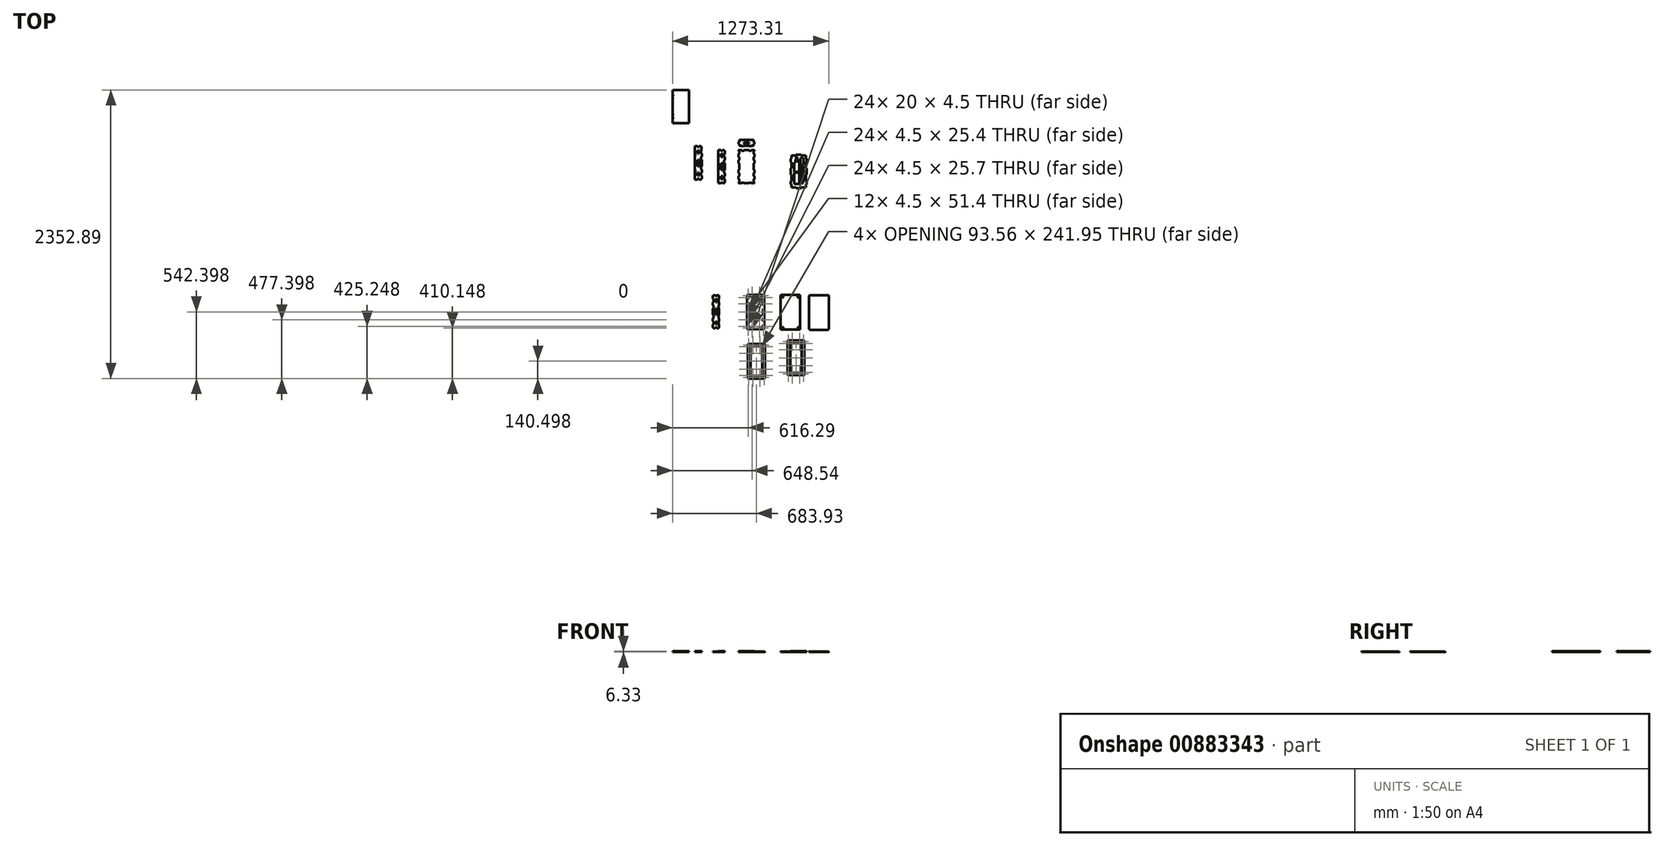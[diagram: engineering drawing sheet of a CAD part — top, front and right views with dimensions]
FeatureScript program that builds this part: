
annotation { "Feature Type Name" : "Feature", "Feature Type Description" : "" }
export const myFeature = defineFeature(function(context is Context, id is Id, definition is map)
    precondition{}
    {
        {
            var Q0;
            Q0=qCreatedBy(makeId("Top.planeOp"),FACE);
            var sketch = newSketch(context, id + "F0", { "sketchPlane" : qUnion([Q0])});
            skLineSegment(sketch, "E0.top", {"start": v(-19.7, 209.17) * mm, "end": v(-0.3, 209.17) * mm});
            skLineSegment(sketch, "E1.bottom", {"start": v(-188.56, 209.17) * mm, "end": v(-174.86, 209.17) * mm});
            skLineSegment(sketch, "E2.top", {"start": v(-40, 250.07) * mm, "end": v(-20.3, 250.07) * mm});
            skLineSegment(sketch, "E2.left", {"start": v(-40, 292.07) * mm, "end": v(-40, 278.37) * mm});
            skLineSegment(sketch, "E3", {"start": v(-154.23, 79.17) * mm, "end": v(-154.23, 105.17) * mm});
            skPoint(sketch, "E4.start.orphan", {"position": v(-160.56, 79.17) * mm});
            skLineSegment(sketch, "E5.bottom", {"start": v(-188.56, 209.17) * mm, "end": v(-181.56, 209.17) * mm});
            skLineSegment(sketch, "E6.0", {"start": v(-20, 298.4) * mm, "end": v(0, 298.4) * mm});
            skLineSegment(sketch, "E7", {"start": v(0, 244.57) * mm, "end": v(0, 243.74) * mm});
            skLineSegment(sketch, "E8", {"start": v(-46.33, 264.07) * mm, "end": v(-46.33, 271.07) * mm});
            skLineSegment(sketch, "E9", {"start": v(-188.56, 215.5) * mm, "end": v(-188.56, 209.17) * mm});
            skPoint(sketch, "E10.end.orphan", {"position": v(-46.33, 209.17) * mm});
            skLineSegment(sketch, "E11.trimOffspring", {"start": v(-154.23, 183.17) * mm, "end": v(-154.23, 209.17) * mm});
            skLineSegment(sketch, "E12.bottom", {"start": v(-45.5, 209.17) * mm, "end": v(-40, 209.17) * mm});
            skLineSegment(sketch, "E13.bottom", {"start": v(-691.17, 64.61) * mm, "end": v(-651.17, 64.61) * mm});
            skLineSegment(sketch, "E13.top", {"start": v(-691.17, -27.39) * mm, "end": v(-651.17, -27.39) * mm});
            skLineSegment(sketch, "E13.left", {"start": v(-691.17, 64.61) * mm, "end": v(-691.17, -27.39) * mm});
            skLineSegment(sketch, "E13.right", {"start": v(-651.17, 64.61) * mm, "end": v(-651.17, -27.39) * mm});
            skLineSegment(sketch, "E14.bottom", {"start": v(-642.38, 180.06) * mm, "end": v(-637.38, 180.06) * mm});
            skLineSegment(sketch, "E14.top", {"start": v(-642.38, 129.06) * mm, "end": v(-632.88, 129.06) * mm});
            skLineSegment(sketch, "E14.left", {"start": v(-642.38, 180.06) * mm, "end": v(-642.38, 129.06) * mm});
            skLineSegment(sketch, "E14.right", {"start": v(-616.38, 180.06) * mm, "end": v(-616.38, 129.06) * mm});
            skLineSegment(sketch, "E15", {"start": v(-629.38, 124.06) * mm, "end": v(-632.88, 124.06) * mm});
            skLineSegment(sketch, "E16", {"start": v(-632.88, 124.06) * mm, "end": v(-625.88, 124.06) * mm});
            skLineSegment(sketch, "E17", {"start": v(-625.88, 124.06) * mm, "end": v(-625.88, 129.06) * mm});
            skLineSegment(sketch, "E18", {"start": v(-632.88, 124.06) * mm, "end": v(-632.88, 129.06) * mm});
            skPoint(sketch, "E19.start.orphan", {"position": v(-629.38, 129.06) * mm});
            skLineSegment(sketch, "E20.trimOffspring", {"start": v(-625.88, 129.06) * mm, "end": v(-616.38, 129.06) * mm});
            skLineSegment(sketch, "E21", {"start": v(-629.38, 190.06) * mm, "end": v(-621.38, 190.06) * mm});
            skLineSegment(sketch, "E22", {"start": v(-621.38, 190.06) * mm, "end": v(-629.38, 190.06) * mm});
            skLineSegment(sketch, "E23", {"start": v(-629.38, 190.06) * mm, "end": v(-637.38, 190.06) * mm});
            skLineSegment(sketch, "E24", {"start": v(-637.38, 190.06) * mm, "end": v(-637.38, 180.06) * mm});
            skLineSegment(sketch, "E25", {"start": v(-621.38, 190.06) * mm, "end": v(-621.38, 180.06) * mm});
            skPoint(sketch, "E26.start.orphan", {"position": v(-629.38, 180.06) * mm});
            skLineSegment(sketch, "E27.trimOffspring", {"start": v(-621.38, 180.06) * mm, "end": v(-616.38, 180.06) * mm});
            skLineSegment(sketch, "E28.bottom", {"start": v(-676.6, 190.8) * mm, "end": v(-665.6, 190.8) * mm});
            skLineSegment(sketch, "E28.top", {"start": v(-691.1, 70.8) * mm, "end": v(-651.1, 70.8) * mm});
            skLineSegment(sketch, "E28.left", {"start": v(-691.1, 148.8) * mm, "end": v(-691.1, 70.8) * mm});
            skLineSegment(sketch, "E29", {"start": v(-691.1, 148.8) * mm, "end": v(-680.1, 148.8) * mm});
            skPoint(sketch, "E30.end.orphan", {"position": v(-676.74, 148.8) * mm});
            skLineSegment(sketch, "E31", {"start": v(-681.6, 153.8) * mm, "end": v(-680.1, 153.8) * mm});
            skLineSegment(sketch, "E32", {"start": v(-676.6, 171.8) * mm, "end": v(-681.6, 171.8) * mm});
            skLineSegment(sketch, "E33", {"start": v(-681.6, 171.8) * mm, "end": v(-676.6, 171.8) * mm});
            skLineSegment(sketch, "E34", {"start": v(-660.6, 171.8) * mm, "end": v(-660.6, 153.8) * mm});
            skLineSegment(sketch, "E35", {"start": v(-662.1, 148.8) * mm, "end": v(-662.1, 153.8) * mm});
            skLineSegment(sketch, "E36", {"start": v(-681.6, 171.8) * mm, "end": v(-681.6, 153.8) * mm});
            skLineSegment(sketch, "E37", {"start": v(-680.1, 148.8) * mm, "end": v(-680.1, 153.8) * mm});
            skLineSegment(sketch, "E38", {"start": v(-665.6, 171.8) * mm, "end": v(-665.6, 189.8) * mm});
            skLineSegment(sketch, "E39", {"start": v(-665.6, 189.8) * mm, "end": v(-665.6, 190.8) * mm});
            skLineSegment(sketch, "E40", {"start": v(-676.6, 171.8) * mm, "end": v(-676.6, 190.8) * mm});
            skLineSegment(sketch, "E41.trimOffspring", {"start": v(-651.1, 148.8) * mm, "end": v(-651.1, 70.8) * mm});
            skPoint(sketch, "E28.right.end.orphan", {"position": v(-651.1, 153.8) * mm});
            skPoint(sketch, "E42.orphan", {"position": v(-691.1, 153.8) * mm});
            skLineSegment(sketch, "E43.trimOffspring", {"start": v(-662.1, 148.8) * mm, "end": v(-651.1, 148.8) * mm});
            skPoint(sketch, "E44.end.orphan", {"position": v(-671.1, 148.8) * mm});
            skLineSegment(sketch, "E45.trimOffspring", {"start": v(-662.1, 153.8) * mm, "end": v(-660.6, 153.8) * mm});
            skPoint(sketch, "E46.start.orphan", {"position": v(-671.1, 153.8) * mm});
            skLineSegment(sketch, "E47.trimOffspring", {"start": v(-665.6, 171.8) * mm, "end": v(-660.6, 171.8) * mm});
            skLineSegment(sketch, "E48.bottom", {"start": v(-639.24, 119.2) * mm, "end": v(-620.24, 119.2) * mm});
            skLineSegment(sketch, "E48.top", {"start": v(-639.24, 53.2) * mm, "end": v(-620.24, 53.2) * mm});
            skLineSegment(sketch, "E48.left", {"start": v(-639.24, 119.2) * mm, "end": v(-639.24, 53.2) * mm});
            skLineSegment(sketch, "E48.right", {"start": v(-620.24, 119.2) * mm, "end": v(-620.24, 53.2) * mm});
            skLineSegment(sketch, "E49.bottom", {"start": v(-639.24, 44.85) * mm, "end": v(-620.24, 44.85) * mm});
            skLineSegment(sketch, "E49.top", {"start": v(-639.24, -21.15) * mm, "end": v(-620.24, -21.15) * mm});
            skLineSegment(sketch, "E49.left", {"start": v(-639.24, 44.85) * mm, "end": v(-639.24, -21.15) * mm});
            skLineSegment(sketch, "E49.right", {"start": v(-620.24, 44.85) * mm, "end": v(-620.24, -21.15) * mm});
            skLineSegment(sketch, "E50.bottom", {"start": v(-715.7, -55.97) * mm, "end": v(-595.7, -55.97) * mm});
            skLineSegment(sketch, "E50.top", {"start": v(-715.7, 204.03) * mm, "end": v(-595.7, 204.03) * mm});
            skLineSegment(sketch, "E50.left", {"start": v(-715.7, -55.97) * mm, "end": v(-715.7, 204.03) * mm});
            skLineSegment(sketch, "E50.right", {"start": v(-595.7, -55.97) * mm, "end": v(-595.7, 204.03) * mm});
            skLineSegment(sketch, "E51.bottom", {"start": v(-878.27, 204.03) * mm, "end": v(-836.27, 204.03) * mm});
            skLineSegment(sketch, "E51.top", {"start": v(-878.27, -55.97) * mm, "end": v(-836.27, -55.97) * mm});
            skLineSegment(sketch, "E51.left", {"start": v(-878.27, 204.03) * mm, "end": v(-878.27, -55.97) * mm});
            skLineSegment(sketch, "E51.right", {"start": v(-836.27, 204.03) * mm, "end": v(-836.27, -55.97) * mm});
            skLineSegment(sketch, "E52.bottom", {"start": v(-715.7, 286.93) * mm, "end": v(-595.7, 286.93) * mm});
            skLineSegment(sketch, "E52.top", {"start": v(-715.7, 244.93) * mm, "end": v(-595.7, 244.93) * mm});
            skLineSegment(sketch, "E52.left", {"start": v(-715.7, 286.93) * mm, "end": v(-715.7, 244.93) * mm});
            skLineSegment(sketch, "E52.right", {"start": v(-595.7, 286.93) * mm, "end": v(-595.7, 244.93) * mm});
            skLineSegment(sketch, "E53", {"start": v(-829.94, 74.03) * mm, "end": v(-829.94, 100.03) * mm});
            skLineSegment(sketch, "E54", {"start": v(-829.94, 204.03) * mm, "end": v(-836.27, 204.03) * mm});
            skLineSegment(sketch, "E55.bottom", {"start": v(-836.27, -55.97) * mm, "end": v(-829.94, -55.97) * mm});
            skLineSegment(sketch, "E55.top", {"start": v(-836.27, 204.03) * mm, "end": v(-829.94, 204.03) * mm});
            skLineSegment(sketch, "E55.left", {"start": v(-836.27, -55.97) * mm, "end": v(-836.27, 204.03) * mm});
            skLineSegment(sketch, "E55.right", {"start": v(-829.94, -55.97) * mm, "end": v(-829.94, 100.03) * mm});
            skPoint(sketch, "E56.start.orphan", {"position": v(-836.27, 74.03) * mm});
            skLineSegment(sketch, "E57", {"start": v(-836.27, 204.03) * mm, "end": v(-836.27, 210.36) * mm});
            skLineSegment(sketch, "E58.left", {"start": v(-878.27, 204.03) * mm, "end": v(-878.27, 210.36) * mm});
            skLineSegment(sketch, "E59", {"start": v(-878.27, -55.97) * mm, "end": v(-884.6, -55.97) * mm});
            skLineSegment(sketch, "E60.bottom", {"start": v(-884.6, -55.97) * mm, "end": v(-878.27, -55.97) * mm});
            skLineSegment(sketch, "E60.top", {"start": v(-884.6, 204.03) * mm, "end": v(-878.27, 204.03) * mm});
            skLineSegment(sketch, "E60.left", {"start": v(-884.6, -55.97) * mm, "end": v(-884.6, 204.03) * mm});
            skLineSegment(sketch, "E60.right", {"start": v(-878.27, -55.97) * mm, "end": v(-878.27, 204.03) * mm});
            skLineSegment(sketch, "E61", {"start": v(-836.27, -55.97) * mm, "end": v(-836.27, -62.3) * mm});
            skLineSegment(sketch, "E62.top", {"start": v(-878.27, -62.3) * mm, "end": v(-836.27, -62.3) * mm});
            skLineSegment(sketch, "E62.left", {"start": v(-878.27, -55.97) * mm, "end": v(-878.27, -62.3) * mm});
            skLineSegment(sketch, "E63.0", {"start": v(-715.7, 293.26) * mm, "end": v(-595.7, 293.26) * mm});
            skLineSegment(sketch, "E63.2", {"start": v(-695.7, 238.6) * mm, "end": v(-675.7, 238.6) * mm});
            skLineSegment(sketch, "E63.3", {"start": v(-589.38, 286.93) * mm, "end": v(-589.38, 244.93) * mm});
            skLineSegment(sketch, "E64.right", {"start": v(-715.7, 293.26) * mm, "end": v(-715.7, 286.93) * mm});
            skLineSegment(sketch, "E65.bottom", {"start": v(-595.7, 286.93) * mm, "end": v(-589.38, 286.93) * mm});
            skLineSegment(sketch, "E65.left", {"start": v(-595.7, 286.93) * mm, "end": v(-595.7, 293.26) * mm});
            skLineSegment(sketch, "E66.bottom", {"start": v(-595.7, 244.93) * mm, "end": v(-589.38, 244.93) * mm});
            skLineSegment(sketch, "E66.left", {"start": v(-595.7, 244.93) * mm, "end": v(-595.7, 238.6) * mm});
            skLineSegment(sketch, "E67.0", {"start": v(-715.7, 210.36) * mm, "end": v(-695.7, 210.36) * mm});
            skLineSegment(sketch, "E67.1", {"start": v(-722.04, -55.97) * mm, "end": v(-722.04, 74.03) * mm});
            skLineSegment(sketch, "E67.2", {"start": v(-715.7, -62.3) * mm, "end": v(-595.7, -62.3) * mm});
            skLineSegment(sketch, "E67.3", {"start": v(-589.38, -55.97) * mm, "end": v(-589.38, 204.03) * mm});
            skLineSegment(sketch, "E68.bottom", {"start": v(-595.7, 204.03) * mm, "end": v(-589.38, 204.03) * mm});
            skLineSegment(sketch, "E68.left", {"start": v(-595.7, 204.03) * mm, "end": v(-595.7, 210.36) * mm});
            skLineSegment(sketch, "E69.top", {"start": v(-589.38, -55.97) * mm, "end": v(-595.7, -55.97) * mm});
            skLineSegment(sketch, "E69.right", {"start": v(-595.7, -62.3) * mm, "end": v(-595.7, -55.97) * mm});
            skLineSegment(sketch, "E70.top", {"start": v(-722.04, -55.97) * mm, "end": v(-715.7, -55.97) * mm});
            skLineSegment(sketch, "E70.right", {"start": v(-715.7, -62.3) * mm, "end": v(-715.7, -55.97) * mm});
            skLineSegment(sketch, "E71", {"start": v(-655.7, 204.03) * mm, "end": v(-655.7, 189.78) * mm});
            skLineSegment(sketch, "E72", {"start": v(-655.7, 204.03) * mm, "end": v(-655.7, 210.36) * mm});
            skLineSegment(sketch, "E73", {"start": v(-655.7, 210.36) * mm, "end": v(-675.7, 210.36) * mm});
            skLineSegment(sketch, "E74", {"start": v(-675.7, 210.36) * mm, "end": v(-675.7, 204.03) * mm});
            skLineSegment(sketch, "E75", {"start": v(-695.7, 210.36) * mm, "end": v(-695.7, 204.03) * mm});
            skLineSegment(sketch, "E76.trimOffspring", {"start": v(-695.7, 210.36) * mm, "end": v(-715.7, 210.36) * mm});
            skLineSegment(sketch, "E77.trimOffspring", {"start": v(-675.7, 210.36) * mm, "end": v(-595.7, 210.36) * mm});
            skLineSegment(sketch, "E78", {"start": v(-695.7, 244.93) * mm, "end": v(-695.7, 238.6) * mm});
            skLineSegment(sketch, "E79", {"start": v(-675.7, 244.93) * mm, "end": v(-675.7, 238.6) * mm});
            skLineSegment(sketch, "E80", {"start": v(-655.7, 238.6) * mm, "end": v(-655.7, 244.93) * mm});
            skLineSegment(sketch, "E81.trimOffspring", {"start": v(-655.7, 238.6) * mm, "end": v(-595.7, 238.6) * mm});
            skLineSegment(sketch, "E82", {"start": v(-722.04, 258.93) * mm, "end": v(-722.04, 272.93) * mm});
            skLineSegment(sketch, "E83", {"start": v(-722.04, 258.93) * mm, "end": v(-715.7, 258.93) * mm});
            skLineSegment(sketch, "E84", {"start": v(-722.04, 272.93) * mm, "end": v(-715.7, 272.93) * mm});
            skLineSegment(sketch, "E85", {"start": v(-878.27, 210.36) * mm, "end": v(-864.27, 210.36) * mm});
            skLineSegment(sketch, "E86", {"start": v(-850.27, 210.36) * mm, "end": v(-836.27, 210.36) * mm});
            skLineSegment(sketch, "E87", {"start": v(-850.27, 210.36) * mm, "end": v(-850.27, 204.03) * mm});
            skLineSegment(sketch, "E88", {"start": v(-864.27, 210.36) * mm, "end": v(-864.27, 204.03) * mm});
            skLineSegment(sketch, "E89", {"start": v(-722.04, 74.03) * mm, "end": v(-715.7, 74.03) * mm});
            skLineSegment(sketch, "E90", {"start": v(-722.04, 100.03) * mm, "end": v(-722.04, 126.03) * mm});
            skLineSegment(sketch, "E91", {"start": v(-722.04, 152.03) * mm, "end": v(-722.04, 178.03) * mm});
            skLineSegment(sketch, "E92", {"start": v(-722.04, 178.03) * mm, "end": v(-715.7, 178.03) * mm});
            skLineSegment(sketch, "E93", {"start": v(-722.04, 152.03) * mm, "end": v(-715.7, 152.03) * mm});
            skLineSegment(sketch, "E94", {"start": v(-722.04, 126.03) * mm, "end": v(-715.7, 126.03) * mm});
            skLineSegment(sketch, "E95", {"start": v(-722.04, 100.03) * mm, "end": v(-715.7, 100.03) * mm});
            skPoint(sketch, "E96.end.orphan", {"position": v(-722.04, 204.03) * mm});
            skLineSegment(sketch, "E97", {"start": v(-829.94, 178.03) * mm, "end": v(-836.27, 178.03) * mm});
            skLineSegment(sketch, "E98", {"start": v(-829.94, 152.03) * mm, "end": v(-836.27, 152.03) * mm});
            skLineSegment(sketch, "E99", {"start": v(-829.94, 126.03) * mm, "end": v(-836.27, 126.03) * mm});
            skLineSegment(sketch, "E100", {"start": v(-829.94, 100.03) * mm, "end": v(-836.27, 100.03) * mm});
            skLineSegment(sketch, "E101", {"start": v(-829.94, 74.03) * mm, "end": v(-836.27, 74.03) * mm});
            skLineSegment(sketch, "E102.trimOffspring", {"start": v(-829.94, 126.03) * mm, "end": v(-829.94, 152.03) * mm});
            skLineSegment(sketch, "E103.trimOffspring", {"start": v(-829.94, 178.03) * mm, "end": v(-829.94, 204.03) * mm});
            skLineSegment(sketch, "E104.bottom", {"start": v(-722.04, 204.03) * mm, "end": v(-715.7, 204.03) * mm});
            skLineSegment(sketch, "E104.top", {"start": v(-722.04, 210.36) * mm, "end": v(-715.7, 210.36) * mm});
            skLineSegment(sketch, "E104.left", {"start": v(-722.04, 204.03) * mm, "end": v(-722.04, 210.36) * mm});
            skLineSegment(sketch, "E105.trimOffspring", {"start": v(-160.56, 105.47) * mm, "end": v(-160.56, 130.87) * mm});
            skLineSegment(sketch, "E106.trimOffspring", {"start": v(-160.56, 157.47) * mm, "end": v(-160.56, 182.87) * mm});
            skLineSegment(sketch, "E107.trimOffspring", {"start": v(-160.56, 130.87) * mm, "end": v(-160.56, 105.47) * mm});
            skLineSegment(sketch, "E108.MirrorCS", {"start": v(44.01, 243.74) * mm, "end": v(40, 243.74) * mm});
            skLineSegment(sketch, "E109.MirrorCS", {"start": v(44.01, 244.57) * mm, "end": v(44.01, 243.74) * mm});
            skPoint(sketch, "E110.end.orphan", {"position": v(20, 250.07) * mm});
            skPoint(sketch, "E110.start.orphan", {"position": v(20, 243.74) * mm});
            skLineSegment(sketch, "E111.trimOffspring", {"start": v(0.3, 250.07) * mm, "end": v(20, 250.07) * mm});
            skLineSegment(sketch, "E112.trimOffspring", {"start": v(60.3, 250.07) * mm, "end": v(80, 250.07) * mm});
            skLineSegment(sketch, "E113.trimOffspring", {"start": v(80, 263.77) * mm, "end": v(80, 250.07) * mm});
            skLineSegment(sketch, "E114.trimOffspring", {"start": v(-40, 263.77) * mm, "end": v(-40, 250.07) * mm});
            skLineSegment(sketch, "E115.MirrorCS", {"start": v(40, 298.4) * mm, "end": v(60, 298.4) * mm});
            skPoint(sketch, "E116.start.orphan", {"position": v(-46.33, 271.07) * mm});
            skLineSegment(sketch, "E117.trimOffspring", {"start": v(-40, 79.17) * mm, "end": v(-40, 104.87) * mm});
            skLineSegment(sketch, "E118.trimOffspring", {"start": v(-40, 131.47) * mm, "end": v(-40, 156.87) * mm});
            skLineSegment(sketch, "E119.trimOffspring", {"start": v(-40, 183.47) * mm, "end": v(-40, 209.17) * mm});
            skPoint(sketch, "E120.start.orphan", {"position": v(-46.33, 79.17) * mm});
            skLineSegment(sketch, "E121.bottom", {"start": v(410.43, 29.57) * mm, "end": v(450.43, 29.57) * mm});
            skLineSegment(sketch, "E121.top", {"start": v(410.43, -62.43) * mm, "end": v(450.43, -62.43) * mm});
            skLineSegment(sketch, "E121.left", {"start": v(410.43, 29.57) * mm, "end": v(410.43, -62.43) * mm});
            skLineSegment(sketch, "E121.right", {"start": v(450.43, 29.57) * mm, "end": v(450.43, -62.43) * mm});
            skLineSegment(sketch, "E122.bottom", {"start": v(459.21, 145.03) * mm, "end": v(464.21, 145.03) * mm});
            skLineSegment(sketch, "E122.top", {"start": v(459.21, 94.03) * mm, "end": v(468.71, 94.03) * mm});
            skLineSegment(sketch, "E122.left", {"start": v(459.21, 145.03) * mm, "end": v(459.21, 94.03) * mm});
            skLineSegment(sketch, "E122.right", {"start": v(485.21, 145.03) * mm, "end": v(485.21, 94.03) * mm});
            skLineSegment(sketch, "E123", {"start": v(472.21, 89.03) * mm, "end": v(468.71, 89.03) * mm});
            skLineSegment(sketch, "E124", {"start": v(468.71, 89.03) * mm, "end": v(475.71, 89.03) * mm});
            skLineSegment(sketch, "E125", {"start": v(475.71, 89.03) * mm, "end": v(475.71, 94.03) * mm});
            skLineSegment(sketch, "E126", {"start": v(468.71, 89.03) * mm, "end": v(468.71, 94.03) * mm});
            skPoint(sketch, "E127.start.orphan", {"position": v(472.21, 94.03) * mm});
            skLineSegment(sketch, "E128.trimOffspring", {"start": v(475.71, 94.03) * mm, "end": v(485.21, 94.03) * mm});
            skLineSegment(sketch, "E129", {"start": v(472.21, 155.03) * mm, "end": v(480.21, 155.03) * mm});
            skLineSegment(sketch, "E130", {"start": v(480.21, 155.03) * mm, "end": v(472.21, 155.03) * mm});
            skLineSegment(sketch, "E131", {"start": v(472.21, 155.03) * mm, "end": v(464.21, 155.03) * mm});
            skLineSegment(sketch, "E132", {"start": v(464.21, 155.03) * mm, "end": v(464.21, 145.03) * mm});
            skLineSegment(sketch, "E133", {"start": v(480.21, 155.03) * mm, "end": v(480.21, 145.03) * mm});
            skPoint(sketch, "E134.start.orphan", {"position": v(472.21, 145.03) * mm});
            skLineSegment(sketch, "E135.trimOffspring", {"start": v(480.21, 145.03) * mm, "end": v(485.21, 145.03) * mm});
            skLineSegment(sketch, "E136.bottom", {"start": v(425, 155.77) * mm, "end": v(436, 155.77) * mm});
            skLineSegment(sketch, "E136.top", {"start": v(410.5, 35.77) * mm, "end": v(450.5, 35.77) * mm});
            skLineSegment(sketch, "E136.left", {"start": v(410.5, 113.77) * mm, "end": v(410.5, 35.77) * mm});
            skLineSegment(sketch, "E137", {"start": v(410.5, 113.77) * mm, "end": v(421.5, 113.77) * mm});
            skPoint(sketch, "E138.end.orphan", {"position": v(424.86, 113.77) * mm});
            skLineSegment(sketch, "E139", {"start": v(420, 118.77) * mm, "end": v(421.5, 118.77) * mm});
            skLineSegment(sketch, "E140", {"start": v(425, 136.77) * mm, "end": v(420, 136.77) * mm});
            skLineSegment(sketch, "E141", {"start": v(420, 136.77) * mm, "end": v(425, 136.77) * mm});
            skLineSegment(sketch, "E142", {"start": v(441, 136.77) * mm, "end": v(441, 118.77) * mm});
            skLineSegment(sketch, "E143", {"start": v(439.5, 113.77) * mm, "end": v(439.5, 118.77) * mm});
            skLineSegment(sketch, "E144", {"start": v(420, 136.77) * mm, "end": v(420, 118.77) * mm});
            skLineSegment(sketch, "E145", {"start": v(421.5, 113.77) * mm, "end": v(421.5, 118.77) * mm});
            skLineSegment(sketch, "E146", {"start": v(436, 136.77) * mm, "end": v(436, 154.77) * mm});
            skLineSegment(sketch, "E147", {"start": v(436, 154.77) * mm, "end": v(436, 155.77) * mm});
            skLineSegment(sketch, "E148", {"start": v(425, 136.77) * mm, "end": v(425, 155.77) * mm});
            skLineSegment(sketch, "E149.trimOffspring", {"start": v(450.5, 113.77) * mm, "end": v(450.5, 35.77) * mm});
            skPoint(sketch, "E136.right.end.orphan", {"position": v(450.5, 118.77) * mm});
            skPoint(sketch, "E150.orphan", {"position": v(410.5, 118.77) * mm});
            skLineSegment(sketch, "E151.trimOffspring", {"start": v(439.5, 113.77) * mm, "end": v(450.5, 113.77) * mm});
            skPoint(sketch, "E152.end.orphan", {"position": v(430.5, 113.77) * mm});
            skLineSegment(sketch, "E153.trimOffspring", {"start": v(439.5, 118.77) * mm, "end": v(441, 118.77) * mm});
            skPoint(sketch, "E154.start.orphan", {"position": v(430.5, 118.77) * mm});
            skLineSegment(sketch, "E155.trimOffspring", {"start": v(436, 136.77) * mm, "end": v(441, 136.77) * mm});
            skLineSegment(sketch, "E156.bottom", {"start": v(462.36, 84.16) * mm, "end": v(481.36, 84.16) * mm});
            skLineSegment(sketch, "E156.top", {"start": v(462.36, 18.16) * mm, "end": v(481.36, 18.16) * mm});
            skLineSegment(sketch, "E156.left", {"start": v(462.36, 84.16) * mm, "end": v(462.36, 18.16) * mm});
            skLineSegment(sketch, "E156.right", {"start": v(481.36, 84.16) * mm, "end": v(481.36, 18.16) * mm});
            skLineSegment(sketch, "E157.bottom", {"start": v(462.36, 9.81) * mm, "end": v(481.36, 9.81) * mm});
            skLineSegment(sketch, "E157.top", {"start": v(462.36, -56.19) * mm, "end": v(481.36, -56.19) * mm});
            skLineSegment(sketch, "E157.left", {"start": v(462.36, 9.81) * mm, "end": v(462.36, -56.19) * mm});
            skLineSegment(sketch, "E157.right", {"start": v(481.36, 9.81) * mm, "end": v(481.36, -56.19) * mm});
            skLineSegment(sketch, "E158.bottom", {"start": v(405.88, -91.01) * mm, "end": v(425.88, -91.01) * mm});
            skLineSegment(sketch, "E158.top", {"start": v(405.88, 168.99) * mm, "end": v(425.88, 168.99) * mm});
            skLineSegment(sketch, "E158.left", {"start": v(385.88, -91.01) * mm, "end": v(385.88, -65.01) * mm});
            skLineSegment(sketch, "E158.right", {"start": v(505.88, -91.01) * mm, "end": v(505.88, -65.01) * mm});
            skLineSegment(sketch, "E159.1", {"start": v(379.55, -65.01) * mm, "end": v(379.55, -39.01) * mm});
            skLineSegment(sketch, "E160", {"start": v(445.88, 175.32) * mm, "end": v(425.88, 175.32) * mm});
            skLineSegment(sketch, "E161", {"start": v(425.88, 175.32) * mm, "end": v(425.88, 168.99) * mm});
            skLineSegment(sketch, "E162.trimOffspring", {"start": v(425.88, 175.32) * mm, "end": v(465.88, 175.32) * mm});
            skLineSegment(sketch, "E163", {"start": v(379.55, 116.99) * mm, "end": v(379.55, 142.99) * mm});
            skLineSegment(sketch, "E164", {"start": v(379.55, 142.99) * mm, "end": v(385.88, 142.99) * mm});
            skLineSegment(sketch, "E165", {"start": v(379.55, 116.99) * mm, "end": v(385.88, 116.99) * mm});
            skLineSegment(sketch, "E166", {"start": v(379.55, 64.99) * mm, "end": v(385.88, 64.99) * mm});
            skPoint(sketch, "E167.end.orphan", {"position": v(379.55, 168.99) * mm});
            skPoint(sketch, "E168.start.orphan", {"position": v(445.88, 203.56) * mm});
            skLineSegment(sketch, "E169.MirrorCS", {"start": v(379.55, 12.99) * mm, "end": v(385.88, 12.99) * mm});
            skLineSegment(sketch, "E170.MirrorCS", {"start": v(379.55, -39.01) * mm, "end": v(385.88, -39.01) * mm});
            skLineSegment(sketch, "E171.MirrorCS", {"start": v(379.55, -39.01) * mm, "end": v(379.55, -65.01) * mm});
            skLineSegment(sketch, "E172.MirrorCS", {"start": v(379.55, -65.01) * mm, "end": v(385.88, -65.01) * mm});
            skLineSegment(sketch, "E173.trimOffspring", {"start": v(385.88, -39.01) * mm, "end": v(385.88, -13.01) * mm});
            skLineSegment(sketch, "E174.trimOffspring", {"start": v(385.88, 90.99) * mm, "end": v(385.88, 116.99) * mm});
            skLineSegment(sketch, "E175.trimOffspring", {"start": v(385.88, 142.99) * mm, "end": v(385.88, 168.99) * mm});
            skLineSegment(sketch, "E176.trimOffspring", {"start": v(465.88, 168.99) * mm, "end": v(485.88, 168.99) * mm});
            skLineSegment(sketch, "E177.MirrorCS", {"start": v(425.88, -97.34) * mm, "end": v(425.88, -91.01) * mm});
            skLineSegment(sketch, "E178.MirrorCS", {"start": v(465.88, 175.32) * mm, "end": v(465.88, 168.99) * mm});
            skLineSegment(sketch, "E179.MirrorCS", {"start": v(512.21, -39.01) * mm, "end": v(505.88, -39.01) * mm});
            skLineSegment(sketch, "E180.MirrorCS", {"start": v(512.21, 64.99) * mm, "end": v(505.88, 64.99) * mm});
            skLineSegment(sketch, "E181.MirrorCS", {"start": v(512.21, 142.99) * mm, "end": v(505.88, 142.99) * mm});
            skLineSegment(sketch, "E182.MirrorCS", {"start": v(512.21, 116.99) * mm, "end": v(505.88, 116.99) * mm});
            skLineSegment(sketch, "E183.MirrorCS", {"start": v(512.21, -65.01) * mm, "end": v(505.88, -65.01) * mm});
            skLineSegment(sketch, "E184.MirrorCS", {"start": v(512.21, 12.99) * mm, "end": v(505.88, 12.99) * mm});
            skLineSegment(sketch, "E185.MirrorCS", {"start": v(512.21, 116.99) * mm, "end": v(512.21, 142.99) * mm});
            skLineSegment(sketch, "E186.MirrorCS", {"start": v(512.21, -39.01) * mm, "end": v(512.21, -65.01) * mm});
            skLineSegment(sketch, "E187.MirrorCS", {"start": v(505.88, 142.99) * mm, "end": v(505.88, 168.99) * mm});
            skPoint(sketch, "E188.MirrorP", {"position": v(512.21, 168.99) * mm});
            skLineSegment(sketch, "E189.MirrorCS", {"start": v(505.88, 90.99) * mm, "end": v(505.88, 116.99) * mm});
            skLineSegment(sketch, "E190.MirrorCS", {"start": v(505.88, -39.01) * mm, "end": v(505.88, -13.01) * mm});
            skLineSegment(sketch, "E191.MirrorCS", {"start": v(512.21, -65.01) * mm, "end": v(512.21, -39.01) * mm});
            skLineSegment(sketch, "E192.MirrorCS", {"start": v(485.88, -91.01) * mm, "end": v(465.88, -91.01) * mm});
            skLineSegment(sketch, "E193.MirrorCS", {"start": v(465.88, -97.34) * mm, "end": v(465.88, -91.01) * mm});
            skPoint(sketch, "E194.MirrorCS.end.orphan", {"position": v(505.88, 38.99) * mm});
            skPoint(sketch, "E194.MirrorCS.start.orphan", {"position": v(512.21, 38.99) * mm});
            skLineSegment(sketch, "E195.trimOffspring", {"start": v(425.88, -97.34) * mm, "end": v(465.88, -97.34) * mm});
            skLineSegment(sketch, "E196.trimOffspring", {"start": v(465.88, -91.01) * mm, "end": v(485.88, -91.01) * mm});
            skPoint(sketch, "E197.end.orphan", {"position": v(385.88, 38.99) * mm});
            skPoint(sketch, "E197.start.orphan", {"position": v(379.55, 38.99) * mm});
            skLineSegment(sketch, "E198.bottom", {"start": v(385.88, 168.99) * mm, "end": v(425.88, 168.99) * mm});
            skLineSegment(sketch, "E198.top", {"start": v(385.88, -91.01) * mm, "end": v(425.88, -91.01) * mm});
            skLineSegment(sketch, "E198.left", {"start": v(385.88, 168.99) * mm, "end": v(385.88, 142.99) * mm});
            skLineSegment(sketch, "E198.right", {"start": v(505.88, 168.99) * mm, "end": v(505.88, 142.99) * mm});
            skPoint(sketch, "E199.top.end.orphan", {"position": v(385.88, 175.32) * mm});
            skPoint(sketch, "E200.trimOffspring.end.orphan", {"position": v(505.88, 175.32) * mm});
            skLineSegment(sketch, "E201", {"start": v(379.55, 64.99) * mm, "end": v(379.55, 12.99) * mm});
            skLineSegment(sketch, "E202", {"start": v(512.21, 64.99) * mm, "end": v(512.21, 12.99) * mm});
            skPoint(sketch, "E203.top.start.orphan", {"position": v(379.55, -91.01) * mm});
            skLineSegment(sketch, "E204.trimOffspring", {"start": v(465.88, -91.01) * mm, "end": v(505.88, -91.01) * mm});
            skLineSegment(sketch, "E205.trimOffspring", {"start": v(505.88, -65.01) * mm, "end": v(505.88, -91.01) * mm});
            skLineSegment(sketch, "E206.trimOffspring", {"start": v(385.88, -65.01) * mm, "end": v(385.88, -91.01) * mm});
            skLineSegment(sketch, "E207.trimOffspring", {"start": v(385.88, 12.99) * mm, "end": v(385.88, -39.01) * mm});
            skLineSegment(sketch, "E208.trimOffspring", {"start": v(505.88, 12.99) * mm, "end": v(505.88, -39.01) * mm});
            skLineSegment(sketch, "E209.trimOffspring", {"start": v(505.88, 116.99) * mm, "end": v(505.88, 64.99) * mm});
            skLineSegment(sketch, "E210.trimOffspring", {"start": v(385.88, 116.99) * mm, "end": v(385.88, 64.99) * mm});
            skLineSegment(sketch, "E211.trimOffspring", {"start": v(465.88, 168.99) * mm, "end": v(505.88, 168.99) * mm});
            skPoint(sketch, "E212.start.orphan", {"position": v(445.88, 168.99) * mm});
            skLineSegment(sketch, "E213", {"start": v(-171.53, 183.17) * mm, "end": v(-176.73, 183.17) * mm});
            skLineSegment(sketch, "E214", {"start": v(-171.53, 105.17) * mm, "end": v(-176.73, 105.17) * mm});
            skLineSegment(sketch, "E215.bottom", {"start": v(-186.93, 183.17) * mm, "end": v(-181.73, 183.17) * mm});
            skLineSegment(sketch, "E215.top", {"start": v(-186.93, 157.17) * mm, "end": v(-181.73, 157.17) * mm});
            skLineSegment(sketch, "E215.left", {"start": v(-208.9, 183.17) * mm, "end": v(-208.9, 157.17) * mm});
            skLineSegment(sketch, "E216", {"start": v(-171.53, 53.17) * mm, "end": v(-176.73, 53.17) * mm});
            skLineSegment(sketch, "E217", {"start": v(-184.73, 183.17) * mm, "end": v(-181.73, 183.17) * mm});
            skLineSegment(sketch, "E218", {"start": v(-181.73, 183.17) * mm, "end": v(-186.93, 183.17) * mm});
            skLineSegment(sketch, "E219", {"start": v(-186.93, 183.17) * mm, "end": v(-186.93, 157.17) * mm});
            skLineSegment(sketch, "E220", {"start": v(-181.73, 183.17) * mm, "end": v(-181.73, 157.17) * mm});
            skPoint(sketch, "E221.end.orphan", {"position": v(-184.73, 157.17) * mm});
            skLineSegment(sketch, "E222", {"start": v(-154.23, 79.17) * mm, "end": v(-136.78, 79.17) * mm});
            skLineSegment(sketch, "E223", {"start": v(-181.73, 105.17) * mm, "end": v(-181.73, 53.17) * mm});
            skLineSegment(sketch, "E224", {"start": v(-186.93, 105.17) * mm, "end": v(-186.93, 53.17) * mm});
            skLineSegment(sketch, "E225.MirrorCS", {"start": v(-176.73, 105.17) * mm, "end": v(-176.73, 53.17) * mm});
            skLineSegment(sketch, "E226", {"start": v(-176.73, 157.17) * mm, "end": v(-176.73, 183.17) * mm});
            skLineSegment(sketch, "E227", {"start": v(-171.53, 157.17) * mm, "end": v(-171.53, 183.17) * mm});
            skLineSegment(sketch, "E228.trimOffspring", {"start": v(-176.73, 157.17) * mm, "end": v(-171.53, 157.17) * mm});
            skPoint(sketch, "E229.start.orphan", {"position": v(-179.23, 105.17) * mm});
            skPoint(sketch, "E230.orphan", {"position": v(-176.73, 105.17) * mm});
            skLineSegment(sketch, "E231.trimOffspring", {"start": v(-181.83, 105.17) * mm, "end": v(-186.93, 105.17) * mm});
            skLineSegment(sketch, "E232.trimOffspring", {"start": v(-181.83, 53.17) * mm, "end": v(-186.93, 53.17) * mm});
            skLineSegment(sketch, "E233.top", {"start": v(-40, 298.4) * mm, "end": v(-20, 298.4) * mm});
            skLineSegment(sketch, "E233.left", {"start": v(-40, 292.07) * mm, "end": v(-40, 298.4) * mm});
            skLineSegment(sketch, "E234.bottom", {"start": v(-40, 298.4) * mm, "end": v(80, 298.4) * mm});
            skLineSegment(sketch, "E234.left", {"start": v(-40, 298.4) * mm, "end": v(-40, 292.07) * mm});
            skLineSegment(sketch, "E234.right", {"start": v(80, 298.4) * mm, "end": v(80, 292.07) * mm});
            skPoint(sketch, "E5.right.start.orphan", {"position": v(-160.56, 209.17) * mm});
            skLineSegment(sketch, "E235.left", {"start": v(-160.56, 214.67) * mm, "end": v(-160.56, 215.5) * mm});
            skLineSegment(sketch, "E236.top", {"start": v(-208.9, 215.5) * mm, "end": v(-202.56, 215.5) * mm});
            skLineSegment(sketch, "E236.left", {"start": v(-208.9, 209.17) * mm, "end": v(-208.9, 215.5) * mm});
            skLineSegment(sketch, "E237", {"start": v(0, 261.04) * mm, "end": v(40, 261.04) * mm});
            skLineSegment(sketch, "E238.left", {"start": v(0, 266.24) * mm, "end": v(0, 261.04) * mm});
            skLineSegment(sketch, "E239", {"start": v(0, 261.04) * mm, "end": v(0, 266.24) * mm});
            skPoint(sketch, "E240.firstSnap0", {"position": v(44.01, 263.64) * mm});
            skLineSegment(sketch, "E240.top", {"start": v(40, 276.44) * mm, "end": v(0, 276.44) * mm});
            skLineSegment(sketch, "E240.right", {"start": v(0, 271.24) * mm, "end": v(0, 276.44) * mm});
            skPoint(sketch, "E241.orphan", {"position": v(0, 271.24) * mm});
            skLineSegment(sketch, "E242.bottom", {"start": v(-378.34, 239.1) * mm, "end": v(-364.34, 239.1) * mm});
            skLineSegment(sketch, "E242.top", {"start": v(-378.34, -21.5) * mm, "end": v(-364.64, -21.5) * mm});
            skLineSegment(sketch, "E243", {"start": v(-344.01, 108.5) * mm, "end": v(-344.01, 134.5) * mm});
            skLineSegment(sketch, "E244.left", {"start": v(-350.34, 4.5) * mm, "end": v(-350.34, 30.5) * mm});
            skLineSegment(sketch, "E244.right", {"start": v(-344.01, -21.5) * mm, "end": v(-344.01, 4.5) * mm});
            skPoint(sketch, "E245.start.orphan", {"position": v(-350.34, 108.8) * mm});
            skLineSegment(sketch, "E246.bottom", {"start": v(-378.34, 239.1) * mm, "end": v(-371.34, 239.1) * mm});
            skLineSegment(sketch, "E247.left", {"start": v(-398.67, -21.5) * mm, "end": v(-398.67, 239.1) * mm});
            skLineSegment(sketch, "E248.top", {"start": v(-392.34, -27.82) * mm, "end": v(-378.34, -27.82) * mm});
            skLineSegment(sketch, "E249", {"start": v(-364.34, 244.8) * mm, "end": v(-364.34, 239.1) * mm});
            skLineSegment(sketch, "E250", {"start": v(-378.34, 244.8) * mm, "end": v(-378.34, 239.1) * mm});
            skLineSegment(sketch, "E251", {"start": v(-344.01, 212.5) * mm, "end": v(-350.34, 212.5) * mm});
            skLineSegment(sketch, "E252", {"start": v(-344.01, 186.5) * mm, "end": v(-350.34, 186.5) * mm});
            skLineSegment(sketch, "E253", {"start": v(-344.01, 159.9) * mm, "end": v(-350.34, 159.9) * mm});
            skLineSegment(sketch, "E254", {"start": v(-344.01, 134.5) * mm, "end": v(-350.34, 134.5) * mm});
            skLineSegment(sketch, "E255.trimOffspring", {"start": v(-344.01, 159.9) * mm, "end": v(-344.01, 186.5) * mm});
            skLineSegment(sketch, "E256.MirrorCS", {"start": v(-344.01, 82.5) * mm, "end": v(-350.34, 82.5) * mm});
            skLineSegment(sketch, "E257.MirrorCS", {"start": v(-344.01, 56.5) * mm, "end": v(-350.34, 56.5) * mm});
            skLineSegment(sketch, "E258.MirrorCS", {"start": v(-344.01, 56.5) * mm, "end": v(-344.01, 30.5) * mm});
            skLineSegment(sketch, "E259.MirrorCS", {"start": v(-344.01, 30.5) * mm, "end": v(-350.34, 30.5) * mm});
            skLineSegment(sketch, "E260.MirrorCS", {"start": v(-344.01, 4.5) * mm, "end": v(-350.34, 4.5) * mm});
            skLineSegment(sketch, "E261.MirrorCS", {"start": v(-344.01, 4.5) * mm, "end": v(-344.01, -21.5) * mm});
            skLineSegment(sketch, "E262.MirrorCS", {"start": v(-364.34, -27.82) * mm, "end": v(-350.34, -27.82) * mm});
            skLineSegment(sketch, "E263.MirrorCS", {"start": v(-378.34, -27.82) * mm, "end": v(-378.34, -21.5) * mm});
            skLineSegment(sketch, "E264.trimOffspring", {"start": v(-344.01, 82.5) * mm, "end": v(-344.01, 134.5) * mm});
            skLineSegment(sketch, "E265.trimOffspring", {"start": v(-344.01, 30.5) * mm, "end": v(-344.01, 56.5) * mm});
            skPoint(sketch, "E266.orphan", {"position": v(-392.34, -21.5) * mm});
            skPoint(sketch, "E267.orphan", {"position": v(-350.34, -21.5) * mm});
            skLineSegment(sketch, "E268.trimOffspring", {"start": v(-350.34, 56.5) * mm, "end": v(-350.34, 82.5) * mm});
            skLineSegment(sketch, "E269.trimOffspring", {"start": v(-350.34, 30.5) * mm, "end": v(-350.34, 4.5) * mm});
            skLineSegment(sketch, "E270.trimOffspring", {"start": v(-350.34, 82.5) * mm, "end": v(-350.34, 56.5) * mm});
            skLineSegment(sketch, "E271.trimOffspring", {"start": v(-350.34, 134.5) * mm, "end": v(-350.34, 159.9) * mm});
            skLineSegment(sketch, "E272.trimOffspring", {"start": v(-350.34, 186.5) * mm, "end": v(-350.34, 212.5) * mm});
            skLineSegment(sketch, "E273.trimOffspring", {"start": v(-350.34, 159.9) * mm, "end": v(-350.34, 134.5) * mm});
            skLineSegment(sketch, "E274", {"start": v(-361.3, 212.5) * mm, "end": v(-366.5, 212.5) * mm});
            skLineSegment(sketch, "E275", {"start": v(-361.3, 134.5) * mm, "end": v(-366.5, 134.5) * mm});
            skLineSegment(sketch, "E276.bottom", {"start": v(-376.7, 212.5) * mm, "end": v(-371.5, 212.5) * mm});
            skLineSegment(sketch, "E276.top", {"start": v(-376.7, 186.5) * mm, "end": v(-371.5, 186.5) * mm});
            skLineSegment(sketch, "E276.left", {"start": v(-398.67, 212.5) * mm, "end": v(-398.67, 186.5) * mm});
            skLineSegment(sketch, "E276.right", {"start": v(-350.34, 212.5) * mm, "end": v(-350.34, 186.5) * mm});
            skLineSegment(sketch, "E277", {"start": v(-361.3, 82.5) * mm, "end": v(-366.5, 82.5) * mm});
            skLineSegment(sketch, "E278", {"start": v(-374.5, 212.5) * mm, "end": v(-371.5, 212.5) * mm});
            skLineSegment(sketch, "E279", {"start": v(-371.5, 212.5) * mm, "end": v(-376.7, 212.5) * mm});
            skLineSegment(sketch, "E280", {"start": v(-376.7, 212.5) * mm, "end": v(-376.7, 186.5) * mm});
            skLineSegment(sketch, "E281", {"start": v(-371.5, 212.5) * mm, "end": v(-371.5, 186.5) * mm});
            skPoint(sketch, "E282.end.orphan", {"position": v(-374.5, 186.5) * mm});
            skLineSegment(sketch, "E283", {"start": v(-344.01, 108.5) * mm, "end": v(-326.56, 108.5) * mm});
            skLineSegment(sketch, "E284", {"start": v(-371.5, 134.5) * mm, "end": v(-371.5, 82.5) * mm});
            skLineSegment(sketch, "E285", {"start": v(-376.7, 134.5) * mm, "end": v(-376.7, 82.5) * mm});
            skLineSegment(sketch, "E286.MirrorCS", {"start": v(-376.7, 4.5) * mm, "end": v(-376.7, 30.5) * mm});
            skLineSegment(sketch, "E287.MirrorCS", {"start": v(-371.5, 4.5) * mm, "end": v(-371.5, 30.5) * mm});
            skLineSegment(sketch, "E288.bottom", {"start": v(-376.7, 4.5) * mm, "end": v(-371.5, 4.5) * mm});
            skLineSegment(sketch, "E288.top", {"start": v(-376.7, 30.5) * mm, "end": v(-371.5, 30.5) * mm});
            skLineSegment(sketch, "E289.MirrorCS", {"start": v(-366.5, 134.5) * mm, "end": v(-366.5, 82.5) * mm});
            skLineSegment(sketch, "E290.MirrorCS", {"start": v(-361.3, 134.5) * mm, "end": v(-361.3, 82.5) * mm});
            skLineSegment(sketch, "E291", {"start": v(-366.5, 186.5) * mm, "end": v(-366.5, 212.5) * mm});
            skLineSegment(sketch, "E292", {"start": v(-361.3, 186.5) * mm, "end": v(-361.3, 212.5) * mm});
            skLineSegment(sketch, "E293.MirrorCS", {"start": v(-361.3, 30.5) * mm, "end": v(-361.3, 4.5) * mm});
            skLineSegment(sketch, "E294.MirrorCS", {"start": v(-366.5, 30.5) * mm, "end": v(-366.5, 4.5) * mm});
            skLineSegment(sketch, "E295.bottom", {"start": v(-366.5, 30.5) * mm, "end": v(-361.3, 30.5) * mm});
            skLineSegment(sketch, "E295.top", {"start": v(-366.5, 4.5) * mm, "end": v(-361.3, 4.5) * mm});
            skLineSegment(sketch, "E296.trimOffspring", {"start": v(-366.5, 186.5) * mm, "end": v(-361.3, 186.5) * mm});
            skPoint(sketch, "E297.start.orphan", {"position": v(-369, 134.5) * mm});
            skPoint(sketch, "E298.orphan", {"position": v(-366.5, 134.5) * mm});
            skLineSegment(sketch, "E299.trimOffspring", {"start": v(-371.5, 134.5) * mm, "end": v(-376.7, 134.5) * mm});
            skLineSegment(sketch, "E300.trimOffspring", {"start": v(-371.5, 82.5) * mm, "end": v(-376.7, 82.5) * mm});
            skPoint(sketch, "E246.right.start.orphan", {"position": v(-350.34, 239.1) * mm});
            skLineSegment(sketch, "E301.bottom", {"start": v(-350.04, -21.5) * mm, "end": v(-344.01, -21.5) * mm});
            skLineSegment(sketch, "E302.bottom", {"start": v(-350.34, 239.1) * mm, "end": v(-344.84, 239.1) * mm});
            skLineSegment(sketch, "E302.left", {"start": v(-350.34, 239.1) * mm, "end": v(-350.34, 244.8) * mm});
            skLineSegment(sketch, "E303.left", {"start": v(-398.67, 239.1) * mm, "end": v(-398.67, 244.8) * mm});
            skLineSegment(sketch, "E304.top", {"start": v(-398.67, -27.82) * mm, "end": v(-392.34, -27.82) * mm});
            skLineSegment(sketch, "E304.left", {"start": v(-398.67, -21.5) * mm, "end": v(-398.67, -27.82) * mm});
            skLineSegment(sketch, "E305", {"start": v(-398.67, 200.43) * mm, "end": v(-398.67, 173.83) * mm});
            skLineSegment(sketch, "E306", {"start": v(-396.17, 173.83) * mm, "end": v(-394.67, 173.83) * mm});
            skLineSegment(sketch, "E307.bottom", {"start": v(-396.17, 200.43) * mm, "end": v(-394.67, 200.43) * mm});
            skLineSegment(sketch, "E307.right", {"start": v(-394.67, 200.43) * mm, "end": v(-394.67, 198.93) * mm});
            skCircle(sketch, "E308", {"center": v(-394.67, 173.83) * mm, "radius": 1.5 * mm});
            skCircle(sketch, "E309", {"center": v(-394.67, 200.43) * mm, "radius": 1.5 * mm});
            skCircle(sketch, "E310.MirrorC", {"center": v(-394.67, 16.59) * mm, "radius": 1.5 * mm});
            skCircle(sketch, "E311.MirrorC", {"center": v(-394.67, 43.19) * mm, "radius": 1.5 * mm});
            skLineSegment(sketch, "E312.trimOffspring", {"start": v(-394.67, 175.33) * mm, "end": v(-394.67, 173.83) * mm});
            skLineSegment(sketch, "E313.bottom", {"start": v(-215.7, 439.34) * mm, "end": v(-195.7, 439.34) * mm});
            skLineSegment(sketch, "E313.top", {"start": v(-215.7, 699.34) * mm, "end": v(-195.7, 699.34) * mm});
            skLineSegment(sketch, "E313.left", {"start": v(-235.7, 439.34) * mm, "end": v(-235.7, 465.34) * mm});
            skLineSegment(sketch, "E313.right", {"start": v(-115.7, 439.34) * mm, "end": v(-115.7, 465.34) * mm});
            skLineSegment(sketch, "E314.0", {"start": v(-235.7, 705.67) * mm, "end": v(-215.7, 705.67) * mm});
            skLineSegment(sketch, "E314.1", {"start": v(-242.03, 465.34) * mm, "end": v(-242.03, 491.34) * mm});
            skLineSegment(sketch, "E314.2", {"start": v(-235.7, 433.01) * mm, "end": v(-215.7, 433.01) * mm});
            skLineSegment(sketch, "E315.bottom", {"start": v(-115.7, 699.34) * mm, "end": v(-109.37, 699.34) * mm});
            skLineSegment(sketch, "E316.top", {"start": v(-109.37, 439.34) * mm, "end": v(-115.7, 439.34) * mm});
            skLineSegment(sketch, "E317.top", {"start": v(-242.03, 439.34) * mm, "end": v(-235.7, 439.34) * mm});
            skLineSegment(sketch, "E318", {"start": v(-175.7, 699.34) * mm, "end": v(-175.7, 705.67) * mm});
            skLineSegment(sketch, "E319", {"start": v(-175.7, 705.67) * mm, "end": v(-195.7, 705.67) * mm});
            skLineSegment(sketch, "E320", {"start": v(-195.7, 705.67) * mm, "end": v(-195.7, 699.34) * mm});
            skLineSegment(sketch, "E321", {"start": v(-215.7, 705.67) * mm, "end": v(-215.7, 699.34) * mm});
            skLineSegment(sketch, "E322.trimOffspring", {"start": v(-215.7, 705.67) * mm, "end": v(-235.7, 705.67) * mm});
            skLineSegment(sketch, "E323.trimOffspring", {"start": v(-195.7, 705.67) * mm, "end": v(-155.7, 705.67) * mm});
            skLineSegment(sketch, "E324", {"start": v(-242.03, 595.34) * mm, "end": v(-242.03, 621.34) * mm});
            skLineSegment(sketch, "E325", {"start": v(-242.03, 647.34) * mm, "end": v(-242.03, 673.34) * mm});
            skLineSegment(sketch, "E326", {"start": v(-242.03, 673.34) * mm, "end": v(-235.7, 673.34) * mm});
            skLineSegment(sketch, "E327", {"start": v(-242.03, 647.34) * mm, "end": v(-235.7, 647.34) * mm});
            skLineSegment(sketch, "E328", {"start": v(-242.03, 621.34) * mm, "end": v(-235.7, 621.34) * mm});
            skLineSegment(sketch, "E329", {"start": v(-242.03, 595.34) * mm, "end": v(-235.7, 595.34) * mm});
            skPoint(sketch, "E330.end.orphan", {"position": v(-242.03, 699.34) * mm});
            skLineSegment(sketch, "E331.bottom", {"start": v(-242.03, 699.34) * mm, "end": v(-235.7, 699.34) * mm});
            skLineSegment(sketch, "E331.top", {"start": v(-242.03, 705.67) * mm, "end": v(-235.7, 705.67) * mm});
            skLineSegment(sketch, "E331.left", {"start": v(-242.03, 699.34) * mm, "end": v(-242.03, 705.67) * mm});
            skLineSegment(sketch, "E332.MirrorCS", {"start": v(-242.03, 543.34) * mm, "end": v(-235.7, 543.34) * mm});
            skLineSegment(sketch, "E333.MirrorCS", {"start": v(-242.03, 543.34) * mm, "end": v(-242.03, 517.34) * mm});
            skLineSegment(sketch, "E334.MirrorCS", {"start": v(-242.03, 517.34) * mm, "end": v(-235.7, 517.34) * mm});
            skLineSegment(sketch, "E335.MirrorCS", {"start": v(-242.03, 491.34) * mm, "end": v(-235.7, 491.34) * mm});
            skLineSegment(sketch, "E336.MirrorCS", {"start": v(-242.03, 491.34) * mm, "end": v(-242.03, 465.34) * mm});
            skLineSegment(sketch, "E337.MirrorCS", {"start": v(-242.03, 465.34) * mm, "end": v(-235.7, 465.34) * mm});
            skLineSegment(sketch, "E338.trimOffspring", {"start": v(-242.03, 517.34) * mm, "end": v(-242.03, 543.34) * mm});
            skLineSegment(sketch, "E339.top", {"start": v(-242.03, 433.01) * mm, "end": v(-235.7, 433.01) * mm});
            skLineSegment(sketch, "E339.left", {"start": v(-242.03, 439.34) * mm, "end": v(-242.03, 433.01) * mm});
            skLineSegment(sketch, "E340.trimOffspring", {"start": v(-235.7, 491.34) * mm, "end": v(-235.7, 517.34) * mm});
            skLineSegment(sketch, "E341.trimOffspring", {"start": v(-235.7, 543.34) * mm, "end": v(-235.7, 595.34) * mm});
            skLineSegment(sketch, "E342.trimOffspring", {"start": v(-235.7, 621.34) * mm, "end": v(-235.7, 647.34) * mm});
            skLineSegment(sketch, "E343.trimOffspring", {"start": v(-235.7, 673.34) * mm, "end": v(-235.7, 699.34) * mm});
            skLineSegment(sketch, "E344.trimOffspring", {"start": v(-155.7, 699.34) * mm, "end": v(-135.7, 699.34) * mm});
            skLineSegment(sketch, "E345.MirrorCS", {"start": v(-215.7, 433.01) * mm, "end": v(-215.7, 439.34) * mm});
            skLineSegment(sketch, "E346.MirrorCS", {"start": v(-195.7, 433.01) * mm, "end": v(-195.7, 439.34) * mm});
            skLineSegment(sketch, "E347.MirrorCS", {"start": v(-155.7, 705.67) * mm, "end": v(-155.7, 699.34) * mm});
            skLineSegment(sketch, "E348.MirrorCS", {"start": v(-135.7, 705.67) * mm, "end": v(-135.7, 699.34) * mm});
            skLineSegment(sketch, "E349.MirrorCS", {"start": v(-109.37, 699.34) * mm, "end": v(-115.7, 699.34) * mm});
            skLineSegment(sketch, "E350.MirrorCS", {"start": v(-109.37, 699.34) * mm, "end": v(-109.37, 705.67) * mm});
            skLineSegment(sketch, "E351.MirrorCS", {"start": v(-109.37, 705.67) * mm, "end": v(-115.7, 705.67) * mm});
            skLineSegment(sketch, "E352.MirrorCS", {"start": v(-109.37, 439.34) * mm, "end": v(-109.37, 433.01) * mm});
            skLineSegment(sketch, "E353.MirrorCS", {"start": v(-109.37, 517.34) * mm, "end": v(-115.7, 517.34) * mm});
            skLineSegment(sketch, "E354.MirrorCS", {"start": v(-109.37, 491.34) * mm, "end": v(-115.7, 491.34) * mm});
            skLineSegment(sketch, "E355.MirrorCS", {"start": v(-109.37, 595.34) * mm, "end": v(-115.7, 595.34) * mm});
            skLineSegment(sketch, "E356.MirrorCS", {"start": v(-109.37, 673.34) * mm, "end": v(-115.7, 673.34) * mm});
            skLineSegment(sketch, "E357.MirrorCS", {"start": v(-109.37, 647.34) * mm, "end": v(-115.7, 647.34) * mm});
            skLineSegment(sketch, "E358.MirrorCS", {"start": v(-109.37, 465.34) * mm, "end": v(-115.7, 465.34) * mm});
            skLineSegment(sketch, "E359.MirrorCS", {"start": v(-109.37, 543.34) * mm, "end": v(-115.7, 543.34) * mm});
            skLineSegment(sketch, "E360.MirrorCS", {"start": v(-109.37, 621.34) * mm, "end": v(-115.7, 621.34) * mm});
            skLineSegment(sketch, "E361.MirrorCS", {"start": v(-109.37, 433.01) * mm, "end": v(-115.7, 433.01) * mm});
            skLineSegment(sketch, "E362.MirrorCS", {"start": v(-109.37, 543.34) * mm, "end": v(-109.37, 517.34) * mm});
            skLineSegment(sketch, "E363.MirrorCS", {"start": v(-109.37, 647.34) * mm, "end": v(-109.37, 673.34) * mm});
            skLineSegment(sketch, "E364.MirrorCS", {"start": v(-109.37, 595.34) * mm, "end": v(-109.37, 621.34) * mm});
            skLineSegment(sketch, "E365.MirrorCS", {"start": v(-109.37, 491.34) * mm, "end": v(-109.37, 465.34) * mm});
            skLineSegment(sketch, "E366.MirrorCS", {"start": v(-115.7, 673.34) * mm, "end": v(-115.7, 699.34) * mm});
            skPoint(sketch, "E367.MirrorP", {"position": v(-109.37, 699.34) * mm});
            skLineSegment(sketch, "E368.MirrorCS", {"start": v(-109.37, 517.34) * mm, "end": v(-109.37, 543.34) * mm});
            skLineSegment(sketch, "E369.MirrorCS", {"start": v(-115.7, 621.34) * mm, "end": v(-115.7, 647.34) * mm});
            skLineSegment(sketch, "E370.MirrorCS", {"start": v(-115.7, 543.34) * mm, "end": v(-115.7, 595.34) * mm});
            skLineSegment(sketch, "E371.MirrorCS", {"start": v(-115.7, 491.34) * mm, "end": v(-115.7, 517.34) * mm});
            skLineSegment(sketch, "E372.MirrorCS", {"start": v(-109.37, 465.34) * mm, "end": v(-109.37, 491.34) * mm});
            skLineSegment(sketch, "E373.MirrorCS", {"start": v(-135.7, 439.34) * mm, "end": v(-155.7, 439.34) * mm});
            skLineSegment(sketch, "E374.MirrorCS", {"start": v(-135.7, 433.01) * mm, "end": v(-135.7, 439.34) * mm});
            skLineSegment(sketch, "E375.MirrorCS", {"start": v(-155.7, 433.01) * mm, "end": v(-155.7, 439.34) * mm});
            skLineSegment(sketch, "E376.trimOffspring", {"start": v(-135.7, 705.67) * mm, "end": v(-115.7, 705.67) * mm});
            skPoint(sketch, "E377.MirrorCS.end.orphan", {"position": v(-115.7, 569.34) * mm});
            skPoint(sketch, "E377.MirrorCS.start.orphan", {"position": v(-109.37, 569.34) * mm});
            skLineSegment(sketch, "E378.trimOffspring", {"start": v(-195.7, 433.01) * mm, "end": v(-155.7, 433.01) * mm});
            skLineSegment(sketch, "E379.trimOffspring", {"start": v(-135.7, 433.01) * mm, "end": v(-115.7, 433.01) * mm});
            skLineSegment(sketch, "E380.trimOffspring", {"start": v(-155.7, 439.34) * mm, "end": v(-135.7, 439.34) * mm});
            skPoint(sketch, "E381.start.orphan", {"position": v(-242.03, 569.34) * mm});
            skLineSegment(sketch, "E382.bottom", {"start": v(-582.7, 704.73) * mm, "end": v(-447.7, 704.73) * mm});
            skLineSegment(sketch, "E382.top", {"start": v(-582.7, 432.07) * mm, "end": v(-447.7, 432.07) * mm});
            skLineSegment(sketch, "E382.left", {"start": v(-582.7, 704.73) * mm, "end": v(-582.7, 432.07) * mm});
            skLineSegment(sketch, "E382.right", {"start": v(-447.7, 704.73) * mm, "end": v(-447.7, 432.07) * mm});
            skLineSegment(sketch, "E383", {"start": v(-582.7, 704.73) * mm, "end": v(-582.7, 660.32) * mm});
            skLineSegment(sketch, "E384", {"start": v(-579.2, 660.32) * mm, "end": v(-577.7, 660.32) * mm});
            skLineSegment(sketch, "E385", {"start": v(-577.7, 660.32) * mm, "end": v(-577.7, 658.82) * mm});
            skCircle(sketch, "E386", {"center": v(-577.7, 660.32) * mm, "radius": 1.5 * mm});
            skLineSegment(sketch, "E387", {"start": v(-447.7, 568.4) * mm, "end": v(-486.35, 568.4) * mm});
            skCircle(sketch, "E388.MirrorC", {"center": v(-577.7, 476.48) * mm, "radius": 1.5 * mm});
            skCircle(sketch, "E389.MirrorC", {"center": v(-577.4, 503.13) * mm, "radius": 1.5 * mm});
            skCircle(sketch, "E390", {"center": v(-577.7, 633.72) * mm, "radius": 1.5 * mm});
            skLineSegment(sketch, "E391.trimOffspring", {"start": v(-577.7, 635.22) * mm, "end": v(-577.7, 633.72) * mm});
            skLineSegment(sketch, "E392.bottom", {"start": v(-931.6, 545.07) * mm, "end": v(-906.1, 545.07) * mm});
            skLineSegment(sketch, "E392.top", {"start": v(-931.6, 525.07) * mm, "end": v(-906.1, 525.07) * mm});
            skLineSegment(sketch, "E392.left", {"start": v(-931.6, 545.07) * mm, "end": v(-931.6, 525.07) * mm});
            skPoint(sketch, "E393.endSnap0", {"position": v(-911.6, 525.07) * mm});
            skLineSegment(sketch, "E394", {"start": v(-906.1, 540.07) * mm, "end": v(-911.6, 540.07) * mm});
            skLineSegment(sketch, "E395", {"start": v(-911.6, 540.07) * mm, "end": v(-911.6, 535.07) * mm});
            skLineSegment(sketch, "E396", {"start": v(-906.1, 530.07) * mm, "end": v(-911.6, 530.07) * mm});
            skLineSegment(sketch, "E397", {"start": v(-911.6, 530.07) * mm, "end": v(-911.6, 535.07) * mm});
            skLineSegment(sketch, "E398", {"start": v(-911.6, 540.07) * mm, "end": v(-911.6, 530.07) * mm});
            skLineSegment(sketch, "E399", {"start": v(-906.1, 545.07) * mm, "end": v(-906.1, 540.07) * mm});
            skLineSegment(sketch, "E400.trimOffspring", {"start": v(-906.1, 530.07) * mm, "end": v(-906.1, 525.07) * mm});
            skPoint(sketch, "E401.end.orphan", {"position": v(-911.6, 545.07) * mm});
            skPoint(sketch, "E402.orphan", {"position": v(-891.6, 540.07) * mm});
            skPoint(sketch, "E403.orphan", {"position": v(-891.6, 530.07) * mm});
            skLineSegment(sketch, "E404.bottom", {"start": v(-913.21, 509.65) * mm, "end": v(-899.54, 509.65) * mm});
            skLineSegment(sketch, "E404.top", {"start": v(-913.21, 489.65) * mm, "end": v(-899.54, 489.65) * mm});
            skLineSegment(sketch, "E404.right", {"start": v(-899.54, 509.65) * mm, "end": v(-899.54, 489.65) * mm});
            skPoint(sketch, "E405.endSnap0", {"position": v(-919.54, 489.65) * mm});
            skLineSegment(sketch, "E406", {"start": v(-899.54, 499.65) * mm, "end": v(-899.54, 509.65) * mm});
            skLineSegment(sketch, "E407", {"start": v(-913.21, 504.65) * mm, "end": v(-919.54, 504.65) * mm});
            skLineSegment(sketch, "E408", {"start": v(-919.54, 504.65) * mm, "end": v(-919.54, 498.65) * mm});
            skLineSegment(sketch, "E409", {"start": v(-899.54, 499.65) * mm, "end": v(-899.54, 489.65) * mm});
            skLineSegment(sketch, "E410", {"start": v(-919.54, 493.65) * mm, "end": v(-919.54, 498.65) * mm});
            skLineSegment(sketch, "E411", {"start": v(-919.54, 504.65) * mm, "end": v(-919.54, 493.65) * mm});
            skLineSegment(sketch, "E412", {"start": v(-913.21, 509.65) * mm, "end": v(-913.21, 504.65) * mm});
            skLineSegment(sketch, "E413.trimOffspring", {"start": v(-913.21, 493.65) * mm, "end": v(-913.21, 489.65) * mm});
            skPoint(sketch, "E414.end.orphan", {"position": v(-919.54, 509.65) * mm});
            skPoint(sketch, "E415.orphan", {"position": v(-899.54, 504.65) * mm});
            skPoint(sketch, "E416.orphan", {"position": v(-899.54, 494.65) * mm});
            skPoint(sketch, "E404.left.start.orphan", {"position": v(-939.54, 509.65) * mm});
            skPoint(sketch, "E417.orphan", {"position": v(-939.54, 489.65) * mm});
            skPoint(sketch, "E418.orphan", {"position": v(-891.6, 535.07) * mm});
            skPoint(sketch, "E419.orphan", {"position": v(-891.6, 545.07) * mm});
            skPoint(sketch, "E392.right.end.orphan", {"position": v(-891.6, 525.07) * mm});
            skText(sketch, "E420", { "text": "11", "fontName": "OpenSans-Regular.ttf"});
            skLineSegment(sketch, "E421.bottom", {"start": v(-861.08, 507.95) * mm, "end": v(-847.41, 507.95) * mm});
            skLineSegment(sketch, "E421.top", {"start": v(-861.08, 487.95) * mm, "end": v(-847.41, 487.95) * mm});
            skLineSegment(sketch, "E421.right", {"start": v(-847.41, 507.95) * mm, "end": v(-847.41, 487.95) * mm});
            skPoint(sketch, "E422.endSnap0", {"position": v(-867.41, 487.95) * mm});
            skLineSegment(sketch, "E423", {"start": v(-847.41, 497.95) * mm, "end": v(-847.41, 507.95) * mm});
            skLineSegment(sketch, "E424", {"start": v(-861.08, 502.95) * mm, "end": v(-867.41, 502.95) * mm});
            skLineSegment(sketch, "E425", {"start": v(-867.41, 502.95) * mm, "end": v(-867.41, 496.35) * mm});
            skLineSegment(sketch, "E426", {"start": v(-847.41, 497.95) * mm, "end": v(-847.41, 487.95) * mm});
            skLineSegment(sketch, "E427", {"start": v(-867.41, 491.35) * mm, "end": v(-867.41, 496.35) * mm});
            skLineSegment(sketch, "E428", {"start": v(-867.41, 502.95) * mm, "end": v(-867.41, 491.35) * mm});
            skLineSegment(sketch, "E429", {"start": v(-861.08, 507.95) * mm, "end": v(-861.08, 502.95) * mm});
            skLineSegment(sketch, "E430.trimOffspring", {"start": v(-861.08, 491.35) * mm, "end": v(-861.08, 487.95) * mm});
            skPoint(sketch, "E431.end.orphan", {"position": v(-867.41, 507.95) * mm});
            skPoint(sketch, "E432.orphan", {"position": v(-847.41, 502.95) * mm});
            skPoint(sketch, "E433.orphan", {"position": v(-847.41, 492.95) * mm});
            skLineSegment(sketch, "E434.top", {"start": v(-861.08, 491.35) * mm, "end": v(-867.41, 491.35) * mm});
            skText(sketch, "E435", { "text": "11.6", "fontName": "OpenSans-Regular.ttf"});
            skLineSegment(sketch, "E436.top", {"start": v(-913.21, 493.65) * mm, "end": v(-919.54, 493.65) * mm});
            skLineSegment(sketch, "E437.bottom", {"start": v(-868.91, 547.7) * mm, "end": v(-854.41, 547.7) * mm});
            skLineSegment(sketch, "E437.top", {"start": v(-868.91, 527.7) * mm, "end": v(-854.41, 527.7) * mm});
            skLineSegment(sketch, "E437.right", {"start": v(-854.41, 547.7) * mm, "end": v(-854.41, 527.7) * mm});
            skPoint(sketch, "E438.endSnap0", {"position": v(-874.41, 527.7) * mm});
            skLineSegment(sketch, "E439", {"start": v(-854.41, 537.7) * mm, "end": v(-854.41, 547.7) * mm});
            skLineSegment(sketch, "E440", {"start": v(-868.91, 542.7) * mm, "end": v(-874.41, 542.7) * mm});
            skLineSegment(sketch, "E441", {"start": v(-874.41, 542.7) * mm, "end": v(-874.41, 536.7) * mm});
            skLineSegment(sketch, "E442", {"start": v(-854.41, 537.7) * mm, "end": v(-854.41, 527.7) * mm});
            skLineSegment(sketch, "E443", {"start": v(-874.41, 532.1) * mm, "end": v(-874.41, 536.7) * mm});
            skLineSegment(sketch, "E444", {"start": v(-874.41, 542.7) * mm, "end": v(-874.41, 532.1) * mm});
            skLineSegment(sketch, "E445", {"start": v(-868.91, 547.7) * mm, "end": v(-868.91, 542.7) * mm});
            skLineSegment(sketch, "E446.trimOffspring", {"start": v(-868.91, 532.1) * mm, "end": v(-868.91, 527.7) * mm});
            skPoint(sketch, "E447.end.orphan", {"position": v(-874.41, 547.7) * mm});
            skPoint(sketch, "E448.orphan", {"position": v(-854.41, 542.7) * mm});
            skPoint(sketch, "E449.orphan", {"position": v(-854.41, 532.7) * mm});
            skLineSegment(sketch, "E450.top", {"start": v(-868.91, 532.1) * mm, "end": v(-874.41, 532.1) * mm});
            skLineSegment(sketch, "E451", {"start": v(-398.67, 244.8) * mm, "end": v(-378.34, 244.8) * mm});
            skLineSegment(sketch, "E452.trimOffspring", {"start": v(-364.34, 244.8) * mm, "end": v(-350.34, 244.8) * mm});
            skLineSegment(sketch, "E453", {"start": v(-344.84, 239.1) * mm, "end": v(-344.84, 212.5) * mm});
            skLineSegment(sketch, "E454", {"start": v(-45.5, 214.67) * mm, "end": v(-45.5, 209.17) * mm});
            skLineSegment(sketch, "E455", {"start": v(80, 298.4) * mm, "end": v(85.5, 298.4) * mm});
            skLineSegment(sketch, "E456", {"start": v(85.5, 278.37) * mm, "end": v(85.5, 243.74) * mm});
            skLineSegment(sketch, "E457", {"start": v(60.3, 244.57) * mm, "end": v(39.7, 244.57) * mm});
            skLineSegment(sketch, "E458", {"start": v(-45.5, 263.77) * mm, "end": v(-45.5, 278.37) * mm});
            skLineSegment(sketch, "E459", {"start": v(-155.06, 215.5) * mm, "end": v(-155.06, 182.87) * mm});
            skPoint(sketch, "E460.trimOffspring.end.orphan", {"position": v(-344.01, 239.1) * mm});
            skLineSegment(sketch, "E461", {"start": v(-344.01, 186.5) * mm, "end": v(-344.01, 186.8) * mm});
            skLineSegment(sketch, "E462", {"start": v(-344.01, 186.8) * mm, "end": v(-350.34, 186.8) * mm});
            skLineSegment(sketch, "E463", {"start": v(-344.01, 159.9) * mm, "end": v(-344.01, 159.6) * mm});
            skLineSegment(sketch, "E464", {"start": v(-344.01, 159.6) * mm, "end": v(-350.34, 159.6) * mm});
            skLineSegment(sketch, "E465", {"start": v(-344.01, 134.5) * mm, "end": v(-344.01, 134.8) * mm});
            skLineSegment(sketch, "E466", {"start": v(-344.01, 134.8) * mm, "end": v(-350.34, 134.8) * mm});
            skLineSegment(sketch, "E467", {"start": v(-344.01, 82.5) * mm, "end": v(-344.01, 82.2) * mm});
            skLineSegment(sketch, "E468", {"start": v(-344.01, 82.2) * mm, "end": v(-350.34, 82.2) * mm});
            skLineSegment(sketch, "E469", {"start": v(-344.01, 56.5) * mm, "end": v(-344.01, 56.8) * mm});
            skLineSegment(sketch, "E470", {"start": v(-344.01, 56.8) * mm, "end": v(-350.34, 56.8) * mm});
            skLineSegment(sketch, "E471", {"start": v(-344.01, 30.5) * mm, "end": v(-344.01, 30.2) * mm});
            skLineSegment(sketch, "E472", {"start": v(-344.01, 30.2) * mm, "end": v(-350.34, 30.2) * mm});
            skLineSegment(sketch, "E473", {"start": v(-344.01, 4.5) * mm, "end": v(-344.01, 4.8) * mm});
            skLineSegment(sketch, "E474", {"start": v(-344.01, 4.8) * mm, "end": v(-350.34, 4.8) * mm});
            skLineSegment(sketch, "E475", {"start": v(-350.34, -27.82) * mm, "end": v(-350.04, -27.82) * mm});
            skLineSegment(sketch, "E476", {"start": v(-350.04, -27.82) * mm, "end": v(-350.04, -21.5) * mm});
            skLineSegment(sketch, "E477", {"start": v(-357.34, -27.82) * mm, "end": v(-357.34, -28.58) * mm});
            skLineSegment(sketch, "E478.MirrorCS", {"start": v(-364.64, -27.82) * mm, "end": v(-364.64, -21.5) * mm});
            skLineSegment(sketch, "E479.MirrorCS", {"start": v(-364.34, -27.82) * mm, "end": v(-364.64, -27.82) * mm});
            skLineSegment(sketch, "E480.MirrorCS", {"start": v(-364.64, 244.84) * mm, "end": v(-364.64, 238.5) * mm});
            skLineSegment(sketch, "E481.MirrorCS", {"start": v(-350.04, 244.84) * mm, "end": v(-350.04, 238.5) * mm});
            skLineSegment(sketch, "E482.MirrorCS", {"start": v(-364.34, 244.84) * mm, "end": v(-364.64, 244.84) * mm});
            skLineSegment(sketch, "E483.MirrorCS", {"start": v(-350.34, 244.84) * mm, "end": v(-350.04, 244.84) * mm});
            skLineSegment(sketch, "E484", {"start": v(-154.23, 209.17) * mm, "end": v(-154.23, 209.47) * mm});
            skLineSegment(sketch, "E485", {"start": v(-155.06, 209.47) * mm, "end": v(-160.26, 209.47) * mm});
            skLineSegment(sketch, "E486", {"start": v(-154.23, 183.17) * mm, "end": v(-154.23, 182.87) * mm});
            skLineSegment(sketch, "E487", {"start": v(-154.23, 182.87) * mm, "end": v(-155.06, 182.87) * mm});
            skLineSegment(sketch, "E488", {"start": v(-154.23, 157.17) * mm, "end": v(-154.23, 157.47) * mm});
            skLineSegment(sketch, "E489", {"start": v(-154.23, 131.17) * mm, "end": v(-154.23, 130.87) * mm});
            skLineSegment(sketch, "E490", {"start": v(-154.23, 105.17) * mm, "end": v(-154.23, 105.47) * mm});
            skLineSegment(sketch, "E491", {"start": v(0, 215.5) * mm, "end": v(-0.3, 215.5) * mm});
            skLineSegment(sketch, "E492.bottom", {"start": v(-0.3, 215.5) * mm, "end": v(0, 215.5) * mm});
            skLineSegment(sketch, "E492.left", {"start": v(-0.3, 214.67) * mm, "end": v(-0.3, 209.17) * mm});
            skLineSegment(sketch, "E493", {"start": v(-19.7, 214.67) * mm, "end": v(-19.7, 209.17) * mm});
            skLineSegment(sketch, "E494", {"start": v(-45.5, 183.47) * mm, "end": v(-40, 183.47) * mm});
            skLineSegment(sketch, "E495", {"start": v(-46.33, 157.17) * mm, "end": v(-46.33, 156.87) * mm});
            skLineSegment(sketch, "E496", {"start": v(-45.5, 156.87) * mm, "end": v(-40, 156.87) * mm});
            skLineSegment(sketch, "E497", {"start": v(-45.5, 131.47) * mm, "end": v(-40, 131.47) * mm});
            skLineSegment(sketch, "E498", {"start": v(-45.5, 104.87) * mm, "end": v(-40, 104.87) * mm});
            skLineSegment(sketch, "E499.trimOffspring", {"start": v(20, 214.67) * mm, "end": v(-0.3, 214.67) * mm});
            skLineSegment(sketch, "E500.trimOffspring", {"start": v(-19.7, 214.67) * mm, "end": v(-45.5, 214.67) * mm});
            skPoint(sketch, "E501.end.orphan", {"position": v(-20, 209.17) * mm});
            skLineSegment(sketch, "E502.trimOffspring", {"start": v(-45.5, 183.47) * mm, "end": v(-45.5, 156.87) * mm});
            skLineSegment(sketch, "E503.trimOffspring", {"start": v(-45.5, 131.47) * mm, "end": v(-45.5, 104.87) * mm});
            skPoint(sketch, "E504.orphan", {"position": v(-40, 157.17) * mm});
            skPoint(sketch, "E505.orphan", {"position": v(-40, 131.17) * mm});
            skPoint(sketch, "E506.orphan", {"position": v(20, 215.5) * mm});
            skPoint(sketch, "E507.start.orphan", {"position": v(-46.33, 183.17) * mm});
            skPoint(sketch, "E508.trimOffspring.end.orphan", {"position": v(-46.33, 131.17) * mm});
            skPoint(sketch, "E509.start.orphan", {"position": v(-46.33, 105.17) * mm});
            skLineSegment(sketch, "E510.MirrorCS", {"start": v(40, 215.5) * mm, "end": v(40.3, 215.5) * mm});
            skLineSegment(sketch, "E511.MirrorCS", {"start": v(40.3, 215.5) * mm, "end": v(40, 215.5) * mm});
            skLineSegment(sketch, "E512.MirrorCS", {"start": v(85.5, 156.87) * mm, "end": v(80, 156.87) * mm});
            skLineSegment(sketch, "E513.MirrorCS", {"start": v(86.33, 157.17) * mm, "end": v(86.33, 156.87) * mm});
            skLineSegment(sketch, "E514.MirrorCS", {"start": v(85.5, 131.47) * mm, "end": v(80, 131.47) * mm});
            skLineSegment(sketch, "E515.MirrorCS", {"start": v(85.5, 214.67) * mm, "end": v(85.5, 209.17) * mm});
            skLineSegment(sketch, "E516.MirrorCS", {"start": v(40.3, 214.67) * mm, "end": v(40.3, 209.17) * mm});
            skLineSegment(sketch, "E517.MirrorCS", {"start": v(85.5, 209.17) * mm, "end": v(80, 209.17) * mm});
            skLineSegment(sketch, "E518.MirrorCS", {"start": v(85.5, 104.87) * mm, "end": v(80, 104.87) * mm});
            skLineSegment(sketch, "E519.MirrorCS", {"start": v(85.5, 183.47) * mm, "end": v(80, 183.47) * mm});
            skLineSegment(sketch, "E520.MirrorCS", {"start": v(59.7, 214.67) * mm, "end": v(59.7, 209.17) * mm});
            skLineSegment(sketch, "E521.MirrorCS", {"start": v(80, 183.47) * mm, "end": v(80, 209.17) * mm});
            skLineSegment(sketch, "E522.MirrorCS", {"start": v(59.7, 214.67) * mm, "end": v(85.5, 214.67) * mm});
            skPoint(sketch, "E523.MirrorP", {"position": v(86.33, 131.17) * mm});
            skPoint(sketch, "E524.MirrorP", {"position": v(86.33, 105.17) * mm});
            skLineSegment(sketch, "E525.MirrorCS", {"start": v(85.5, 131.47) * mm, "end": v(85.5, 104.87) * mm});
            skPoint(sketch, "E526.MirrorP", {"position": v(86.33, 79.17) * mm});
            skPoint(sketch, "E527.MirrorP", {"position": v(86.33, 183.17) * mm});
            skPoint(sketch, "E528.MirrorP", {"position": v(60, 209.17) * mm});
            skLineSegment(sketch, "E529.MirrorCS", {"start": v(59.7, 209.17) * mm, "end": v(40.3, 209.17) * mm});
            skLineSegment(sketch, "E530.MirrorCS", {"start": v(20, 214.67) * mm, "end": v(40.3, 214.67) * mm});
            skPoint(sketch, "E531.MirrorP", {"position": v(80, 131.17) * mm});
            skPoint(sketch, "E532.MirrorP", {"position": v(80, 157.17) * mm});
            skPoint(sketch, "E533.MirrorP", {"position": v(86.33, 209.17) * mm});
            skLineSegment(sketch, "E534.MirrorCS", {"start": v(80, 131.47) * mm, "end": v(80, 156.87) * mm});
            skLineSegment(sketch, "E535.MirrorCS", {"start": v(80, 79.17) * mm, "end": v(80, 104.87) * mm});
            skLineSegment(sketch, "E536.MirrorCS", {"start": v(85.5, 183.47) * mm, "end": v(85.5, 156.87) * mm});
            skLineSegment(sketch, "E537.MirrorCS", {"start": v(40.3, -57.16) * mm, "end": v(40, -57.16) * mm});
            skLineSegment(sketch, "E538.MirrorCS", {"start": v(40, -57.16) * mm, "end": v(40.3, -57.16) * mm});
            skLineSegment(sketch, "E539.MirrorCS", {"start": v(86.33, 1.17) * mm, "end": v(86.33, 1.47) * mm});
            skLineSegment(sketch, "E540.MirrorCS", {"start": v(85.5, 26.87) * mm, "end": v(80, 26.87) * mm});
            skLineSegment(sketch, "E541.MirrorCS", {"start": v(85.5, 1.47) * mm, "end": v(80, 1.47) * mm});
            skLineSegment(sketch, "E542.MirrorCS", {"start": v(0, -57.16) * mm, "end": v(-0.3, -57.16) * mm});
            skLineSegment(sketch, "E543.MirrorCS", {"start": v(85.5, -50.83) * mm, "end": v(80, -50.83) * mm});
            skLineSegment(sketch, "E544.MirrorCS", {"start": v(40.3, -56.33) * mm, "end": v(40.3, -50.83) * mm});
            skLineSegment(sketch, "E545.MirrorCS", {"start": v(59.7, -56.33) * mm, "end": v(59.7, -50.83) * mm});
            skLineSegment(sketch, "E546.MirrorCS", {"start": v(85.5, 53.47) * mm, "end": v(80, 53.47) * mm});
            skLineSegment(sketch, "E547.MirrorCS", {"start": v(-0.3, -57.16) * mm, "end": v(0, -57.16) * mm});
            skLineSegment(sketch, "E548.MirrorCS", {"start": v(85.5, -25.13) * mm, "end": v(80, -25.13) * mm});
            skLineSegment(sketch, "E549.MirrorCS", {"start": v(85.5, -56.33) * mm, "end": v(85.5, -50.83) * mm});
            skLineSegment(sketch, "E550.MirrorCS", {"start": v(-46.33, 1.17) * mm, "end": v(-46.33, 1.47) * mm});
            skLineSegment(sketch, "E551.MirrorCS", {"start": v(-45.5, 1.47) * mm, "end": v(-40, 1.47) * mm});
            skLineSegment(sketch, "E552.MirrorCS", {"start": v(-45.5, 26.87) * mm, "end": v(-40, 26.87) * mm});
            skLineSegment(sketch, "E553.MirrorCS", {"start": v(-0.3, -56.33) * mm, "end": v(-0.3, -50.83) * mm});
            skLineSegment(sketch, "E554.MirrorCS", {"start": v(-45.5, -50.83) * mm, "end": v(-40, -50.83) * mm});
            skLineSegment(sketch, "E555.MirrorCS", {"start": v(-19.7, -56.33) * mm, "end": v(-19.7, -50.83) * mm});
            skPoint(sketch, "E556.MirrorP", {"position": v(20, -57.16) * mm});
            skLineSegment(sketch, "E557.MirrorCS", {"start": v(-45.5, 53.47) * mm, "end": v(-40, 53.47) * mm});
            skLineSegment(sketch, "E558.MirrorCS", {"start": v(-45.5, -25.13) * mm, "end": v(-40, -25.13) * mm});
            skLineSegment(sketch, "E559.MirrorCS", {"start": v(-45.5, -56.33) * mm, "end": v(-45.5, -50.83) * mm});
            skPoint(sketch, "E560.MirrorP", {"position": v(86.33, 27.17) * mm});
            skLineSegment(sketch, "E561.MirrorCS", {"start": v(20, -56.33) * mm, "end": v(40.3, -56.33) * mm});
            skLineSegment(sketch, "E562.MirrorCS", {"start": v(85.5, 26.87) * mm, "end": v(85.5, 53.47) * mm});
            skLineSegment(sketch, "E563.MirrorCS", {"start": v(85.5, -25.13) * mm, "end": v(85.5, 1.47) * mm});
            skLineSegment(sketch, "E564.MirrorCS", {"start": v(59.7, -50.83) * mm, "end": v(40.3, -50.83) * mm});
            skLineSegment(sketch, "E565.MirrorCS", {"start": v(80, -25.13) * mm, "end": v(80, -50.83) * mm});
            skLineSegment(sketch, "E566.MirrorCS", {"start": v(80, 26.87) * mm, "end": v(80, 1.47) * mm});
            skPoint(sketch, "E567.MirrorP", {"position": v(86.33, -50.83) * mm});
            skPoint(sketch, "E568.MirrorP", {"position": v(60, -50.83) * mm});
            skPoint(sketch, "E569.MirrorP", {"position": v(86.33, 53.17) * mm});
            skPoint(sketch, "E570.MirrorP", {"position": v(86.33, -24.83) * mm});
            skLineSegment(sketch, "E571.MirrorCS", {"start": v(59.7, -56.33) * mm, "end": v(85.5, -56.33) * mm});
            skLineSegment(sketch, "E572.MirrorCS", {"start": v(80, 79.17) * mm, "end": v(80, 53.47) * mm});
            skPoint(sketch, "E573.MirrorP", {"position": v(80, 27.17) * mm});
            skPoint(sketch, "E574.MirrorP", {"position": v(80, 1.17) * mm});
            skLineSegment(sketch, "E575.MirrorCS", {"start": v(20, -56.33) * mm, "end": v(-0.3, -56.33) * mm});
            skLineSegment(sketch, "E576.MirrorCS", {"start": v(-40, 26.87) * mm, "end": v(-40, 1.47) * mm});
            skPoint(sketch, "E577.MirrorP", {"position": v(-46.33, 27.17) * mm});
            skLineSegment(sketch, "E578.MirrorCS", {"start": v(-45.5, 26.87) * mm, "end": v(-45.5, 53.47) * mm});
            skPoint(sketch, "E579.MirrorP", {"position": v(-46.33, -50.83) * mm});
            skPoint(sketch, "E580.MirrorP", {"position": v(-40, 27.17) * mm});
            skLineSegment(sketch, "E581.MirrorCS", {"start": v(-40, -25.13) * mm, "end": v(-40, -50.83) * mm});
            skLineSegment(sketch, "E582.MirrorCS", {"start": v(-19.7, -50.83) * mm, "end": v(-0.3, -50.83) * mm});
            skLineSegment(sketch, "E583.MirrorCS", {"start": v(-45.5, -25.13) * mm, "end": v(-45.5, 1.47) * mm});
            skLineSegment(sketch, "E584.MirrorCS", {"start": v(-40, 79.17) * mm, "end": v(-40, 53.47) * mm});
            skLineSegment(sketch, "E585.MirrorCS", {"start": v(-19.7, -56.33) * mm, "end": v(-45.5, -56.33) * mm});
            skPoint(sketch, "E586.MirrorP", {"position": v(-40, 1.17) * mm});
            skPoint(sketch, "E587.MirrorP", {"position": v(-46.33, 53.17) * mm});
            skPoint(sketch, "E588.MirrorP", {"position": v(-20, -50.83) * mm});
            skPoint(sketch, "E589.MirrorP", {"position": v(-46.33, -24.83) * mm});
            skPoint(sketch, "E590.MirrorCS.end.orphan", {"position": v(20, 79.17) * mm});
            skPoint(sketch, "E591.start.orphan", {"position": v(20, 209.17) * mm});
            skLineSegment(sketch, "E592", {"start": v(20, 250.07) * mm, "end": v(20, 258.6) * mm});
            skLineSegment(sketch, "E593.MirrorCS", {"start": v(40, 261.04) * mm, "end": v(40, 266.24) * mm});
            skLineSegment(sketch, "E594.MirrorCS", {"start": v(40, 271.24) * mm, "end": v(40, 276.44) * mm});
            skPoint(sketch, "E595.orphan", {"position": v(44.01, 250.07) * mm});
            skPoint(sketch, "E596.orphan", {"position": v(44.01, 261.04) * mm});
            skPoint(sketch, "E597.orphan", {"position": v(44.01, 266.24) * mm});
            skLineSegment(sketch, "E598", {"start": v(0, 266.24) * mm, "end": v(40, 266.24) * mm});
            skLineSegment(sketch, "E599", {"start": v(40, 271.24) * mm, "end": v(0, 271.24) * mm});
            skPoint(sketch, "E240.left.start.orphan", {"position": v(44.01, 271.24) * mm});
            skLineSegment(sketch, "E600", {"start": v(20, 250.07) * mm, "end": v(40, 250.07) * mm});
            skLineSegment(sketch, "E601", {"start": v(-45.5, 278.37) * mm, "end": v(-40, 278.37) * mm});
            skLineSegment(sketch, "E602", {"start": v(-46.33, 264.07) * mm, "end": v(-46.33, 263.77) * mm});
            skLineSegment(sketch, "E603", {"start": v(-45.5, 263.77) * mm, "end": v(-40, 263.77) * mm});
            skLineSegment(sketch, "E604", {"start": v(-20, 243.74) * mm, "end": v(-21.98, 243.74) * mm});
            skLineSegment(sketch, "E605.MirrorCS", {"start": v(86.33, 278.37) * mm, "end": v(80, 278.37) * mm});
            skLineSegment(sketch, "E606.MirrorCS", {"start": v(85.5, 263.77) * mm, "end": v(80, 263.77) * mm});
            skLineSegment(sketch, "E607", {"start": v(-20, 243.74) * mm, "end": v(-21.6, 243.74) * mm});
            skPoint(sketch, "E608.end.orphan", {"position": v(-46.33, 278.37) * mm});
            skPoint(sketch, "E609.orphan", {"position": v(-46.33, 278.07) * mm});
            skPoint(sketch, "E610.orphan", {"position": v(-40, 278.07) * mm});
            skPoint(sketch, "E611.orphan", {"position": v(-20.3, 243.74) * mm});
            skPoint(sketch, "E612.orphan", {"position": v(0.3, 243.74) * mm});
            skLineSegment(sketch, "E613.trimOffspring", {"start": v(0.3, 244.57) * mm, "end": v(-20.3, 244.57) * mm});
            skPoint(sketch, "E614.orphan", {"position": v(-10, 243.74) * mm});
            skPoint(sketch, "E615.orphan", {"position": v(0, 250.07) * mm});
            skPoint(sketch, "E616.MirrorCS.end.orphan", {"position": v(40, 243.74) * mm});
            skPoint(sketch, "E617.orphan", {"position": v(60, 243.74) * mm});
            skPoint(sketch, "E618.orphan", {"position": v(86.33, 263.77) * mm});
            skLineSegment(sketch, "E619", {"start": v(80, 278.37) * mm, "end": v(80, 292.07) * mm});
            skLineSegment(sketch, "E620", {"start": v(-174.86, 214.67) * mm, "end": v(-160.56, 214.67) * mm});
            skPoint(sketch, "E621.orphan", {"position": v(-174.56, 209.17) * mm});
            skPoint(sketch, "E622.orphan", {"position": v(-160.56, 183.17) * mm});
            skLineSegment(sketch, "E623.trimOffspring", {"start": v(-155.06, 157.47) * mm, "end": v(-155.06, 130.87) * mm});
            skPoint(sketch, "E624.orphan", {"position": v(-160.56, 157.17) * mm});
            skLineSegment(sketch, "E625", {"start": v(-136.78, 79.17) * mm, "end": v(-160.56, 79.17) * mm});
            skPoint(sketch, "E625.endSnap0", {"position": v(-186.93, 79.17) * mm});
            skLineSegment(sketch, "E626", {"start": v(-160.56, 214.67) * mm, "end": v(-160.26, 214.67) * mm});
            skLineSegment(sketch, "E627", {"start": v(-208.9, 209.17) * mm, "end": v(-208.9, 79.17) * mm});
            skLineSegment(sketch, "E628.MirrorCS", {"start": v(-160.56, -56.33) * mm, "end": v(-160.26, -56.33) * mm});
            skLineSegment(sketch, "E629.MirrorCS", {"start": v(-160.56, -56.33) * mm, "end": v(-160.56, -57.16) * mm});
            skLineSegment(sketch, "E630.MirrorCS", {"start": v(-186.93, -24.83) * mm, "end": v(-181.73, -24.83) * mm});
            skLineSegment(sketch, "E631.MirrorCS", {"start": v(-154.23, -24.83) * mm, "end": v(-154.23, -24.53) * mm});
            skLineSegment(sketch, "E632.MirrorCS", {"start": v(-184.73, -24.83) * mm, "end": v(-181.73, -24.83) * mm});
            skLineSegment(sketch, "E633.MirrorCS", {"start": v(-181.73, -24.83) * mm, "end": v(-186.93, -24.83) * mm});
            skLineSegment(sketch, "E634.MirrorCS", {"start": v(-154.23, -50.83) * mm, "end": v(-154.23, -51.13) * mm});
            skLineSegment(sketch, "E635.MirrorCS", {"start": v(-174.56, -57.16) * mm, "end": v(-174.86, -57.16) * mm});
            skLineSegment(sketch, "E636.MirrorCS", {"start": v(-154.23, 1.17) * mm, "end": v(-154.23, 0.87) * mm});
            skLineSegment(sketch, "E637.MirrorCS", {"start": v(-154.23, 27.17) * mm, "end": v(-154.23, 27.47) * mm});
            skLineSegment(sketch, "E638.MirrorCS", {"start": v(-154.23, 53.17) * mm, "end": v(-154.23, 52.87) * mm});
            skLineSegment(sketch, "E639.MirrorCS", {"start": v(-186.93, 1.17) * mm, "end": v(-181.73, 1.17) * mm});
            skLineSegment(sketch, "E640.MirrorCS", {"start": v(-208.9, -57.16) * mm, "end": v(-202.56, -57.16) * mm});
            skLineSegment(sketch, "E641.MirrorCS", {"start": v(-171.53, -24.83) * mm, "end": v(-176.73, -24.83) * mm});
            skLineSegment(sketch, "E642.MirrorCS", {"start": v(-208.9, -50.83) * mm, "end": v(-208.9, -57.16) * mm});
            skLineSegment(sketch, "E643.MirrorCS", {"start": v(-174.56, -57.16) * mm, "end": v(-160.56, -57.16) * mm});
            skLineSegment(sketch, "E644.MirrorCS", {"start": v(-176.73, 1.17) * mm, "end": v(-171.53, 1.17) * mm});
            skLineSegment(sketch, "E645.MirrorCS", {"start": v(-188.56, -57.16) * mm, "end": v(-188.56, -50.83) * mm});
            skLineSegment(sketch, "E646.MirrorCS", {"start": v(-160.56, 52.87) * mm, "end": v(-160.56, 27.47) * mm});
            skLineSegment(sketch, "E647.MirrorCS", {"start": v(-154.23, 27.17) * mm, "end": v(-154.23, 1.17) * mm});
            skLineSegment(sketch, "E648.MirrorCS", {"start": v(-208.9, -24.83) * mm, "end": v(-208.9, 1.17) * mm});
            skPoint(sketch, "E649.MirrorP", {"position": v(-174.56, -50.83) * mm});
            skPoint(sketch, "E650.MirrorP", {"position": v(-160.56, -50.83) * mm});
            skLineSegment(sketch, "E651.MirrorCS", {"start": v(-188.56, -50.83) * mm, "end": v(-181.56, -50.83) * mm});
            skLineSegment(sketch, "E652.MirrorCS", {"start": v(-188.56, -50.83) * mm, "end": v(-174.86, -50.83) * mm});
            skLineSegment(sketch, "E653.MirrorCS", {"start": v(-155.06, -57.16) * mm, "end": v(-155.06, -56.33) * mm});
            skLineSegment(sketch, "E654.MirrorCS", {"start": v(-176.73, 53.17) * mm, "end": v(-176.73, 105.17) * mm});
            skPoint(sketch, "E655.MirrorP", {"position": v(-160.56, -24.83) * mm});
            skLineSegment(sketch, "E656.MirrorCS", {"start": v(-186.93, 53.17) * mm, "end": v(-186.93, 105.17) * mm});
            skPoint(sketch, "E657.MirrorP", {"position": v(-160.56, 1.17) * mm});
            skLineSegment(sketch, "E658.MirrorCS", {"start": v(-174.86, -56.33) * mm, "end": v(-160.56, -56.33) * mm});
            skLineSegment(sketch, "E659.MirrorCS", {"start": v(-186.93, -24.83) * mm, "end": v(-186.93, 1.17) * mm});
            skPoint(sketch, "E660.MirrorP", {"position": v(-184.73, 1.17) * mm});
            skPoint(sketch, "E661.MirrorP", {"position": v(-176.73, 53.17) * mm});
            skLineSegment(sketch, "E662.MirrorCS", {"start": v(-181.73, 53.17) * mm, "end": v(-181.73, 105.17) * mm});
            skLineSegment(sketch, "E663.MirrorCS", {"start": v(-154.23, -24.83) * mm, "end": v(-154.23, -50.83) * mm});
            skPoint(sketch, "E664.MirrorP", {"position": v(-179.23, 53.17) * mm});
            skLineSegment(sketch, "E665.MirrorCS", {"start": v(-181.73, -24.83) * mm, "end": v(-181.73, 1.17) * mm});
            skLineSegment(sketch, "E666.MirrorCS", {"start": v(-171.53, 1.17) * mm, "end": v(-171.53, -24.83) * mm});
            skLineSegment(sketch, "E667.MirrorCS", {"start": v(-155.06, 0.87) * mm, "end": v(-155.06, 27.47) * mm});
            skLineSegment(sketch, "E668.MirrorCS", {"start": v(-160.56, 27.47) * mm, "end": v(-160.56, 52.87) * mm});
            skLineSegment(sketch, "E669.MirrorCS", {"start": v(-154.23, 79.17) * mm, "end": v(-154.23, 53.17) * mm});
            skLineSegment(sketch, "E670.MirrorCS", {"start": v(-208.9, -50.83) * mm, "end": v(-208.9, 79.17) * mm});
            skLineSegment(sketch, "E671.MirrorCS", {"start": v(-160.56, 0.87) * mm, "end": v(-160.56, -24.53) * mm});
            skLineSegment(sketch, "E672.MirrorCS", {"start": v(-176.73, 1.17) * mm, "end": v(-176.73, -24.83) * mm});
            skLineSegment(sketch, "E673", {"start": v(-155.06, 105.17) * mm, "end": v(-155.06, 53.17) * mm});
            skLineSegment(sketch, "E674.trimOffspring", {"start": v(-208.9, 79.17) * mm, "end": v(-231.57, 79.17) * mm});
            skLineSegment(sketch, "E675.trimOffspring", {"start": v(-181.73, 79.17) * mm, "end": v(-186.93, 79.17) * mm});
            skLineSegment(sketch, "E676.trimOffspring", {"start": v(-171.53, 79.17) * mm, "end": v(-176.73, 79.17) * mm});
            skLineSegment(sketch, "E677", {"start": v(-155.06, 105.17) * mm, "end": v(-160.56, 105.17) * mm});
            skLineSegment(sketch, "E678", {"start": v(-160.56, 105.17) * mm, "end": v(-160.56, 105.47) * mm});
            skPoint(sketch, "E679.orphan", {"position": v(-155.06, 105.47) * mm});
            skLineSegment(sketch, "E680.bottom", {"start": v(-155.06, 52.87) * mm, "end": v(-154.23, 52.87) * mm});
            skLineSegment(sketch, "E680.top", {"start": v(-160.56, 53.17) * mm, "end": v(-155.06, 53.17) * mm});
            skLineSegment(sketch, "E680.left", {"start": v(-160.56, 52.87) * mm, "end": v(-160.56, 53.17) * mm});
            skLineSegment(sketch, "E680.right", {"start": v(-154.23, 52.87) * mm, "end": v(-154.23, 53.17) * mm});
            skLineSegment(sketch, "E681.bottom", {"start": v(-160.56, 1.17) * mm, "end": v(-155.06, 1.17) * mm});
            skLineSegment(sketch, "E681.top", {"start": v(-160.56, 27.17) * mm, "end": v(-155.06, 27.17) * mm});
            skLineSegment(sketch, "E681.right", {"start": v(-154.23, 1.17) * mm, "end": v(-154.23, 27.17) * mm});
            skLineSegment(sketch, "E682", {"start": v(-160.56, 27.47) * mm, "end": v(-160.56, 27.17) * mm});
            skLineSegment(sketch, "E683.trimOffspring", {"start": v(-160.56, 1.17) * mm, "end": v(-160.56, 0.87) * mm});
            skLineSegment(sketch, "E684.bottom", {"start": v(-160.56, 157.17) * mm, "end": v(-155.06, 157.17) * mm});
            skLineSegment(sketch, "E684.top", {"start": v(-155.06, 157.47) * mm, "end": v(-154.23, 157.47) * mm});
            skLineSegment(sketch, "E684.left", {"start": v(-160.56, 157.17) * mm, "end": v(-160.56, 157.47) * mm});
            skLineSegment(sketch, "E685.top", {"start": v(-160.56, 131.17) * mm, "end": v(-154.23, 131.17) * mm});
            skLineSegment(sketch, "E685.left", {"start": v(-160.56, 130.87) * mm, "end": v(-160.56, 131.17) * mm});
            skLineSegment(sketch, "E685.right", {"start": v(-154.23, 130.87) * mm, "end": v(-154.23, 131.17) * mm});
            skLineSegment(sketch, "E686.bottom", {"start": v(-160.56, -24.83) * mm, "end": v(-154.23, -24.83) * mm});
            skLineSegment(sketch, "E686.left", {"start": v(-160.56, -24.83) * mm, "end": v(-160.56, -24.53) * mm});
            skLineSegment(sketch, "E687.bottom", {"start": v(-155.06, -50.83) * mm, "end": v(-160.56, -50.83) * mm});
            skLineSegment(sketch, "E687.top", {"start": v(-154.23, -56.33) * mm, "end": v(-155.06, -56.33) * mm});
            skLineSegment(sketch, "E687.left", {"start": v(-154.23, -50.83) * mm, "end": v(-154.23, -56.33) * mm});
            skLineSegment(sketch, "E687.right", {"start": v(-160.56, -50.83) * mm, "end": v(-160.56, -56.33) * mm});
            skPoint(sketch, "E688.MirrorCS.start.orphan", {"position": v(-155.06, -51.13) * mm});
            skPoint(sketch, "E689.MirrorCS.end.orphan", {"position": v(-160.26, -51.13) * mm});
            skLineSegment(sketch, "E690.trimOffspring", {"start": v(-160.26, -56.33) * mm, "end": v(-160.56, -56.33) * mm});
            skLineSegment(sketch, "E691.trimOffspring", {"start": v(-155.06, -51.13) * mm, "end": v(-155.06, -24.53) * mm});
            skLineSegment(sketch, "E692.bottom", {"start": v(-174.86, -56.33) * mm, "end": v(-174.56, -56.33) * mm});
            skLineSegment(sketch, "E692.top", {"start": v(-174.86, -50.83) * mm, "end": v(-174.56, -50.83) * mm});
            skLineSegment(sketch, "E692.right", {"start": v(-174.56, -56.33) * mm, "end": v(-174.56, -50.83) * mm});
            skLineSegment(sketch, "E693.bottom", {"start": v(0, 250.07) * mm, "end": v(0.3, 250.07) * mm});
            skLineSegment(sketch, "E693.top", {"start": v(0, 244.57) * mm, "end": v(0.3, 244.57) * mm});
            skLineSegment(sketch, "E693.left", {"start": v(0, 250.07) * mm, "end": v(0, 244.57) * mm});
            skLineSegment(sketch, "E694.bottom", {"start": v(-20.3, 250.07) * mm, "end": v(-20, 250.07) * mm});
            skLineSegment(sketch, "E694.top", {"start": v(-20.3, 243.74) * mm, "end": v(-20, 243.74) * mm});
            skLineSegment(sketch, "E694.right", {"start": v(-20, 250.07) * mm, "end": v(-20, 243.74) * mm});
            skLineSegment(sketch, "E695.bottom", {"start": v(40, 250.07) * mm, "end": v(39.7, 250.07) * mm});
            skLineSegment(sketch, "E695.top", {"start": v(40, 244.57) * mm, "end": v(39.7, 244.57) * mm});
            skLineSegment(sketch, "E695.left", {"start": v(40, 250.07) * mm, "end": v(40, 244.57) * mm});
            skLineSegment(sketch, "E696.bottom", {"start": v(60, 243.74) * mm, "end": v(60.3, 243.74) * mm});
            skLineSegment(sketch, "E696.top", {"start": v(60, 250.07) * mm, "end": v(60.3, 250.07) * mm});
            skLineSegment(sketch, "E696.left", {"start": v(60, 243.74) * mm, "end": v(60, 250.07) * mm});
            skPoint(sketch, "E697.MirrorCS.end.orphan", {"position": v(60.3, 243.74) * mm});
            skPoint(sketch, "E698.orphan", {"position": v(39.7, 250.07) * mm});
            skPoint(sketch, "E699.MirrorCS.end.orphan", {"position": v(39.7, 243.74) * mm});
            skLineSegment(sketch, "E700", {"start": v(-188.56, 214.67) * mm, "end": v(-208.9, 214.67) * mm});
            skLineSegment(sketch, "E701", {"start": v(-174.56, -56.33) * mm, "end": v(-174.86, -56.33) * mm});
            skLineSegment(sketch, "E702.trimOffspring", {"start": v(-188.56, -56.33) * mm, "end": v(-208.9, -56.33) * mm});
            skLineSegment(sketch, "E703.bottom", {"start": v(-174.86, 209.17) * mm, "end": v(-174.56, 209.17) * mm});
            skLineSegment(sketch, "E703.top", {"start": v(-174.86, 215.5) * mm, "end": v(-174.56, 215.5) * mm});
            skLineSegment(sketch, "E703.right", {"start": v(-174.56, 209.17) * mm, "end": v(-174.56, 215.5) * mm});
            skPoint(sketch, "E704.end.orphan", {"position": v(-174.86, 215.5) * mm});
            skPoint(sketch, "E705.end.orphan", {"position": v(-160.56, 215.5) * mm});
            skLineSegment(sketch, "E706", {"start": v(-160.56, 214.67) * mm, "end": v(-160.56, 209.47) * mm});
            skLineSegment(sketch, "E707", {"start": v(-160.56, 209.47) * mm, "end": v(-160.26, 209.47) * mm});
            skLineSegment(sketch, "E708.bottom", {"start": v(-160.56, 183.17) * mm, "end": v(-155.06, 183.17) * mm});
            skLineSegment(sketch, "E708.left", {"start": v(-160.56, 183.17) * mm, "end": v(-160.56, 182.87) * mm});
            skLineSegment(sketch, "E709", {"start": v(-186.93, 105.17) * mm, "end": v(-181.83, 105.17) * mm});
            skLineSegment(sketch, "E710", {"start": v(-181.83, 105.17) * mm, "end": v(-181.83, 53.17) * mm});
            skLineSegment(sketch, "E711", {"start": v(-176.73, 105.17) * mm, "end": v(-171.63, 105.17) * mm});
            skLineSegment(sketch, "E712", {"start": v(-171.63, 105.17) * mm, "end": v(-171.63, 53.17) * mm});
            skLineSegment(sketch, "E713.top", {"start": v(66.26, -975.76) * mm, "end": v(75.85, -975.76) * mm});
            skPoint(sketch, "E714.end.orphan", {"position": v(30.52, -975.76) * mm});
            skLineSegment(sketch, "E715.bottom", {"start": v(31.35, -975.76) * mm, "end": v(35.85, -975.76) * mm});
            skLineSegment(sketch, "E716.trimOffspring", {"start": v(35.85, -1105.76) * mm, "end": v(35.85, -1080.06) * mm});
            skLineSegment(sketch, "E717.trimOffspring", {"start": v(35.85, -1053.46) * mm, "end": v(35.85, -1028.06) * mm});
            skLineSegment(sketch, "E718.trimOffspring", {"start": v(35.85, -1001.46) * mm, "end": v(35.85, -974.76) * mm});
            skLineSegment(sketch, "E719", {"start": v(85.96, -968.43) * mm, "end": v(85.66, -968.43) * mm});
            skLineSegment(sketch, "E720.bottom", {"start": v(85.66, -968.43) * mm, "end": v(85.96, -968.43) * mm});
            skLineSegment(sketch, "E720.left", {"start": v(85.66, -970.26) * mm, "end": v(85.66, -974.76) * mm});
            skLineSegment(sketch, "E721", {"start": v(31.35, -1001.46) * mm, "end": v(35.85, -1001.46) * mm});
            skLineSegment(sketch, "E722", {"start": v(39.63, -1027.76) * mm, "end": v(39.63, -1028.06) * mm});
            skLineSegment(sketch, "E723", {"start": v(31.35, -1028.06) * mm, "end": v(35.85, -1028.06) * mm});
            skLineSegment(sketch, "E724", {"start": v(31.35, -1053.46) * mm, "end": v(35.85, -1053.46) * mm});
            skLineSegment(sketch, "E725", {"start": v(31.35, -1080.06) * mm, "end": v(35.85, -1080.06) * mm});
            skPoint(sketch, "E726.end.orphan", {"position": v(65.96, -975.76) * mm});
            skPoint(sketch, "E727.orphan", {"position": v(35.85, -1027.76) * mm});
            skPoint(sketch, "E728.orphan", {"position": v(35.85, -1053.76) * mm});
            skPoint(sketch, "E729.start.orphan", {"position": v(39.63, -1001.76) * mm});
            skPoint(sketch, "E730.trimOffspring.end.orphan", {"position": v(39.63, -1053.76) * mm});
            skPoint(sketch, "E731.start.orphan", {"position": v(39.63, -1079.76) * mm});
            skLineSegment(sketch, "E732.top", {"start": v(31.35, -1105.76) * mm, "end": v(39.63, -1105.76) * mm});
            skLineSegment(sketch, "E733.top", {"start": v(26.35, -1105.76) * mm, "end": v(39.63, -1105.76) * mm});
            skLineSegment(sketch, "E733.left", {"start": v(26.35, -971.61) * mm, "end": v(26.35, -1105.76) * mm});
            skLineSegment(sketch, "E734.bottom", {"start": v(35.85, -975.76) * mm, "end": v(31.35, -975.76) * mm});
            skLineSegment(sketch, "E734.top", {"start": v(35.85, -1001.46) * mm, "end": v(31.35, -1001.46) * mm});
            skLineSegment(sketch, "E734.left", {"start": v(35.85, -975.76) * mm, "end": v(35.85, -1001.46) * mm});
            skLineSegment(sketch, "E734.right", {"start": v(31.35, -975.76) * mm, "end": v(31.35, -1001.46) * mm});
            skLineSegment(sketch, "E735.trimOffspring", {"start": v(31.35, -1080.06) * mm, "end": v(31.35, -1105.76) * mm});
            skLineSegment(sketch, "E736.trimOffspring", {"start": v(31.35, -1028.06) * mm, "end": v(31.35, -1053.46) * mm});
            skLineSegment(sketch, "E737", {"start": v(66.26, -971.26) * mm, "end": v(75.85, -971.26) * mm});
            skPoint(sketch, "E738.visualSharp", {"position": v(26.35, -965.26) * mm});
            skArc(sketch, "E738.filletArc", {"start": v(32.7, -965.26) * mm, "mid": v(28.21, -967.12) * mm, "end": v(26.35, -971.61) * mm});
            skLineSegment(sketch, "E739.bottom", {"start": v(-234.5, -973.9) * mm, "end": v(-220.8, -973.9) * mm});
            skPoint(sketch, "E740.start.orphan", {"position": v(-206.5, -1103.9) * mm});
            skLineSegment(sketch, "E741.bottom", {"start": v(-234.5, -973.9) * mm, "end": v(-227.5, -973.9) * mm});
            skLineSegment(sketch, "E742", {"start": v(-234.5, -967.57) * mm, "end": v(-234.5, -968.4) * mm});
            skLineSegment(sketch, "E743.trimOffspring", {"start": v(-206.5, -1077.6) * mm, "end": v(-206.5, -1052.2) * mm});
            skLineSegment(sketch, "E744.trimOffspring", {"start": v(-206.5, -1025.6) * mm, "end": v(-206.5, -1000.2) * mm});
            skLineSegment(sketch, "E745.trimOffspring", {"start": v(-206.5, -1052.2) * mm, "end": v(-206.5, -1077.6) * mm});
            skLineSegment(sketch, "E746", {"start": v(-217.46, -999.9) * mm, "end": v(-222.66, -999.9) * mm});
            skLineSegment(sketch, "E747", {"start": v(-217.46, -1077.9) * mm, "end": v(-222.66, -1077.9) * mm});
            skLineSegment(sketch, "E748.bottom", {"start": v(-232.86, -999.9) * mm, "end": v(-227.66, -999.9) * mm});
            skLineSegment(sketch, "E748.top", {"start": v(-232.86, -1025.9) * mm, "end": v(-227.66, -1025.9) * mm});
            skLineSegment(sketch, "E748.left", {"start": v(-254.83, -999.9) * mm, "end": v(-254.83, -1025.9) * mm});
            skLineSegment(sketch, "E749", {"start": v(-230.66, -999.9) * mm, "end": v(-227.66, -999.9) * mm});
            skLineSegment(sketch, "E750", {"start": v(-227.66, -999.9) * mm, "end": v(-232.86, -999.9) * mm});
            skLineSegment(sketch, "E751", {"start": v(-232.86, -999.9) * mm, "end": v(-232.86, -1025.9) * mm});
            skPoint(sketch, "E752.end.orphan", {"position": v(-230.66, -1025.9) * mm});
            skLineSegment(sketch, "E753", {"start": v(-222.66, -1025.9) * mm, "end": v(-222.66, -999.9) * mm});
            skLineSegment(sketch, "E754.trimOffspring", {"start": v(-222.66, -1025.9) * mm, "end": v(-217.46, -1025.9) * mm});
            skPoint(sketch, "E755.start.orphan", {"position": v(-225.16, -1077.9) * mm});
            skPoint(sketch, "E756.orphan", {"position": v(-222.66, -1077.9) * mm});
            skLineSegment(sketch, "E757.trimOffspring", {"start": v(-227.76, -1077.9) * mm, "end": v(-232.86, -1077.9) * mm});
            skPoint(sketch, "E741.right.start.orphan", {"position": v(-206.5, -973.9) * mm});
            skLineSegment(sketch, "E758.left", {"start": v(-206.5, -968.4) * mm, "end": v(-206.5, -967.57) * mm});
            skLineSegment(sketch, "E759.left", {"start": v(-254.83, -973.9) * mm, "end": v(-254.83, -967.57) * mm});
            skLineSegment(sketch, "E760", {"start": v(-200.17, -973.9) * mm, "end": v(-200.17, -973.6) * mm});
            skLineSegment(sketch, "E761", {"start": v(-201, -973.6) * mm, "end": v(-206.2, -973.6) * mm});
            skLineSegment(sketch, "E762", {"start": v(-200.17, -999.9) * mm, "end": v(-200.17, -1000.2) * mm});
            skLineSegment(sketch, "E763", {"start": v(-200.17, -1000.2) * mm, "end": v(-201, -1000.2) * mm});
            skLineSegment(sketch, "E764", {"start": v(-200.17, -1025.9) * mm, "end": v(-200.17, -1025.6) * mm});
            skLineSegment(sketch, "E765", {"start": v(-200.17, -1051.9) * mm, "end": v(-200.17, -1052.2) * mm});
            skLineSegment(sketch, "E766", {"start": v(-200.17, -1077.9) * mm, "end": v(-200.17, -1077.6) * mm});
            skPoint(sketch, "E767.orphan", {"position": v(-220.5, -973.9) * mm});
            skPoint(sketch, "E768.orphan", {"position": v(-206.5, -999.9) * mm});
            skLineSegment(sketch, "E769.trimOffspring", {"start": v(-201, -1025.6) * mm, "end": v(-201, -1025.9) * mm});
            skPoint(sketch, "E770.orphan", {"position": v(-206.5, -1025.9) * mm});
            skPoint(sketch, "E771.endSnap0", {"position": v(-232.86, -1103.9) * mm});
            skLineSegment(sketch, "E772", {"start": v(-206.5, -968.4) * mm, "end": v(-206.2, -968.4) * mm});
            skLineSegment(sketch, "E773", {"start": v(-254.83, -973.9) * mm, "end": v(-254.83, -1025.9) * mm});
            skLineSegment(sketch, "E774.trimOffspring", {"start": v(-227.66, -1103.9) * mm, "end": v(-232.86, -1103.9) * mm});
            skLineSegment(sketch, "E775.trimOffspring", {"start": v(-217.46, -1103.9) * mm, "end": v(-222.66, -1103.9) * mm});
            skLineSegment(sketch, "E776", {"start": v(-202, -1077.9) * mm, "end": v(-206.5, -1077.9) * mm});
            skLineSegment(sketch, "E777", {"start": v(-206.5, -1077.9) * mm, "end": v(-206.5, -1077.6) * mm});
            skPoint(sketch, "E778.orphan", {"position": v(-201, -1077.6) * mm});
            skLineSegment(sketch, "E779.bottom", {"start": v(-206.5, -1025.9) * mm, "end": v(-201, -1025.9) * mm});
            skLineSegment(sketch, "E779.top", {"start": v(-201, -1025.6) * mm, "end": v(-200.17, -1025.6) * mm});
            skLineSegment(sketch, "E779.left", {"start": v(-206.5, -1025.9) * mm, "end": v(-206.5, -1025.6) * mm});
            skLineSegment(sketch, "E780.top", {"start": v(-206.5, -1051.9) * mm, "end": v(-200.17, -1051.9) * mm});
            skLineSegment(sketch, "E780.left", {"start": v(-206.5, -1052.2) * mm, "end": v(-206.5, -1051.9) * mm});
            skLineSegment(sketch, "E780.right", {"start": v(-200.17, -1052.2) * mm, "end": v(-200.17, -1051.9) * mm});
            skLineSegment(sketch, "E781.bottom", {"start": v(-220.8, -973.9) * mm, "end": v(-220.5, -973.9) * mm});
            skLineSegment(sketch, "E781.top", {"start": v(-220.8, -967.57) * mm, "end": v(-220.5, -967.57) * mm});
            skPoint(sketch, "E782.end.orphan", {"position": v(-220.8, -967.57) * mm});
            skPoint(sketch, "E783.end.orphan", {"position": v(-206.5, -967.57) * mm});
            skLineSegment(sketch, "E784", {"start": v(-206.5, -968.4) * mm, "end": v(-206.5, -973.6) * mm});
            skLineSegment(sketch, "E785", {"start": v(-206.5, -973.6) * mm, "end": v(-206.2, -973.6) * mm});
            skLineSegment(sketch, "E786.bottom", {"start": v(-206.5, -999.9) * mm, "end": v(-202, -999.9) * mm});
            skLineSegment(sketch, "E786.left", {"start": v(-206.5, -999.9) * mm, "end": v(-206.5, -1000.2) * mm});
            skLineSegment(sketch, "E787", {"start": v(-232.86, -1077.9) * mm, "end": v(-227.76, -1077.9) * mm});
            skLineSegment(sketch, "E788", {"start": v(-222.66, -1077.9) * mm, "end": v(-217.56, -1077.9) * mm});
            skLineSegment(sketch, "E789", {"start": v(-254.83, -1103.9) * mm, "end": v(-248.5, -1103.9) * mm});
            skLineSegment(sketch, "E790", {"start": v(-254.83, -973.9) * mm, "end": v(-254.83, -969.4) * mm});
            skLineSegment(sketch, "E791", {"start": v(-254.83, -969.4) * mm, "end": v(-250.33, -969.4) * mm});
            skLineSegment(sketch, "E792", {"start": v(-202, -973.6) * mm, "end": v(-202, -999.9) * mm});
            skLineSegment(sketch, "E793", {"start": v(-232.86, -999.9) * mm, "end": v(-229.16, -999.9) * mm});
            skLineSegment(sketch, "E794", {"start": v(-232.86, -999.9) * mm, "end": v(-228.36, -999.9) * mm});
            skLineSegment(sketch, "E795", {"start": v(-228.36, -999.9) * mm, "end": v(-228.36, -1025.9) * mm});
            skLineSegment(sketch, "E796", {"start": v(-222.66, -999.9) * mm, "end": v(-218.16, -999.9) * mm});
            skLineSegment(sketch, "E797", {"start": v(-218.16, -999.9) * mm, "end": v(-218.16, -1025.9) * mm});
            skLineSegment(sketch, "E798.bottom", {"start": v(-232.86, -1077.9) * mm, "end": v(-228.36, -1077.9) * mm});
            skLineSegment(sketch, "E798.top", {"start": v(-232.86, -1103.9) * mm, "end": v(-228.36, -1103.9) * mm});
            skLineSegment(sketch, "E798.left", {"start": v(-232.86, -1077.9) * mm, "end": v(-232.86, -1103.9) * mm});
            skLineSegment(sketch, "E798.right", {"start": v(-228.36, -1077.9) * mm, "end": v(-228.36, -1103.9) * mm});
            skLineSegment(sketch, "E799.bottom", {"start": v(-222.66, -1077.9) * mm, "end": v(-218.16, -1077.9) * mm});
            skLineSegment(sketch, "E799.top", {"start": v(-222.66, -1103.9) * mm, "end": v(-218.16, -1103.9) * mm});
            skLineSegment(sketch, "E799.left", {"start": v(-222.66, -1077.9) * mm, "end": v(-222.66, -1103.9) * mm});
            skLineSegment(sketch, "E799.right", {"start": v(-218.16, -1077.9) * mm, "end": v(-218.16, -1103.9) * mm});
            skLineSegment(sketch, "E800.trimOffspring", {"start": v(-202, -1077.9) * mm, "end": v(-202, -1103.9) * mm});
            skLineSegment(sketch, "E801.trimOffspring", {"start": v(-234.5, -969.4) * mm, "end": v(-234.5, -973.9) * mm});
            skLineSegment(sketch, "E802.trimOffspring", {"start": v(-220.5, -968.4) * mm, "end": v(-220.5, -967.57) * mm});
            skLineSegment(sketch, "E803.trimOffspring", {"start": v(-220.5, -969.4) * mm, "end": v(-206.5, -969.4) * mm});
            skLineSegment(sketch, "E804", {"start": v(-202, -1051.9) * mm, "end": v(-202, -1025.9) * mm});
            skPoint(sketch, "E804.endSnap0", {"position": v(-203.75, -1025.9) * mm});
            skLineSegment(sketch, "E805.trimOffspring", {"start": v(-201, -1051.9) * mm, "end": v(-201, -1052.2) * mm});
            skLineSegment(sketch, "E806.MirrorCS", {"start": v(-217.46, -1129.9) * mm, "end": v(-222.66, -1129.9) * mm});
            skLineSegment(sketch, "E807.MirrorCS", {"start": v(-227.66, -1207.9) * mm, "end": v(-232.86, -1207.9) * mm});
            skLineSegment(sketch, "E808.MirrorCS", {"start": v(-200.17, -1155.6) * mm, "end": v(-200.17, -1155.9) * mm});
            skLineSegment(sketch, "E809.MirrorCS", {"start": v(-232.86, -1207.9) * mm, "end": v(-228.36, -1207.9) * mm});
            skLineSegment(sketch, "E810.MirrorCS", {"start": v(-232.86, -1207.9) * mm, "end": v(-229.16, -1207.9) * mm});
            skLineSegment(sketch, "E811.MirrorCS", {"start": v(-230.66, -1207.9) * mm, "end": v(-227.66, -1207.9) * mm});
            skLineSegment(sketch, "E812.MirrorCS", {"start": v(-222.66, -1129.9) * mm, "end": v(-217.56, -1129.9) * mm});
            skLineSegment(sketch, "E813.MirrorCS", {"start": v(-200.17, -1207.9) * mm, "end": v(-200.17, -1207.6) * mm});
            skLineSegment(sketch, "E814.MirrorCS", {"start": v(-222.66, -1129.9) * mm, "end": v(-218.16, -1129.9) * mm});
            skLineSegment(sketch, "E815.MirrorCS", {"start": v(-201, -1155.9) * mm, "end": v(-201, -1155.6) * mm});
            skLineSegment(sketch, "E816.MirrorCS", {"start": v(-200.17, -1155.9) * mm, "end": v(-200.17, -1155.6) * mm});
            skLineSegment(sketch, "E817.MirrorCS", {"start": v(-200.17, -1207.6) * mm, "end": v(-201, -1207.6) * mm});
            skLineSegment(sketch, "E818.MirrorCS", {"start": v(-232.86, -1207.9) * mm, "end": v(-227.66, -1207.9) * mm});
            skLineSegment(sketch, "E819.MirrorCS", {"start": v(-232.86, -1129.9) * mm, "end": v(-228.36, -1129.9) * mm});
            skLineSegment(sketch, "E820.MirrorCS", {"start": v(-206.5, -1234.2) * mm, "end": v(-206.2, -1234.2) * mm});
            skLineSegment(sketch, "E821.MirrorCS", {"start": v(-206.5, -1129.9) * mm, "end": v(-206.5, -1130.2) * mm});
            skLineSegment(sketch, "E822.MirrorCS", {"start": v(-206.5, -1239.4) * mm, "end": v(-206.2, -1239.4) * mm});
            skLineSegment(sketch, "E823.MirrorCS", {"start": v(-227.76, -1129.9) * mm, "end": v(-232.86, -1129.9) * mm});
            skLineSegment(sketch, "E824.MirrorCS", {"start": v(-206.5, -1155.6) * mm, "end": v(-206.5, -1155.9) * mm});
            skLineSegment(sketch, "E825.MirrorCS", {"start": v(-206.5, -1207.9) * mm, "end": v(-206.5, -1207.6) * mm});
            skLineSegment(sketch, "E826.MirrorCS", {"start": v(-200.17, -1181.9) * mm, "end": v(-200.17, -1182.2) * mm});
            skLineSegment(sketch, "E827.MirrorCS", {"start": v(-220.8, -1240.23) * mm, "end": v(-220.5, -1240.23) * mm});
            skLineSegment(sketch, "E828.MirrorCS", {"start": v(-206.5, -1239.4) * mm, "end": v(-206.5, -1234.2) * mm});
            skLineSegment(sketch, "E829.MirrorCS", {"start": v(-232.86, -1129.9) * mm, "end": v(-227.76, -1129.9) * mm});
            skLineSegment(sketch, "E830.MirrorCS", {"start": v(-206.5, -1239.4) * mm, "end": v(-206.5, -1240.23) * mm});
            skLineSegment(sketch, "E831.MirrorCS", {"start": v(-220.5, -1239.4) * mm, "end": v(-220.5, -1240.23) * mm});
            skLineSegment(sketch, "E832.MirrorCS", {"start": v(-201, -1182.2) * mm, "end": v(-200.17, -1182.2) * mm});
            skLineSegment(sketch, "E833.MirrorCS", {"start": v(-220.8, -1233.9) * mm, "end": v(-220.5, -1233.9) * mm});
            skLineSegment(sketch, "E834.MirrorCS", {"start": v(-202, -1129.9) * mm, "end": v(-206.5, -1129.9) * mm});
            skLineSegment(sketch, "E835.MirrorCS", {"start": v(-206.5, -1181.9) * mm, "end": v(-206.5, -1182.2) * mm});
            skLineSegment(sketch, "E836.MirrorCS", {"start": v(-217.46, -1207.9) * mm, "end": v(-222.66, -1207.9) * mm});
            skLineSegment(sketch, "E837.MirrorCS", {"start": v(-206.5, -1207.9) * mm, "end": v(-202, -1207.9) * mm});
            skLineSegment(sketch, "E838.MirrorCS", {"start": v(-201, -1234.2) * mm, "end": v(-206.2, -1234.2) * mm});
            skLineSegment(sketch, "E839.MirrorCS", {"start": v(-200.17, -1233.9) * mm, "end": v(-200.17, -1234.2) * mm});
            skLineSegment(sketch, "E840.MirrorCS", {"start": v(-201, -1182.2) * mm, "end": v(-201, -1181.9) * mm});
            skLineSegment(sketch, "E841.MirrorCS", {"start": v(-222.66, -1207.9) * mm, "end": v(-218.16, -1207.9) * mm});
            skLineSegment(sketch, "E842.MirrorCS", {"start": v(-200.17, -1129.9) * mm, "end": v(-200.17, -1130.2) * mm});
            skLineSegment(sketch, "E843.MirrorCS", {"start": v(-254.83, -1233.9) * mm, "end": v(-254.83, -1240.23) * mm});
            skLineSegment(sketch, "E844.MirrorCS", {"start": v(-222.66, -1181.9) * mm, "end": v(-217.46, -1181.9) * mm});
            skLineSegment(sketch, "E845.MirrorCS", {"start": v(-234.5, -1238.4) * mm, "end": v(-234.5, -1233.9) * mm});
            skLineSegment(sketch, "E846.MirrorCS", {"start": v(-206.5, -1181.9) * mm, "end": v(-201, -1181.9) * mm});
            skLineSegment(sketch, "E847.MirrorCS", {"start": v(-254.83, -1233.9) * mm, "end": v(-254.83, -1238.4) * mm});
            skLineSegment(sketch, "E848.MirrorCS", {"start": v(-234.5, -1240.23) * mm, "end": v(-234.5, -1239.4) * mm});
            skLineSegment(sketch, "E849.MirrorCS", {"start": v(-232.86, -1181.9) * mm, "end": v(-227.66, -1181.9) * mm});
            skLineSegment(sketch, "E850.MirrorCS", {"start": v(-254.83, -1207.9) * mm, "end": v(-254.83, -1181.9) * mm});
            skLineSegment(sketch, "E851.MirrorCS", {"start": v(-228.36, -1129.9) * mm, "end": v(-228.36, -1103.9) * mm});
            skPoint(sketch, "E852.MirrorP", {"position": v(-206.5, -1233.9) * mm});
            skLineSegment(sketch, "E853.MirrorCS", {"start": v(-218.16, -1129.9) * mm, "end": v(-218.16, -1103.9) * mm});
            skLineSegment(sketch, "E854.MirrorCS", {"start": v(-206.5, -1155.6) * mm, "end": v(-206.5, -1130.2) * mm});
            skLineSegment(sketch, "E855.MirrorCS", {"start": v(-206.5, -1155.9) * mm, "end": v(-200.17, -1155.9) * mm});
            skLineSegment(sketch, "E856.MirrorCS", {"start": v(-222.66, -1181.9) * mm, "end": v(-222.66, -1207.9) * mm});
            skLineSegment(sketch, "E857.MirrorCS", {"start": v(-202, -1234.2) * mm, "end": v(-202, -1207.9) * mm});
            skPoint(sketch, "E858.MirrorP", {"position": v(-230.66, -1181.9) * mm});
            skLineSegment(sketch, "E859.MirrorCS", {"start": v(-218.16, -1207.9) * mm, "end": v(-218.16, -1181.9) * mm});
            skPoint(sketch, "E860.MirrorP", {"position": v(-203.75, -1181.9) * mm});
            skPoint(sketch, "E861.MirrorP", {"position": v(-201, -1130.2) * mm});
            skLineSegment(sketch, "E862.MirrorCS", {"start": v(-228.36, -1207.9) * mm, "end": v(-228.36, -1181.9) * mm});
            skLineSegment(sketch, "E863.MirrorCS", {"start": v(-234.5, -1233.9) * mm, "end": v(-220.8, -1233.9) * mm});
            skLineSegment(sketch, "E864.MirrorCS", {"start": v(-232.86, -1129.9) * mm, "end": v(-232.86, -1103.9) * mm});
            skPoint(sketch, "E865.MirrorP", {"position": v(-225.16, -1129.9) * mm});
            skLineSegment(sketch, "E866.MirrorCS", {"start": v(-220.5, -1238.4) * mm, "end": v(-206.5, -1238.4) * mm});
            skLineSegment(sketch, "E867.MirrorCS", {"start": v(-202, -1129.9) * mm, "end": v(-202, -1103.9) * mm});
            skPoint(sketch, "E868.MirrorP", {"position": v(-206.5, -1207.9) * mm});
            skLineSegment(sketch, "E869.MirrorCS", {"start": v(-232.86, -1207.9) * mm, "end": v(-232.86, -1181.9) * mm});
            skPoint(sketch, "E870.MirrorP", {"position": v(-206.5, -1240.23) * mm});
            skLineSegment(sketch, "E871.MirrorCS", {"start": v(-234.5, -1233.9) * mm, "end": v(-227.5, -1233.9) * mm});
            skLineSegment(sketch, "E872.MirrorCS", {"start": v(-202, -1155.9) * mm, "end": v(-202, -1181.9) * mm});
            skPoint(sketch, "E873.MirrorP", {"position": v(-222.66, -1129.9) * mm});
            skPoint(sketch, "E874.MirrorP", {"position": v(-220.8, -1240.23) * mm});
            skLineSegment(sketch, "E875.MirrorCS", {"start": v(-206.5, -1130.2) * mm, "end": v(-206.5, -1155.6) * mm});
            skPoint(sketch, "E876.MirrorP", {"position": v(-220.5, -1233.9) * mm});
            skPoint(sketch, "E877.MirrorP", {"position": v(-206.5, -1181.9) * mm});
            skLineSegment(sketch, "E878.MirrorCS", {"start": v(-206.5, -1182.2) * mm, "end": v(-206.5, -1207.6) * mm});
            skLineSegment(sketch, "E879.MirrorCS", {"start": v(-248.5, -1238.4) * mm, "end": v(-234.5, -1238.4) * mm});
            skLineSegment(sketch, "E880.MirrorCS", {"start": v(-222.66, -1129.9) * mm, "end": v(-222.66, -1103.9) * mm});
            skLineSegment(sketch, "E881.MirrorCS", {"start": v(-254.83, -1207.9) * mm, "end": v(-254.83, -1182.2) * mm});
            skLineSegment(sketch, "E882", {"start": v(-253, -999.9) * mm, "end": v(-250.33, -999.9) * mm});
            skLineSegment(sketch, "E883", {"start": v(-250.33, -973.6) * mm, "end": v(-250.33, -969.4) * mm});
            skLineSegment(sketch, "E884", {"start": v(-227.5, -973.9) * mm, "end": v(-227.5, -985.28) * mm});
            skLineSegment(sketch, "E885.MirrorCS", {"start": v(-254, -1025.6) * mm, "end": v(-254.83, -1025.6) * mm});
            skLineSegment(sketch, "E886.MirrorCS", {"start": v(-254.83, -1025.9) * mm, "end": v(-254.83, -1025.6) * mm});
            skLineSegment(sketch, "E887.MirrorCS", {"start": v(-254.83, -1181.9) * mm, "end": v(-254.83, -1182.2) * mm});
            skLineSegment(sketch, "E888.MirrorCS", {"start": v(-254, -1025.6) * mm, "end": v(-254, -1025.9) * mm});
            skLineSegment(sketch, "E889.MirrorCS", {"start": v(-254, -1182.2) * mm, "end": v(-254.83, -1182.2) * mm});
            skLineSegment(sketch, "E890.MirrorCS", {"start": v(-254.83, -1052.2) * mm, "end": v(-254.83, -1051.9) * mm});
            skLineSegment(sketch, "E891.MirrorCS", {"start": v(-254, -1182.2) * mm, "end": v(-254, -1181.9) * mm});
            skLineSegment(sketch, "E892.MirrorCS", {"start": v(-254.83, -999.9) * mm, "end": v(-254.83, -1000.2) * mm});
            skLineSegment(sketch, "E893.MirrorCS", {"start": v(-254.83, -1051.9) * mm, "end": v(-254.83, -1052.2) * mm});
            skLineSegment(sketch, "E894.MirrorCS", {"start": v(-254, -1051.9) * mm, "end": v(-254, -1052.2) * mm});
            skLineSegment(sketch, "E895.MirrorCS", {"start": v(-254.83, -1000.2) * mm, "end": v(-254, -1000.2) * mm});
            skLineSegment(sketch, "E896.MirrorCS", {"start": v(-254.83, -1207.9) * mm, "end": v(-254.83, -1207.6) * mm});
            skLineSegment(sketch, "E897.MirrorCS", {"start": v(-248.5, -1181.9) * mm, "end": v(-248.5, -1182.2) * mm});
            skLineSegment(sketch, "E898.MirrorCS", {"start": v(-254.83, -1207.6) * mm, "end": v(-254, -1207.6) * mm});
            skLineSegment(sketch, "E899.MirrorCS", {"start": v(-248.5, -1025.9) * mm, "end": v(-248.5, -1025.6) * mm});
            skLineSegment(sketch, "E900.MirrorCS", {"start": v(-248.5, -1052.2) * mm, "end": v(-248.5, -1051.9) * mm});
            skLineSegment(sketch, "E901.MirrorCS", {"start": v(-248.5, -973.6) * mm, "end": v(-248.8, -973.6) * mm});
            skLineSegment(sketch, "E902.MirrorCS", {"start": v(-248.5, -1025.9) * mm, "end": v(-253, -1025.9) * mm});
            skLineSegment(sketch, "E903.MirrorCS", {"start": v(-248.5, -968.4) * mm, "end": v(-248.8, -968.4) * mm});
            skLineSegment(sketch, "E904.MirrorCS", {"start": v(-248.5, -1239.4) * mm, "end": v(-248.5, -1240.23) * mm});
            skLineSegment(sketch, "E905.MirrorCS", {"start": v(-248.5, -1207.9) * mm, "end": v(-248.5, -1207.6) * mm});
            skLineSegment(sketch, "E906.MirrorCS", {"start": v(-248.5, -1051.9) * mm, "end": v(-254.83, -1051.9) * mm});
            skLineSegment(sketch, "E907.MirrorCS", {"start": v(-248.5, -1234.2) * mm, "end": v(-248.8, -1234.2) * mm});
            skLineSegment(sketch, "E908.MirrorCS", {"start": v(-248.5, -968.4) * mm, "end": v(-248.5, -967.57) * mm});
            skLineSegment(sketch, "E909.MirrorCS", {"start": v(-248.5, -968.4) * mm, "end": v(-248.5, -973.6) * mm});
            skLineSegment(sketch, "E910.MirrorCS", {"start": v(-248.5, -1207.9) * mm, "end": v(-253, -1207.9) * mm});
            skLineSegment(sketch, "E911.MirrorCS", {"start": v(-248.5, -1129.9) * mm, "end": v(-248.5, -1130.2) * mm});
            skLineSegment(sketch, "E912.MirrorCS", {"start": v(-248.5, -1181.9) * mm, "end": v(-254, -1181.9) * mm});
            skLineSegment(sketch, "E913.MirrorCS", {"start": v(-248.5, -999.9) * mm, "end": v(-253, -999.9) * mm});
            skLineSegment(sketch, "E914.MirrorCS", {"start": v(-254.83, -1155.6) * mm, "end": v(-254.83, -1155.9) * mm});
            skLineSegment(sketch, "E915.MirrorCS", {"start": v(-248.5, -1239.4) * mm, "end": v(-248.8, -1239.4) * mm});
            skLineSegment(sketch, "E916.MirrorCS", {"start": v(-248.5, -999.9) * mm, "end": v(-248.5, -1000.2) * mm});
            skLineSegment(sketch, "E917.MirrorCS", {"start": v(-254, -1155.9) * mm, "end": v(-254, -1155.6) * mm});
            skLineSegment(sketch, "E918.MirrorCS", {"start": v(-248.5, -1239.4) * mm, "end": v(-248.5, -1234.2) * mm});
            skLineSegment(sketch, "E919.MirrorCS", {"start": v(-254.83, -973.9) * mm, "end": v(-254.83, -973.6) * mm});
            skLineSegment(sketch, "E920.MirrorCS", {"start": v(-254, -973.6) * mm, "end": v(-248.8, -973.6) * mm});
            skLineSegment(sketch, "E921.MirrorCS", {"start": v(-254.83, -1155.9) * mm, "end": v(-254.83, -1155.6) * mm});
            skLineSegment(sketch, "E922.MirrorCS", {"start": v(-253, -1129.9) * mm, "end": v(-248.5, -1129.9) * mm});
            skPoint(sketch, "E923.MirrorP", {"position": v(-248.5, -1103.9) * mm});
            skLineSegment(sketch, "E924.MirrorCS", {"start": v(-248.5, -1077.9) * mm, "end": v(-248.5, -1077.6) * mm});
            skLineSegment(sketch, "E925.MirrorCS", {"start": v(-248.5, -1155.6) * mm, "end": v(-248.5, -1155.9) * mm});
            skLineSegment(sketch, "E926.MirrorCS", {"start": v(-253, -1077.9) * mm, "end": v(-248.5, -1077.9) * mm});
            skLineSegment(sketch, "E927.MirrorCS", {"start": v(-248.5, -1155.9) * mm, "end": v(-254.83, -1155.9) * mm});
            skLineSegment(sketch, "E928.MirrorCS", {"start": v(-254, -1234.2) * mm, "end": v(-248.8, -1234.2) * mm});
            skLineSegment(sketch, "E929.MirrorCS", {"start": v(-254.83, -1233.9) * mm, "end": v(-254.83, -1234.2) * mm});
            skLineSegment(sketch, "E930.MirrorCS", {"start": v(-248.5, -1052.2) * mm, "end": v(-248.5, -1077.6) * mm});
            skPoint(sketch, "E931.MirrorP", {"position": v(-248.5, -1233.9) * mm});
            skPoint(sketch, "E932.MirrorP", {"position": v(-248.5, -1025.9) * mm});
            skLineSegment(sketch, "E933.MirrorCS", {"start": v(-248.5, -1155.6) * mm, "end": v(-248.5, -1130.2) * mm});
            skPoint(sketch, "E934.MirrorP", {"position": v(-248.5, -973.9) * mm});
            skPoint(sketch, "E935.MirrorP", {"position": v(-248.5, -999.9) * mm});
            skPoint(sketch, "E936.MirrorP", {"position": v(-248.5, -1181.9) * mm});
            skLineSegment(sketch, "E937.MirrorCS", {"start": v(-253, -1234.2) * mm, "end": v(-253, -1207.9) * mm});
            skPoint(sketch, "E938.MirrorP", {"position": v(-254, -1077.6) * mm});
            skPoint(sketch, "E939.MirrorP", {"position": v(-248.5, -1207.9) * mm});
            skLineSegment(sketch, "E940.MirrorCS", {"start": v(-248.5, -1077.6) * mm, "end": v(-248.5, -1052.2) * mm});
            skLineSegment(sketch, "E941.MirrorCS", {"start": v(-248.5, -1025.6) * mm, "end": v(-248.5, -1000.2) * mm});
            skLineSegment(sketch, "E942.MirrorCS", {"start": v(-253, -1077.9) * mm, "end": v(-253, -1103.9) * mm});
            skLineSegment(sketch, "E943.MirrorCS", {"start": v(-253, -973.6) * mm, "end": v(-253, -999.9) * mm});
            skLineSegment(sketch, "E944.MirrorCS", {"start": v(-248.5, -1130.2) * mm, "end": v(-248.5, -1155.6) * mm});
            skPoint(sketch, "E945.MirrorP", {"position": v(-251.25, -1025.9) * mm});
            skLineSegment(sketch, "E946.MirrorCS", {"start": v(-253, -1051.9) * mm, "end": v(-253, -1025.9) * mm});
            skPoint(sketch, "E947.MirrorP", {"position": v(-248.5, -967.57) * mm});
            skLineSegment(sketch, "E948.MirrorCS", {"start": v(-248.5, -1182.2) * mm, "end": v(-248.5, -1207.6) * mm});
            skLineSegment(sketch, "E949.MirrorCS", {"start": v(-253, -1129.9) * mm, "end": v(-253, -1103.9) * mm});
            skLineSegment(sketch, "E950.MirrorCS", {"start": v(-253, -1155.9) * mm, "end": v(-253, -1181.9) * mm});
            skPoint(sketch, "E951.MirrorP", {"position": v(-254, -1130.2) * mm});
            skPoint(sketch, "E952.MirrorP", {"position": v(-251.25, -1181.9) * mm});
            skPoint(sketch, "E953.MirrorP", {"position": v(-248.5, -1240.23) * mm});
            skLineSegment(sketch, "E954.trimOffspring", {"start": v(-232.86, -1103.9) * mm, "end": v(-200.17, -1103.9) * mm});
            skLineSegment(sketch, "E955.trimOffspring", {"start": v(-248.5, -969.4) * mm, "end": v(-234.5, -969.4) * mm});
            skCircle(sketch, "E956", {"center": v(43.65, -981.58) * mm, "radius": 2.8 * mm});
            skLineSegment(sketch, "E957", {"start": v(312.49, -1030.47) * mm, "end": v(312.49, -1030.77) * mm});
            skPoint(sketch, "E958.MirrorCS.end.orphan", {"position": v(369.7, -1108.47) * mm});
            skPoint(sketch, "E959.MirrorCS.start.orphan", {"position": v(378.82, -1108.47) * mm});
            skLineSegment(sketch, "E960.bottom", {"start": v(305.55, -967.97) * mm, "end": v(378.82, -967.97) * mm});
            skLineSegment(sketch, "E960.left", {"start": v(299.2, -974.32) * mm, "end": v(299.2, -1108.47) * mm});
            skLineSegment(sketch, "E960.right", {"start": v(378.82, -967.97) * mm, "end": v(378.82, -978.47) * mm});
            skPoint(sketch, "E961.visualSharp", {"position": v(299.2, -967.97) * mm});
            skArc(sketch, "E961.filletArc", {"start": v(305.55, -967.97) * mm, "mid": v(301.06, -969.83) * mm, "end": v(299.2, -974.32) * mm});
            skLineSegment(sketch, "E962.MirrorCS", {"start": v(445.15, -1030.47) * mm, "end": v(445.15, -1030.77) * mm});
            skPoint(sketch, "E963.MirrorP", {"position": v(445.15, -1108.47) * mm});
            skArc(sketch, "E964.MirrorCS", {"start": v(452.08, -967.97) * mm, "mid": v(456.57, -969.83) * mm, "end": v(458.43, -974.32) * mm});
            skLineSegment(sketch, "E965.MirrorCS", {"start": v(452.08, -967.97) * mm, "end": v(378.82, -967.97) * mm});
            skPoint(sketch, "E966.MirrorP", {"position": v(458.43, -967.97) * mm});
            skLineSegment(sketch, "E967.MirrorCS", {"start": v(458.43, -1108.47) * mm, "end": v(378.82, -1108.47) * mm});
            skPoint(sketch, "E968.MirrorP", {"position": v(445.15, -1004.47) * mm});
            skLineSegment(sketch, "E969.MirrorCS", {"start": v(453.43, -1108.47) * mm, "end": v(387.93, -1108.47) * mm});
            skPoint(sketch, "E970.MirrorP", {"position": v(387.93, -1108.47) * mm});
            skPoint(sketch, "E971.MirrorP", {"position": v(445.15, -1056.47) * mm});
            skLineSegment(sketch, "E972.MirrorCS", {"start": v(458.43, -974.32) * mm, "end": v(458.43, -1108.47) * mm});
            skPoint(sketch, "E973.MirrorP", {"position": v(445.15, -1082.47) * mm});
            skLineSegment(sketch, "E974.MirrorCS", {"start": v(312.49, -1186.47) * mm, "end": v(312.49, -1186.17) * mm});
            skLineSegment(sketch, "E975.MirrorCS", {"start": v(445.15, -1186.47) * mm, "end": v(445.15, -1186.17) * mm});
            skArc(sketch, "E976.MirrorCS", {"start": v(452.08, -1248.97) * mm, "mid": v(456.57, -1247.11) * mm, "end": v(458.43, -1242.62) * mm});
            skArc(sketch, "E977.MirrorCS", {"start": v(305.55, -1248.97) * mm, "mid": v(301.06, -1247.11) * mm, "end": v(299.2, -1242.62) * mm});
            skLineSegment(sketch, "E978.MirrorCS", {"start": v(458.43, -1242.62) * mm, "end": v(458.43, -1108.47) * mm});
            skPoint(sketch, "E979.MirrorP", {"position": v(445.15, -1212.47) * mm});
            skLineSegment(sketch, "E980.MirrorCS", {"start": v(305.55, -1248.97) * mm, "end": v(378.82, -1248.97) * mm});
            skLineSegment(sketch, "E981.MirrorCS", {"start": v(378.82, -1248.97) * mm, "end": v(378.82, -1238.47) * mm});
            skPoint(sketch, "E982.MirrorP", {"position": v(458.43, -1248.97) * mm});
            skPoint(sketch, "E983.MirrorP", {"position": v(445.15, -1160.47) * mm});
            skLineSegment(sketch, "E984.MirrorCS", {"start": v(452.08, -1248.97) * mm, "end": v(378.82, -1248.97) * mm});
            skPoint(sketch, "E985.MirrorP", {"position": v(445.15, -1134.47) * mm});
            skLineSegment(sketch, "E986.MirrorCS", {"start": v(299.2, -1242.62) * mm, "end": v(299.2, -1108.47) * mm});
            skPoint(sketch, "E987.MirrorP", {"position": v(299.2, -1248.97) * mm});
            skLineSegment(sketch, "E988.trimOffspring", {"start": v(369.7, -1108.47) * mm, "end": v(378.82, -1108.47) * mm});
            skLineSegment(sketch, "E989", {"start": v(378.82, -1108.47) * mm, "end": v(378.82, -1077.91) * mm});
            skCircle(sketch, "E990", {"center": v(316.5, -984.29) * mm, "radius": 2.8 * mm});
            skCircle(sketch, "E991.MirrorC", {"center": v(441.13, -984.29) * mm, "radius": 2.8 * mm});
            skCircle(sketch, "E992.MirrorC", {"center": v(316.5, -1232.66) * mm, "radius": 2.8 * mm});
            skCircle(sketch, "E993.MirrorC", {"center": v(441.13, -1232.66) * mm, "radius": 2.8 * mm});
            skCircle(sketch, "E994", {"center": v(316.5, -984.29) * mm, "radius": 3.8 * mm});
            skCircle(sketch, "E995", {"center": v(441.13, -984.29) * mm, "radius": 3.8 * mm});
            skCircle(sketch, "E996.MirrorC", {"center": v(316.5, -1232.66) * mm, "radius": 3.8 * mm});
            skCircle(sketch, "E997.MirrorC", {"center": v(441.13, -1232.66) * mm, "radius": 3.8 * mm});
            skLineSegment(sketch, "E998.top", {"start": v(35.85, -947.76) * mm, "end": v(55.55, -947.76) * mm});
            skLineSegment(sketch, "E998.left", {"start": v(35.85, -905.76) * mm, "end": v(35.85, -919.46) * mm});
            skLineSegment(sketch, "E999", {"start": v(75.85, -953.26) * mm, "end": v(75.85, -954.1) * mm});
            skLineSegment(sketch, "E1000", {"start": v(29.52, -933.76) * mm, "end": v(29.52, -926.76) * mm});
            skLineSegment(sketch, "E1001.MirrorCS", {"start": v(119.86, -954.1) * mm, "end": v(115.85, -954.1) * mm});
            skLineSegment(sketch, "E1002.MirrorCS", {"start": v(119.86, -953.26) * mm, "end": v(119.86, -954.1) * mm});
            skPoint(sketch, "E1003.end.orphan", {"position": v(95.85, -947.76) * mm});
            skPoint(sketch, "E1003.start.orphan", {"position": v(95.85, -954.1) * mm});
            skLineSegment(sketch, "E1004.trimOffspring", {"start": v(76.15, -947.76) * mm, "end": v(95.85, -947.76) * mm});
            skLineSegment(sketch, "E1005.trimOffspring", {"start": v(136.15, -947.76) * mm, "end": v(155.85, -947.76) * mm});
            skLineSegment(sketch, "E1006.trimOffspring", {"start": v(155.85, -934.06) * mm, "end": v(155.85, -947.76) * mm});
            skLineSegment(sketch, "E1007.trimOffspring", {"start": v(35.85, -934.06) * mm, "end": v(35.85, -947.76) * mm});
            skLineSegment(sketch, "E1008.MirrorCS", {"start": v(65.85, -899.43) * mm, "end": v(75.85, -899.43) * mm});
            skLineSegment(sketch, "E1009.MirrorCS", {"start": v(115.85, -899.43) * mm, "end": v(135.85, -899.43) * mm});
            skPoint(sketch, "E1010.start.orphan", {"position": v(29.52, -926.76) * mm});
            skLineSegment(sketch, "E1011.top", {"start": v(53.87, -899.43) * mm, "end": v(55.85, -899.43) * mm});
            skLineSegment(sketch, "E1011.left", {"start": v(35.85, -905.76) * mm, "end": v(35.85, -899.43) * mm});
            skLineSegment(sketch, "E1012.left", {"start": v(35.85, -899.43) * mm, "end": v(35.85, -905.76) * mm});
            skLineSegment(sketch, "E1012.right", {"start": v(155.85, -899.43) * mm, "end": v(155.85, -905.76) * mm});
            skLineSegment(sketch, "E1013", {"start": v(75.85, -936.8) * mm, "end": v(115.85, -936.8) * mm});
            skLineSegment(sketch, "E1014.left", {"start": v(75.85, -931.6) * mm, "end": v(75.85, -936.8) * mm});
            skLineSegment(sketch, "E1015", {"start": v(75.85, -936.8) * mm, "end": v(75.85, -931.6) * mm});
            skPoint(sketch, "E1016.firstSnap0", {"position": v(119.86, -934.2) * mm});
            skLineSegment(sketch, "E1016.top", {"start": v(115.85, -921.4) * mm, "end": v(75.85, -921.4) * mm});
            skLineSegment(sketch, "E1016.right", {"start": v(75.85, -926.6) * mm, "end": v(75.85, -921.4) * mm});
            skPoint(sketch, "E1017.orphan", {"position": v(75.85, -926.6) * mm});
            skLineSegment(sketch, "E1018", {"start": v(155.85, -899.43) * mm, "end": v(161.35, -899.43) * mm});
            skLineSegment(sketch, "E1019", {"start": v(161.35, -919.46) * mm, "end": v(161.35, -954.1) * mm});
            skLineSegment(sketch, "E1020", {"start": v(136.15, -953.26) * mm, "end": v(115.55, -953.26) * mm});
            skLineSegment(sketch, "E1021", {"start": v(30.35, -934.06) * mm, "end": v(30.35, -919.46) * mm});
            skLineSegment(sketch, "E1022", {"start": v(95.85, -947.76) * mm, "end": v(95.85, -939.24) * mm});
            skLineSegment(sketch, "E1023.MirrorCS", {"start": v(115.85, -936.8) * mm, "end": v(115.85, -931.6) * mm});
            skLineSegment(sketch, "E1024.MirrorCS", {"start": v(115.85, -926.6) * mm, "end": v(115.85, -921.4) * mm});
            skPoint(sketch, "E1025.orphan", {"position": v(119.86, -947.76) * mm});
            skPoint(sketch, "E1026.orphan", {"position": v(119.86, -936.8) * mm});
            skPoint(sketch, "E1027.orphan", {"position": v(119.86, -931.6) * mm});
            skLineSegment(sketch, "E1028", {"start": v(75.85, -931.6) * mm, "end": v(115.85, -931.6) * mm});
            skLineSegment(sketch, "E1029", {"start": v(115.85, -926.6) * mm, "end": v(75.85, -926.6) * mm});
            skPoint(sketch, "E1016.left.start.orphan", {"position": v(119.86, -926.6) * mm});
            skLineSegment(sketch, "E1030", {"start": v(95.85, -947.76) * mm, "end": v(115.85, -947.76) * mm});
            skLineSegment(sketch, "E1031", {"start": v(30.35, -919.46) * mm, "end": v(35.85, -919.46) * mm});
            skLineSegment(sketch, "E1032", {"start": v(29.52, -933.76) * mm, "end": v(29.52, -934.06) * mm});
            skLineSegment(sketch, "E1033", {"start": v(30.35, -934.06) * mm, "end": v(35.85, -934.06) * mm});
            skLineSegment(sketch, "E1034", {"start": v(55.85, -954.1) * mm, "end": v(53.87, -954.1) * mm});
            skLineSegment(sketch, "E1035.MirrorCS", {"start": v(162.18, -919.46) * mm, "end": v(155.85, -919.46) * mm});
            skLineSegment(sketch, "E1036.MirrorCS", {"start": v(161.35, -934.06) * mm, "end": v(155.85, -934.06) * mm});
            skLineSegment(sketch, "E1037", {"start": v(55.85, -954.1) * mm, "end": v(54.25, -954.1) * mm});
            skPoint(sketch, "E1038.end.orphan", {"position": v(29.52, -919.46) * mm});
            skPoint(sketch, "E1039.orphan", {"position": v(29.52, -919.76) * mm});
            skPoint(sketch, "E1040.orphan", {"position": v(35.85, -919.76) * mm});
            skPoint(sketch, "E1041.orphan", {"position": v(55.55, -954.1) * mm});
            skPoint(sketch, "E1042.orphan", {"position": v(76.15, -954.1) * mm});
            skLineSegment(sketch, "E1043.trimOffspring", {"start": v(76.15, -953.26) * mm, "end": v(55.55, -953.26) * mm});
            skPoint(sketch, "E1044.orphan", {"position": v(65.85, -954.1) * mm});
            skPoint(sketch, "E1045.orphan", {"position": v(75.85, -947.76) * mm});
            skPoint(sketch, "E1046.MirrorCS.end.orphan", {"position": v(115.85, -954.1) * mm});
            skPoint(sketch, "E1047.orphan", {"position": v(135.85, -954.1) * mm});
            skPoint(sketch, "E1048.orphan", {"position": v(162.18, -934.06) * mm});
            skLineSegment(sketch, "E1049", {"start": v(155.85, -919.46) * mm, "end": v(155.85, -905.76) * mm});
            skLineSegment(sketch, "E1050.bottom", {"start": v(75.85, -947.76) * mm, "end": v(76.15, -947.76) * mm});
            skLineSegment(sketch, "E1050.top", {"start": v(75.85, -953.26) * mm, "end": v(76.15, -953.26) * mm});
            skLineSegment(sketch, "E1050.left", {"start": v(75.85, -947.76) * mm, "end": v(75.85, -953.26) * mm});
            skLineSegment(sketch, "E1051.bottom", {"start": v(55.55, -947.76) * mm, "end": v(55.85, -947.76) * mm});
            skLineSegment(sketch, "E1051.top", {"start": v(55.55, -954.1) * mm, "end": v(55.85, -954.1) * mm});
            skLineSegment(sketch, "E1051.right", {"start": v(55.85, -947.76) * mm, "end": v(55.85, -954.1) * mm});
            skLineSegment(sketch, "E1052.bottom", {"start": v(115.85, -947.76) * mm, "end": v(115.55, -947.76) * mm});
            skLineSegment(sketch, "E1052.top", {"start": v(115.85, -953.26) * mm, "end": v(115.55, -953.26) * mm});
            skLineSegment(sketch, "E1052.left", {"start": v(115.85, -947.76) * mm, "end": v(115.85, -953.26) * mm});
            skLineSegment(sketch, "E1053.bottom", {"start": v(135.85, -954.1) * mm, "end": v(136.15, -954.1) * mm});
            skLineSegment(sketch, "E1053.top", {"start": v(135.85, -947.76) * mm, "end": v(136.15, -947.76) * mm});
            skLineSegment(sketch, "E1053.left", {"start": v(135.85, -954.1) * mm, "end": v(135.85, -947.76) * mm});
            skPoint(sketch, "E1054.MirrorCS.end.orphan", {"position": v(136.15, -954.1) * mm});
            skPoint(sketch, "E1055.orphan", {"position": v(115.55, -947.76) * mm});
            skPoint(sketch, "E1056.MirrorCS.end.orphan", {"position": v(115.55, -954.1) * mm});
            skLineSegment(sketch, "E1057", {"start": v(155.85, -926.76) * mm, "end": v(150.46, -926.76) * mm});
            skLineSegment(sketch, "E1058.MirrorCS", {"start": v(75.85, -900.26) * mm, "end": v(76.15, -900.26) * mm});
            skLineSegment(sketch, "E1059.MirrorCS", {"start": v(55.55, -899.43) * mm, "end": v(55.85, -899.43) * mm});
            skLineSegment(sketch, "E1060.MirrorCS", {"start": v(75.85, -900.26) * mm, "end": v(75.85, -899.43) * mm});
            skLineSegment(sketch, "E1061.MirrorCS", {"start": v(55.85, -899.43) * mm, "end": v(54.25, -899.43) * mm});
            skLineSegment(sketch, "E1062.MirrorCS", {"start": v(135.85, -905.76) * mm, "end": v(136.15, -905.76) * mm});
            skLineSegment(sketch, "E1063.MirrorCS", {"start": v(55.85, -899.43) * mm, "end": v(53.87, -899.43) * mm});
            skLineSegment(sketch, "E1064.MirrorCS", {"start": v(75.85, -905.76) * mm, "end": v(76.15, -905.76) * mm});
            skLineSegment(sketch, "E1065.MirrorCS", {"start": v(115.85, -905.76) * mm, "end": v(115.55, -905.76) * mm});
            skLineSegment(sketch, "E1066.MirrorCS", {"start": v(135.85, -899.43) * mm, "end": v(136.15, -899.43) * mm});
            skLineSegment(sketch, "E1067.MirrorCS", {"start": v(119.86, -899.43) * mm, "end": v(115.85, -899.43) * mm});
            skLineSegment(sketch, "E1068.MirrorCS", {"start": v(115.85, -900.26) * mm, "end": v(115.55, -900.26) * mm});
            skLineSegment(sketch, "E1069.MirrorCS", {"start": v(55.55, -905.76) * mm, "end": v(55.85, -905.76) * mm});
            skLineSegment(sketch, "E1070.MirrorCS", {"start": v(119.86, -900.26) * mm, "end": v(119.86, -899.43) * mm});
            skPoint(sketch, "E1071.MirrorP", {"position": v(135.85, -899.43) * mm});
            skPoint(sketch, "E1072.MirrorP", {"position": v(115.55, -905.76) * mm});
            skLineSegment(sketch, "E1073.MirrorCS", {"start": v(136.15, -905.76) * mm, "end": v(155.85, -905.76) * mm});
            skLineSegment(sketch, "E1074.MirrorCS", {"start": v(35.85, -905.76) * mm, "end": v(55.55, -905.76) * mm});
            skPoint(sketch, "E1075.MirrorP", {"position": v(95.85, -899.43) * mm});
            skLineSegment(sketch, "E1076.MirrorCS", {"start": v(75.85, -905.76) * mm, "end": v(75.85, -900.26) * mm});
            skLineSegment(sketch, "E1077.MirrorCS", {"start": v(76.15, -905.76) * mm, "end": v(95.85, -905.76) * mm});
            skPoint(sketch, "E1078.MirrorP", {"position": v(115.55, -899.43) * mm});
            skPoint(sketch, "E1079.MirrorP", {"position": v(65.85, -899.43) * mm});
            skPoint(sketch, "E1080.MirrorP", {"position": v(119.86, -905.76) * mm});
            skLineSegment(sketch, "E1081.MirrorCS", {"start": v(115.85, -905.76) * mm, "end": v(115.85, -900.26) * mm});
            skPoint(sketch, "E1082.MirrorP", {"position": v(75.85, -905.76) * mm});
            skLineSegment(sketch, "E1083.MirrorCS", {"start": v(135.85, -900.26) * mm, "end": v(135.85, -905.76) * mm});
            skLineSegment(sketch, "E1084.MirrorCS", {"start": v(95.85, -905.76) * mm, "end": v(115.85, -905.76) * mm});
            skPoint(sketch, "E1085.MirrorP", {"position": v(115.85, -899.43) * mm});
            skPoint(sketch, "E1086.MirrorP", {"position": v(76.15, -899.43) * mm});
            skPoint(sketch, "E1087.MirrorP", {"position": v(136.15, -899.43) * mm});
            skLineSegment(sketch, "E1088.MirrorCS", {"start": v(55.85, -905.76) * mm, "end": v(55.85, -899.43) * mm});
            skPoint(sketch, "E1089.MirrorP", {"position": v(55.55, -899.43) * mm});
            skLineSegment(sketch, "E1090.MirrorCS", {"start": v(136.15, -900.26) * mm, "end": v(115.55, -900.26) * mm});
            skLineSegment(sketch, "E1091.MirrorCS", {"start": v(76.15, -900.26) * mm, "end": v(55.55, -900.26) * mm});
            skPoint(sketch, "E1092.MirrorP", {"position": v(95.85, -905.76) * mm});
            skLineSegment(sketch, "E1093.trimOffspring", {"start": v(95.85, -899.43) * mm, "end": v(136.15, -899.43) * mm});
            skLineSegment(sketch, "E1094.trimOffspring", {"start": v(65.85, -899.43) * mm, "end": v(76.15, -899.43) * mm});
            skLineSegment(sketch, "E1095", {"start": v(-220.5, -973.9) * mm, "end": v(-220.2, -973.9) * mm});
            skLineSegment(sketch, "E1096", {"start": v(-220.2, -973.9) * mm, "end": v(-220.2, -969.4) * mm});
            skLineSegment(sketch, "E1097.MirrorCS", {"start": v(-220.2, -1233.9) * mm, "end": v(-220.2, -1238.4) * mm});
            skLineSegment(sketch, "E1098", {"start": v(-220.5, -1233.9) * mm, "end": v(-220.2, -1233.9) * mm});
            skLineSegment(sketch, "E1099.bottom", {"start": v(75.85, -971.26) * mm, "end": v(55.85, -971.26) * mm});
            skLineSegment(sketch, "E1099.top", {"start": v(75.85, -975.76) * mm, "end": v(55.85, -975.76) * mm});
            skLineSegment(sketch, "E1099.left", {"start": v(75.85, -971.26) * mm, "end": v(75.85, -975.76) * mm});
            skLineSegment(sketch, "E1099.right", {"start": v(55.85, -971.26) * mm, "end": v(55.85, -975.76) * mm});
            skLineSegment(sketch, "E1100", {"start": v(95.85, -947.76) * mm, "end": v(95.85, -954.1) * mm});
            skLineSegment(sketch, "E1101", {"start": v(32.7, -965.26) * mm, "end": v(95.85, -965.26) * mm});
            skLineSegment(sketch, "E1102.MirrorCS", {"start": v(155.85, -975.76) * mm, "end": v(160.35, -975.76) * mm});
            skLineSegment(sketch, "E1103.MirrorCS", {"start": v(155.85, -1001.46) * mm, "end": v(160.35, -1001.46) * mm});
            skLineSegment(sketch, "E1104.MirrorCS", {"start": v(105.74, -968.43) * mm, "end": v(106.04, -968.43) * mm});
            skLineSegment(sketch, "E1105.MirrorCS", {"start": v(115.85, -971.26) * mm, "end": v(115.85, -975.76) * mm});
            skLineSegment(sketch, "E1106.MirrorCS", {"start": v(106.04, -968.43) * mm, "end": v(105.74, -968.43) * mm});
            skLineSegment(sketch, "E1107.MirrorCS", {"start": v(165.35, -1105.76) * mm, "end": v(152.07, -1105.76) * mm});
            skLineSegment(sketch, "E1108.MirrorCS", {"start": v(160.35, -1001.46) * mm, "end": v(155.85, -1001.46) * mm});
            skLineSegment(sketch, "E1109.MirrorCS", {"start": v(160.35, -975.76) * mm, "end": v(155.85, -975.76) * mm});
            skLineSegment(sketch, "E1110.MirrorCS", {"start": v(152.07, -1027.76) * mm, "end": v(152.07, -1028.06) * mm});
            skLineSegment(sketch, "E1111.MirrorCS", {"start": v(160.35, -1028.06) * mm, "end": v(155.85, -1028.06) * mm});
            skLineSegment(sketch, "E1112.MirrorCS", {"start": v(135.85, -971.26) * mm, "end": v(135.85, -975.76) * mm});
            skLineSegment(sketch, "E1113.MirrorCS", {"start": v(160.35, -1053.46) * mm, "end": v(155.85, -1053.46) * mm});
            skLineSegment(sketch, "E1114.MirrorCS", {"start": v(160.35, -1080.06) * mm, "end": v(155.85, -1080.06) * mm});
            skLineSegment(sketch, "E1115.MirrorCS", {"start": v(125.44, -975.76) * mm, "end": v(115.85, -975.76) * mm});
            skLineSegment(sketch, "E1116.MirrorCS", {"start": v(160.35, -1105.76) * mm, "end": v(152.07, -1105.76) * mm});
            skLineSegment(sketch, "E1117.MirrorCS", {"start": v(106.04, -970.26) * mm, "end": v(106.04, -974.76) * mm});
            skLineSegment(sketch, "E1118.MirrorCS", {"start": v(155.85, -975.76) * mm, "end": v(155.85, -1001.46) * mm});
            skArc(sketch, "E1119.MirrorCS", {"start": v(159, -965.26) * mm, "mid": v(163.5, -967.12) * mm, "end": v(165.35, -971.61) * mm});
            skPoint(sketch, "E1120.MirrorP", {"position": v(165.35, -965.26) * mm});
            skLineSegment(sketch, "E1121.MirrorCS", {"start": v(160.35, -1080.06) * mm, "end": v(160.35, -1105.76) * mm});
            skLineSegment(sketch, "E1122.MirrorCS", {"start": v(155.85, -1001.46) * mm, "end": v(155.85, -974.76) * mm});
            skLineSegment(sketch, "E1123.MirrorCS", {"start": v(115.85, -975.76) * mm, "end": v(135.85, -975.76) * mm});
            skPoint(sketch, "E1124.MirrorP", {"position": v(161.18, -975.76) * mm});
            skLineSegment(sketch, "E1125.MirrorCS", {"start": v(159, -965.26) * mm, "end": v(95.85, -965.26) * mm});
            skLineSegment(sketch, "E1126.MirrorCS", {"start": v(160.35, -1028.06) * mm, "end": v(160.35, -1053.46) * mm});
            skPoint(sketch, "E1127.MirrorP", {"position": v(152.07, -1079.76) * mm});
            skLineSegment(sketch, "E1128.MirrorCS", {"start": v(155.85, -1053.46) * mm, "end": v(155.85, -1028.06) * mm});
            skLineSegment(sketch, "E1129.MirrorCS", {"start": v(125.44, -971.26) * mm, "end": v(115.85, -971.26) * mm});
            skLineSegment(sketch, "E1130.MirrorCS", {"start": v(160.35, -975.76) * mm, "end": v(160.35, -1001.46) * mm});
            skPoint(sketch, "E1131.MirrorP", {"position": v(152.07, -1053.76) * mm});
            skPoint(sketch, "E1132.MirrorP", {"position": v(152.07, -1001.76) * mm});
            skPoint(sketch, "E1133.MirrorP", {"position": v(155.85, -1027.76) * mm});
            skPoint(sketch, "E1134.MirrorP", {"position": v(125.74, -975.76) * mm});
            skLineSegment(sketch, "E1135.MirrorCS", {"start": v(115.85, -971.26) * mm, "end": v(135.85, -971.26) * mm});
            skPoint(sketch, "E1136.MirrorP", {"position": v(155.85, -1053.76) * mm});
            skLineSegment(sketch, "E1137.MirrorCS", {"start": v(155.85, -1105.76) * mm, "end": v(155.85, -1080.06) * mm});
            skCircle(sketch, "E1138.MirrorC", {"center": v(148.05, -981.58) * mm, "radius": 2.8 * mm});
            skLineSegment(sketch, "E1139.MirrorCS", {"start": v(165.35, -971.61) * mm, "end": v(165.35, -1105.76) * mm});
            skLineSegment(sketch, "E1140.MirrorCS", {"start": v(85.96, -1243.1) * mm, "end": v(85.66, -1243.1) * mm});
            skLineSegment(sketch, "E1141.MirrorCS", {"start": v(35.85, -1235.76) * mm, "end": v(31.35, -1235.76) * mm});
            skLineSegment(sketch, "E1142.MirrorCS", {"start": v(160.35, -1210.06) * mm, "end": v(155.85, -1210.06) * mm});
            skLineSegment(sketch, "E1143.MirrorCS", {"start": v(160.35, -1235.76) * mm, "end": v(155.85, -1235.76) * mm});
            skLineSegment(sketch, "E1144.MirrorCS", {"start": v(85.66, -1243.1) * mm, "end": v(85.96, -1243.1) * mm});
            skLineSegment(sketch, "E1145.MirrorCS", {"start": v(35.85, -1210.06) * mm, "end": v(31.35, -1210.06) * mm});
            skLineSegment(sketch, "E1146.MirrorCS", {"start": v(39.63, -1183.76) * mm, "end": v(39.63, -1183.46) * mm});
            skLineSegment(sketch, "E1147.MirrorCS", {"start": v(75.85, -1241.26) * mm, "end": v(75.85, -1236.76) * mm});
            skLineSegment(sketch, "E1148.MirrorCS", {"start": v(106.04, -1243.1) * mm, "end": v(105.74, -1243.1) * mm});
            skLineSegment(sketch, "E1149.MirrorCS", {"start": v(31.35, -1210.06) * mm, "end": v(35.85, -1210.06) * mm});
            skLineSegment(sketch, "E1150.MirrorCS", {"start": v(115.85, -1241.26) * mm, "end": v(115.85, -1236.76) * mm});
            skLineSegment(sketch, "E1151.MirrorCS", {"start": v(155.85, -1235.76) * mm, "end": v(160.35, -1235.76) * mm});
            skLineSegment(sketch, "E1152.MirrorCS", {"start": v(31.35, -1235.76) * mm, "end": v(35.85, -1235.76) * mm});
            skLineSegment(sketch, "E1153.MirrorCS", {"start": v(155.85, -1210.06) * mm, "end": v(160.35, -1210.06) * mm});
            skLineSegment(sketch, "E1154.MirrorCS", {"start": v(31.35, -1158.06) * mm, "end": v(35.85, -1158.06) * mm});
            skLineSegment(sketch, "E1155.MirrorCS", {"start": v(31.35, -1183.46) * mm, "end": v(35.85, -1183.46) * mm});
            skLineSegment(sketch, "E1156.MirrorCS", {"start": v(160.35, -1158.06) * mm, "end": v(155.85, -1158.06) * mm});
            skLineSegment(sketch, "E1157.MirrorCS", {"start": v(160.35, -1131.46) * mm, "end": v(155.85, -1131.46) * mm});
            skLineSegment(sketch, "E1158.MirrorCS", {"start": v(55.85, -1241.26) * mm, "end": v(55.85, -1236.76) * mm});
            skLineSegment(sketch, "E1159.MirrorCS", {"start": v(152.07, -1183.76) * mm, "end": v(152.07, -1183.46) * mm});
            skLineSegment(sketch, "E1160.MirrorCS", {"start": v(135.85, -1241.26) * mm, "end": v(135.85, -1236.76) * mm});
            skLineSegment(sketch, "E1161.MirrorCS", {"start": v(105.74, -1243.1) * mm, "end": v(106.04, -1243.1) * mm});
            skLineSegment(sketch, "E1162.MirrorCS", {"start": v(160.35, -1183.46) * mm, "end": v(155.85, -1183.46) * mm});
            skLineSegment(sketch, "E1163.MirrorCS", {"start": v(31.35, -1131.46) * mm, "end": v(35.85, -1131.46) * mm});
            skArc(sketch, "E1164.MirrorCS", {"start": v(159, -1246.26) * mm, "mid": v(163.5, -1244.4) * mm, "end": v(165.35, -1239.91) * mm});
            skArc(sketch, "E1165.MirrorCS", {"start": v(32.7, -1246.26) * mm, "mid": v(28.21, -1244.4) * mm, "end": v(26.35, -1239.91) * mm});
            skLineSegment(sketch, "E1166.MirrorCS", {"start": v(85.66, -1241.26) * mm, "end": v(85.66, -1236.76) * mm});
            skLineSegment(sketch, "E1167.MirrorCS", {"start": v(106.04, -1241.26) * mm, "end": v(106.04, -1236.76) * mm});
            skLineSegment(sketch, "E1168.MirrorCS", {"start": v(35.85, -1235.76) * mm, "end": v(35.85, -1210.06) * mm});
            skLineSegment(sketch, "E1169.MirrorCS", {"start": v(155.85, -1210.06) * mm, "end": v(155.85, -1236.76) * mm});
            skPoint(sketch, "E1170.MirrorP", {"position": v(35.85, -1183.76) * mm});
            skLineSegment(sketch, "E1171.MirrorCS", {"start": v(95.85, -1246.26) * mm, "end": v(95.85, -1105.76) * mm});
            skLineSegment(sketch, "E1172.MirrorCS", {"start": v(165.35, -1239.91) * mm, "end": v(165.35, -1105.76) * mm});
            skLineSegment(sketch, "E1173.MirrorCS", {"start": v(160.35, -1183.46) * mm, "end": v(160.35, -1158.06) * mm});
            skPoint(sketch, "E1174.MirrorP", {"position": v(161.18, -1235.76) * mm});
            skPoint(sketch, "E1175.MirrorP", {"position": v(165.35, -1246.26) * mm});
            skPoint(sketch, "E1176.MirrorP", {"position": v(152.07, -1131.76) * mm});
            skLineSegment(sketch, "E1177.MirrorCS", {"start": v(75.85, -1241.26) * mm, "end": v(66.26, -1241.26) * mm});
            skPoint(sketch, "E1178.MirrorP", {"position": v(39.63, -1131.76) * mm});
            skLineSegment(sketch, "E1179.MirrorCS", {"start": v(31.35, -1131.46) * mm, "end": v(31.35, -1105.76) * mm});
            skLineSegment(sketch, "E1180.MirrorCS", {"start": v(159, -1246.26) * mm, "end": v(95.85, -1246.26) * mm});
            skLineSegment(sketch, "E1181.MirrorCS", {"start": v(75.85, -1236.76) * mm, "end": v(65.96, -1236.76) * mm});
            skPoint(sketch, "E1182.MirrorP", {"position": v(125.74, -1236.76) * mm});
            skPoint(sketch, "E1183.MirrorP", {"position": v(155.85, -1157.76) * mm});
            skCircle(sketch, "E1184.MirrorC", {"center": v(43.65, -1229.95) * mm, "radius": 2.8 * mm});
            skLineSegment(sketch, "E1185.MirrorCS", {"start": v(155.85, -1105.76) * mm, "end": v(155.85, -1131.46) * mm});
            skPoint(sketch, "E1186.MirrorP", {"position": v(35.85, -1157.76) * mm});
            skPoint(sketch, "E1187.MirrorP", {"position": v(39.63, -1209.76) * mm});
            skPoint(sketch, "E1188.MirrorP", {"position": v(152.07, -1157.76) * mm});
            skCircle(sketch, "E1189.MirrorC", {"center": v(148.05, -1229.95) * mm, "radius": 2.8 * mm});
            skLineSegment(sketch, "E1190.MirrorCS", {"start": v(35.85, -1158.06) * mm, "end": v(35.85, -1183.46) * mm});
            skLineSegment(sketch, "E1191.MirrorCS", {"start": v(155.85, -1235.76) * mm, "end": v(155.85, -1210.06) * mm});
            skPoint(sketch, "E1192.MirrorP", {"position": v(65.96, -1236.76) * mm});
            skLineSegment(sketch, "E1193.MirrorCS", {"start": v(31.35, -1235.76) * mm, "end": v(31.35, -1210.06) * mm});
            skLineSegment(sketch, "E1194.MirrorCS", {"start": v(160.35, -1235.76) * mm, "end": v(160.35, -1210.06) * mm});
            skLineSegment(sketch, "E1195.MirrorCS", {"start": v(26.35, -1239.91) * mm, "end": v(26.35, -1105.76) * mm});
            skPoint(sketch, "E1196.MirrorP", {"position": v(30.52, -1235.76) * mm});
            skLineSegment(sketch, "E1197.MirrorCS", {"start": v(31.35, -1183.46) * mm, "end": v(31.35, -1158.06) * mm});
            skPoint(sketch, "E1198.MirrorP", {"position": v(39.63, -1157.76) * mm});
            skLineSegment(sketch, "E1199.MirrorCS", {"start": v(35.85, -1210.06) * mm, "end": v(35.85, -1236.76) * mm});
            skPoint(sketch, "E1200.MirrorP", {"position": v(26.35, -1246.26) * mm});
            skPoint(sketch, "E1201.MirrorP", {"position": v(152.07, -1209.76) * mm});
            skLineSegment(sketch, "E1202.MirrorCS", {"start": v(160.35, -1131.46) * mm, "end": v(160.35, -1105.76) * mm});
            skLineSegment(sketch, "E1203.MirrorCS", {"start": v(155.85, -1158.06) * mm, "end": v(155.85, -1183.46) * mm});
            skLineSegment(sketch, "E1204.MirrorCS", {"start": v(32.7, -1246.26) * mm, "end": v(95.85, -1246.26) * mm});
            skLineSegment(sketch, "E1205.MirrorCS", {"start": v(35.85, -1105.76) * mm, "end": v(35.85, -1131.46) * mm});
            skPoint(sketch, "E1206.MirrorP", {"position": v(155.85, -1183.76) * mm});
            skLineSegment(sketch, "E1207", {"start": v(65.96, -975.76) * mm, "end": v(66.26, -975.76) * mm});
            skLineSegment(sketch, "E1208.trimOffspring", {"start": v(115.85, -975.76) * mm, "end": v(125.74, -975.76) * mm});
            skLineSegment(sketch, "E1209", {"start": v(95.85, -1105.76) * mm, "end": v(110.49, -1105.76) * mm});
            skLineSegment(sketch, "E1210.MirrorCS", {"start": v(135.85, -1240.26) * mm, "end": v(135.85, -1235.76) * mm});
            skLineSegment(sketch, "E1211.MirrorCS", {"start": v(115.85, -1240.26) * mm, "end": v(115.85, -1235.76) * mm});
            skLineSegment(sketch, "E1212.MirrorCS", {"start": v(75.85, -1240.26) * mm, "end": v(75.85, -1235.76) * mm});
            skLineSegment(sketch, "E1213.MirrorCS", {"start": v(65.96, -1235.76) * mm, "end": v(66.26, -1235.76) * mm});
            skLineSegment(sketch, "E1214.MirrorCS", {"start": v(55.85, -1240.26) * mm, "end": v(55.85, -1235.76) * mm});
            skLineSegment(sketch, "E1215.MirrorCS", {"start": v(125.44, -1235.76) * mm, "end": v(115.85, -1235.76) * mm});
            skLineSegment(sketch, "E1216.MirrorCS", {"start": v(66.26, -1235.76) * mm, "end": v(75.85, -1235.76) * mm});
            skLineSegment(sketch, "E1217.MirrorCS", {"start": v(125.44, -1240.26) * mm, "end": v(115.85, -1240.26) * mm});
            skLineSegment(sketch, "E1218.MirrorCS", {"start": v(115.85, -1235.76) * mm, "end": v(125.74, -1235.76) * mm});
            skPoint(sketch, "E1219.MirrorP", {"position": v(65.96, -1235.76) * mm});
            skLineSegment(sketch, "E1220.MirrorCS", {"start": v(75.85, -1235.76) * mm, "end": v(55.85, -1235.76) * mm});
            skLineSegment(sketch, "E1221.MirrorCS", {"start": v(66.26, -1240.26) * mm, "end": v(75.85, -1240.26) * mm});
            skLineSegment(sketch, "E1222.MirrorCS", {"start": v(115.85, -1240.26) * mm, "end": v(135.85, -1240.26) * mm});
            skPoint(sketch, "E1223.MirrorP", {"position": v(125.74, -1235.76) * mm});
            skLineSegment(sketch, "E1224.MirrorCS", {"start": v(115.85, -1235.76) * mm, "end": v(135.85, -1235.76) * mm});
            skLineSegment(sketch, "E1225.MirrorCS", {"start": v(75.85, -1240.26) * mm, "end": v(55.85, -1240.26) * mm});
            skLineSegment(sketch, "E1226", {"start": v(544.67, -1032.72) * mm, "end": v(544.67, -1033.02) * mm});
            skPoint(sketch, "E1227.MirrorCS.end.orphan", {"position": v(601.89, -1110.72) * mm});
            skPoint(sketch, "E1228.MirrorCS.start.orphan", {"position": v(611, -1110.72) * mm});
            skLineSegment(sketch, "E1229.bottom", {"start": v(537.74, -970.22) * mm, "end": v(611, -970.22) * mm});
            skLineSegment(sketch, "E1229.left", {"start": v(531.39, -976.57) * mm, "end": v(531.39, -1110.72) * mm});
            skLineSegment(sketch, "E1229.right", {"start": v(611, -970.22) * mm, "end": v(611, -980.72) * mm});
            skPoint(sketch, "E1230.visualSharp", {"position": v(531.39, -970.22) * mm});
            skArc(sketch, "E1230.filletArc", {"start": v(537.74, -970.22) * mm, "mid": v(533.25, -972.08) * mm, "end": v(531.39, -976.57) * mm});
            skLineSegment(sketch, "E1231.MirrorCS", {"start": v(677.33, -1032.72) * mm, "end": v(677.33, -1033.02) * mm});
            skPoint(sketch, "E1232.MirrorP", {"position": v(677.33, -1110.72) * mm});
            skArc(sketch, "E1233.MirrorCS", {"start": v(684.27, -970.22) * mm, "mid": v(688.76, -972.08) * mm, "end": v(690.62, -976.57) * mm});
            skLineSegment(sketch, "E1234.MirrorCS", {"start": v(684.27, -970.22) * mm, "end": v(611, -970.22) * mm});
            skPoint(sketch, "E1235.MirrorP", {"position": v(690.62, -970.22) * mm});
            skLineSegment(sketch, "E1236.MirrorCS", {"start": v(690.62, -1110.72) * mm, "end": v(611, -1110.72) * mm});
            skPoint(sketch, "E1237.MirrorP", {"position": v(677.33, -1006.72) * mm});
            skLineSegment(sketch, "E1238.MirrorCS", {"start": v(685.62, -1110.72) * mm, "end": v(620.12, -1110.72) * mm});
            skPoint(sketch, "E1239.MirrorP", {"position": v(620.12, -1110.72) * mm});
            skPoint(sketch, "E1240.MirrorP", {"position": v(677.33, -1058.72) * mm});
            skLineSegment(sketch, "E1241.MirrorCS", {"start": v(690.62, -976.57) * mm, "end": v(690.62, -1110.72) * mm});
            skPoint(sketch, "E1242.MirrorP", {"position": v(677.33, -1084.72) * mm});
            skLineSegment(sketch, "E1243.MirrorCS", {"start": v(544.67, -1188.72) * mm, "end": v(544.67, -1188.42) * mm});
            skLineSegment(sketch, "E1244.MirrorCS", {"start": v(677.33, -1188.72) * mm, "end": v(677.33, -1188.42) * mm});
            skArc(sketch, "E1245.MirrorCS", {"start": v(684.27, -1251.22) * mm, "mid": v(688.76, -1249.36) * mm, "end": v(690.62, -1244.87) * mm});
            skArc(sketch, "E1246.MirrorCS", {"start": v(537.74, -1251.22) * mm, "mid": v(533.25, -1249.36) * mm, "end": v(531.39, -1244.87) * mm});
            skLineSegment(sketch, "E1247.MirrorCS", {"start": v(690.62, -1244.87) * mm, "end": v(690.62, -1110.72) * mm});
            skPoint(sketch, "E1248.MirrorP", {"position": v(677.33, -1214.72) * mm});
            skLineSegment(sketch, "E1249.MirrorCS", {"start": v(537.74, -1251.22) * mm, "end": v(611, -1251.22) * mm});
            skLineSegment(sketch, "E1250.MirrorCS", {"start": v(611, -1251.22) * mm, "end": v(611, -1240.72) * mm});
            skPoint(sketch, "E1251.MirrorP", {"position": v(690.62, -1251.22) * mm});
            skPoint(sketch, "E1252.MirrorP", {"position": v(677.33, -1162.72) * mm});
            skLineSegment(sketch, "E1253.MirrorCS", {"start": v(684.27, -1251.22) * mm, "end": v(611, -1251.22) * mm});
            skPoint(sketch, "E1254.MirrorP", {"position": v(677.33, -1136.72) * mm});
            skLineSegment(sketch, "E1255.MirrorCS", {"start": v(531.39, -1244.87) * mm, "end": v(531.39, -1110.72) * mm});
            skPoint(sketch, "E1256.MirrorP", {"position": v(531.39, -1251.22) * mm});
            skLineSegment(sketch, "E1257.trimOffspring", {"start": v(601.89, -1110.72) * mm, "end": v(611, -1110.72) * mm});
            skLineSegment(sketch, "E1258", {"start": v(611, -1110.72) * mm, "end": v(611, -1080.16) * mm});
            skLineSegment(sketch, "E1259.top", {"start": v(71.65, -1377.66) * mm, "end": v(81.24, -1377.66) * mm});
            skPoint(sketch, "E1260.end.orphan", {"position": v(35.91, -1377.66) * mm});
            skLineSegment(sketch, "E1261.bottom", {"start": v(36.74, -1377.66) * mm, "end": v(41.24, -1377.66) * mm});
            skLineSegment(sketch, "E1262.trimOffspring", {"start": v(41.24, -1507.66) * mm, "end": v(41.24, -1481.96) * mm});
            skLineSegment(sketch, "E1263.trimOffspring", {"start": v(41.24, -1455.36) * mm, "end": v(41.24, -1429.96) * mm});
            skLineSegment(sketch, "E1264.trimOffspring", {"start": v(41.24, -1403.36) * mm, "end": v(41.24, -1376.66) * mm});
            skLineSegment(sketch, "E1265", {"start": v(91.35, -1370.33) * mm, "end": v(91.05, -1370.33) * mm});
            skLineSegment(sketch, "E1266.bottom", {"start": v(91.05, -1370.33) * mm, "end": v(91.35, -1370.33) * mm});
            skLineSegment(sketch, "E1266.left", {"start": v(91.05, -1372.16) * mm, "end": v(91.05, -1376.66) * mm});
            skLineSegment(sketch, "E1267", {"start": v(36.74, -1403.36) * mm, "end": v(41.24, -1403.36) * mm});
            skLineSegment(sketch, "E1268", {"start": v(45.02, -1429.66) * mm, "end": v(45.02, -1429.96) * mm});
            skLineSegment(sketch, "E1269", {"start": v(36.74, -1429.96) * mm, "end": v(41.24, -1429.96) * mm});
            skLineSegment(sketch, "E1270", {"start": v(36.74, -1455.36) * mm, "end": v(41.24, -1455.36) * mm});
            skLineSegment(sketch, "E1271", {"start": v(36.74, -1481.96) * mm, "end": v(41.24, -1481.96) * mm});
            skPoint(sketch, "E1272.end.orphan", {"position": v(71.35, -1377.66) * mm});
            skPoint(sketch, "E1273.orphan", {"position": v(41.24, -1429.66) * mm});
            skPoint(sketch, "E1274.orphan", {"position": v(41.24, -1455.66) * mm});
            skPoint(sketch, "E1275.start.orphan", {"position": v(45.02, -1403.66) * mm});
            skPoint(sketch, "E1276.trimOffspring.end.orphan", {"position": v(45.02, -1455.66) * mm});
            skPoint(sketch, "E1277.start.orphan", {"position": v(45.02, -1481.66) * mm});
            skLineSegment(sketch, "E1278.top", {"start": v(36.74, -1507.66) * mm, "end": v(45.02, -1507.66) * mm});
            skLineSegment(sketch, "E1279.top", {"start": v(31.74, -1507.66) * mm, "end": v(45.02, -1507.66) * mm});
            skLineSegment(sketch, "E1279.left", {"start": v(31.74, -1373.51) * mm, "end": v(31.74, -1507.66) * mm});
            skLineSegment(sketch, "E1280.bottom", {"start": v(41.24, -1377.66) * mm, "end": v(36.74, -1377.66) * mm});
            skLineSegment(sketch, "E1280.top", {"start": v(41.24, -1403.36) * mm, "end": v(36.74, -1403.36) * mm});
            skLineSegment(sketch, "E1280.left", {"start": v(41.24, -1377.66) * mm, "end": v(41.24, -1403.36) * mm});
            skLineSegment(sketch, "E1280.right", {"start": v(36.74, -1377.66) * mm, "end": v(36.74, -1403.36) * mm});
            skLineSegment(sketch, "E1281.trimOffspring", {"start": v(36.74, -1481.96) * mm, "end": v(36.74, -1507.66) * mm});
            skLineSegment(sketch, "E1282.trimOffspring", {"start": v(36.74, -1429.96) * mm, "end": v(36.74, -1455.36) * mm});
            skLineSegment(sketch, "E1283", {"start": v(71.65, -1373.16) * mm, "end": v(81.24, -1373.16) * mm});
            skPoint(sketch, "E1284.visualSharp", {"position": v(31.74, -1367.16) * mm});
            skArc(sketch, "E1284.filletArc", {"start": v(38.1, -1367.16) * mm, "mid": v(33.6, -1369.02) * mm, "end": v(31.74, -1373.51) * mm});
            skPoint(sketch, "E1285.start.orphan", {"position": v(101.24, -1356) * mm});
            skPoint(sketch, "E1286.orphan", {"position": v(60.94, -1356) * mm});
            skPoint(sketch, "E1287.orphan", {"position": v(81.54, -1356) * mm});
            skPoint(sketch, "E1288.orphan", {"position": v(71.24, -1356) * mm});
            skPoint(sketch, "E1289.MirrorCS.end.orphan", {"position": v(121.24, -1356) * mm});
            skPoint(sketch, "E1290.orphan", {"position": v(141.24, -1356) * mm});
            skPoint(sketch, "E1291.MirrorCS.end.orphan", {"position": v(141.54, -1356) * mm});
            skPoint(sketch, "E1292.MirrorCS.end.orphan", {"position": v(120.94, -1356) * mm});
            skLineSegment(sketch, "E1293.bottom", {"start": v(81.24, -1373.16) * mm, "end": v(61.24, -1373.16) * mm});
            skLineSegment(sketch, "E1293.top", {"start": v(81.24, -1377.66) * mm, "end": v(61.24, -1377.66) * mm});
            skLineSegment(sketch, "E1293.left", {"start": v(81.24, -1373.16) * mm, "end": v(81.24, -1377.66) * mm});
            skLineSegment(sketch, "E1293.right", {"start": v(61.24, -1373.16) * mm, "end": v(61.24, -1377.66) * mm});
            skLineSegment(sketch, "E1294", {"start": v(38.1, -1367.16) * mm, "end": v(101.24, -1367.16) * mm});
            skLineSegment(sketch, "E1295.MirrorCS", {"start": v(161.24, -1377.66) * mm, "end": v(165.74, -1377.66) * mm});
            skLineSegment(sketch, "E1296.MirrorCS", {"start": v(161.24, -1403.36) * mm, "end": v(165.74, -1403.36) * mm});
            skLineSegment(sketch, "E1297.MirrorCS", {"start": v(111.13, -1370.33) * mm, "end": v(111.43, -1370.33) * mm});
            skLineSegment(sketch, "E1298.MirrorCS", {"start": v(121.24, -1373.16) * mm, "end": v(121.24, -1377.66) * mm});
            skLineSegment(sketch, "E1299.MirrorCS", {"start": v(111.43, -1370.33) * mm, "end": v(111.13, -1370.33) * mm});
            skLineSegment(sketch, "E1300.MirrorCS", {"start": v(170.74, -1507.66) * mm, "end": v(157.46, -1507.66) * mm});
            skLineSegment(sketch, "E1301.MirrorCS", {"start": v(165.74, -1403.36) * mm, "end": v(161.24, -1403.36) * mm});
            skLineSegment(sketch, "E1302.MirrorCS", {"start": v(165.74, -1377.66) * mm, "end": v(161.24, -1377.66) * mm});
            skLineSegment(sketch, "E1303.MirrorCS", {"start": v(157.46, -1429.66) * mm, "end": v(157.46, -1429.96) * mm});
            skLineSegment(sketch, "E1304.MirrorCS", {"start": v(165.74, -1429.96) * mm, "end": v(161.24, -1429.96) * mm});
            skLineSegment(sketch, "E1305.MirrorCS", {"start": v(141.24, -1373.16) * mm, "end": v(141.24, -1377.66) * mm});
            skLineSegment(sketch, "E1306.MirrorCS", {"start": v(165.74, -1455.36) * mm, "end": v(161.24, -1455.36) * mm});
            skLineSegment(sketch, "E1307.MirrorCS", {"start": v(165.74, -1481.96) * mm, "end": v(161.24, -1481.96) * mm});
            skLineSegment(sketch, "E1308.MirrorCS", {"start": v(130.83, -1377.66) * mm, "end": v(121.24, -1377.66) * mm});
            skLineSegment(sketch, "E1309.MirrorCS", {"start": v(165.74, -1507.66) * mm, "end": v(157.46, -1507.66) * mm});
            skLineSegment(sketch, "E1310.MirrorCS", {"start": v(111.43, -1372.16) * mm, "end": v(111.43, -1376.66) * mm});
            skLineSegment(sketch, "E1311.MirrorCS", {"start": v(161.24, -1377.66) * mm, "end": v(161.24, -1403.36) * mm});
            skArc(sketch, "E1312.MirrorCS", {"start": v(164.4, -1367.16) * mm, "mid": v(168.88, -1369.02) * mm, "end": v(170.74, -1373.51) * mm});
            skPoint(sketch, "E1313.MirrorP", {"position": v(170.74, -1367.16) * mm});
            skLineSegment(sketch, "E1314.MirrorCS", {"start": v(165.74, -1481.96) * mm, "end": v(165.74, -1507.66) * mm});
            skLineSegment(sketch, "E1315.MirrorCS", {"start": v(161.24, -1403.36) * mm, "end": v(161.24, -1376.66) * mm});
            skLineSegment(sketch, "E1316.MirrorCS", {"start": v(121.24, -1377.66) * mm, "end": v(141.24, -1377.66) * mm});
            skPoint(sketch, "E1317.MirrorP", {"position": v(166.57, -1377.66) * mm});
            skLineSegment(sketch, "E1318.MirrorCS", {"start": v(164.4, -1367.16) * mm, "end": v(101.24, -1367.16) * mm});
            skLineSegment(sketch, "E1319.MirrorCS", {"start": v(165.74, -1429.96) * mm, "end": v(165.74, -1455.36) * mm});
            skPoint(sketch, "E1320.MirrorP", {"position": v(157.46, -1481.66) * mm});
            skLineSegment(sketch, "E1321.MirrorCS", {"start": v(161.24, -1455.36) * mm, "end": v(161.24, -1429.96) * mm});
            skLineSegment(sketch, "E1322.MirrorCS", {"start": v(130.83, -1373.16) * mm, "end": v(121.24, -1373.16) * mm});
            skLineSegment(sketch, "E1323.MirrorCS", {"start": v(165.74, -1377.66) * mm, "end": v(165.74, -1403.36) * mm});
            skPoint(sketch, "E1324.MirrorP", {"position": v(157.46, -1455.66) * mm});
            skPoint(sketch, "E1325.MirrorP", {"position": v(157.46, -1403.66) * mm});
            skPoint(sketch, "E1326.MirrorP", {"position": v(161.24, -1429.66) * mm});
            skPoint(sketch, "E1327.MirrorP", {"position": v(131.13, -1377.66) * mm});
            skLineSegment(sketch, "E1328.MirrorCS", {"start": v(121.24, -1373.16) * mm, "end": v(141.24, -1373.16) * mm});
            skPoint(sketch, "E1329.MirrorP", {"position": v(161.24, -1455.66) * mm});
            skLineSegment(sketch, "E1330.MirrorCS", {"start": v(161.24, -1507.66) * mm, "end": v(161.24, -1481.96) * mm});
            skLineSegment(sketch, "E1331.MirrorCS", {"start": v(170.74, -1373.51) * mm, "end": v(170.74, -1507.66) * mm});
            skLineSegment(sketch, "E1332.MirrorCS", {"start": v(91.35, -1645) * mm, "end": v(91.05, -1645) * mm});
            skLineSegment(sketch, "E1333.MirrorCS", {"start": v(41.24, -1637.66) * mm, "end": v(36.74, -1637.66) * mm});
            skLineSegment(sketch, "E1334.MirrorCS", {"start": v(165.74, -1611.96) * mm, "end": v(161.24, -1611.96) * mm});
            skLineSegment(sketch, "E1335.MirrorCS", {"start": v(165.74, -1637.66) * mm, "end": v(161.24, -1637.66) * mm});
            skLineSegment(sketch, "E1336.MirrorCS", {"start": v(91.05, -1645) * mm, "end": v(91.35, -1645) * mm});
            skLineSegment(sketch, "E1337.MirrorCS", {"start": v(41.24, -1611.96) * mm, "end": v(36.74, -1611.96) * mm});
            skLineSegment(sketch, "E1338.MirrorCS", {"start": v(45.02, -1585.66) * mm, "end": v(45.02, -1585.36) * mm});
            skLineSegment(sketch, "E1339.MirrorCS", {"start": v(81.24, -1643.16) * mm, "end": v(81.24, -1638.66) * mm});
            skLineSegment(sketch, "E1340.MirrorCS", {"start": v(111.43, -1645) * mm, "end": v(111.13, -1645) * mm});
            skLineSegment(sketch, "E1341.MirrorCS", {"start": v(36.74, -1611.96) * mm, "end": v(41.24, -1611.96) * mm});
            skLineSegment(sketch, "E1342.MirrorCS", {"start": v(121.24, -1643.16) * mm, "end": v(121.24, -1638.66) * mm});
            skLineSegment(sketch, "E1343.MirrorCS", {"start": v(161.24, -1637.66) * mm, "end": v(165.74, -1637.66) * mm});
            skLineSegment(sketch, "E1344.MirrorCS", {"start": v(36.74, -1637.66) * mm, "end": v(41.24, -1637.66) * mm});
            skLineSegment(sketch, "E1345.MirrorCS", {"start": v(161.24, -1611.96) * mm, "end": v(165.74, -1611.96) * mm});
            skLineSegment(sketch, "E1346.MirrorCS", {"start": v(36.74, -1559.96) * mm, "end": v(41.24, -1559.96) * mm});
            skLineSegment(sketch, "E1347.MirrorCS", {"start": v(36.74, -1585.36) * mm, "end": v(41.24, -1585.36) * mm});
            skLineSegment(sketch, "E1348.MirrorCS", {"start": v(165.74, -1559.96) * mm, "end": v(161.24, -1559.96) * mm});
            skLineSegment(sketch, "E1349.MirrorCS", {"start": v(165.74, -1533.36) * mm, "end": v(161.24, -1533.36) * mm});
            skLineSegment(sketch, "E1350.MirrorCS", {"start": v(61.24, -1643.16) * mm, "end": v(61.24, -1638.66) * mm});
            skLineSegment(sketch, "E1351.MirrorCS", {"start": v(157.46, -1585.66) * mm, "end": v(157.46, -1585.36) * mm});
            skLineSegment(sketch, "E1352.MirrorCS", {"start": v(141.24, -1643.16) * mm, "end": v(141.24, -1638.66) * mm});
            skLineSegment(sketch, "E1353.MirrorCS", {"start": v(111.13, -1645) * mm, "end": v(111.43, -1645) * mm});
            skLineSegment(sketch, "E1354.MirrorCS", {"start": v(165.74, -1585.36) * mm, "end": v(161.24, -1585.36) * mm});
            skLineSegment(sketch, "E1355.MirrorCS", {"start": v(36.74, -1533.36) * mm, "end": v(41.24, -1533.36) * mm});
            skArc(sketch, "E1356.MirrorCS", {"start": v(164.4, -1648.16) * mm, "mid": v(168.88, -1646.3) * mm, "end": v(170.74, -1641.81) * mm});
            skArc(sketch, "E1357.MirrorCS", {"start": v(38.1, -1648.16) * mm, "mid": v(33.6, -1646.3) * mm, "end": v(31.74, -1641.81) * mm});
            skLineSegment(sketch, "E1358.MirrorCS", {"start": v(91.05, -1643.16) * mm, "end": v(91.05, -1638.66) * mm});
            skLineSegment(sketch, "E1359.MirrorCS", {"start": v(111.43, -1643.16) * mm, "end": v(111.43, -1638.66) * mm});
            skLineSegment(sketch, "E1360.MirrorCS", {"start": v(41.24, -1637.66) * mm, "end": v(41.24, -1611.96) * mm});
            skLineSegment(sketch, "E1361.MirrorCS", {"start": v(161.24, -1611.96) * mm, "end": v(161.24, -1638.66) * mm});
            skPoint(sketch, "E1362.MirrorP", {"position": v(41.24, -1585.66) * mm});
            skLineSegment(sketch, "E1363.MirrorCS", {"start": v(101.24, -1628.64) * mm, "end": v(101.24, -1507.66) * mm});
            skLineSegment(sketch, "E1364.MirrorCS", {"start": v(170.74, -1641.81) * mm, "end": v(170.74, -1507.66) * mm});
            skLineSegment(sketch, "E1365.MirrorCS", {"start": v(165.74, -1585.36) * mm, "end": v(165.74, -1559.96) * mm});
            skPoint(sketch, "E1366.MirrorP", {"position": v(166.57, -1637.66) * mm});
            skPoint(sketch, "E1367.MirrorP", {"position": v(170.74, -1648.16) * mm});
            skPoint(sketch, "E1368.MirrorP", {"position": v(157.46, -1533.66) * mm});
            skLineSegment(sketch, "E1369.MirrorCS", {"start": v(81.24, -1643.16) * mm, "end": v(71.65, -1643.16) * mm});
            skPoint(sketch, "E1370.MirrorP", {"position": v(45.02, -1533.66) * mm});
            skLineSegment(sketch, "E1371.MirrorCS", {"start": v(36.74, -1533.36) * mm, "end": v(36.74, -1507.66) * mm});
            skLineSegment(sketch, "E1372.MirrorCS", {"start": v(164.4, -1648.16) * mm, "end": v(101.24, -1648.16) * mm});
            skLineSegment(sketch, "E1373.MirrorCS", {"start": v(81.24, -1638.66) * mm, "end": v(71.35, -1638.66) * mm});
            skPoint(sketch, "E1374.MirrorP", {"position": v(131.13, -1638.66) * mm});
            skPoint(sketch, "E1375.MirrorP", {"position": v(161.24, -1559.66) * mm});
            skCircle(sketch, "E1376.MirrorC", {"center": v(49.04, -1631.85) * mm, "radius": 2.8 * mm});
            skLineSegment(sketch, "E1377.MirrorCS", {"start": v(161.24, -1507.66) * mm, "end": v(161.24, -1533.36) * mm});
            skPoint(sketch, "E1378.MirrorP", {"position": v(41.24, -1559.66) * mm});
            skPoint(sketch, "E1379.MirrorP", {"position": v(45.02, -1611.66) * mm});
            skPoint(sketch, "E1380.MirrorP", {"position": v(157.46, -1559.66) * mm});
            skCircle(sketch, "E1381.MirrorC", {"center": v(153.44, -1631.85) * mm, "radius": 2.8 * mm});
            skLineSegment(sketch, "E1382.MirrorCS", {"start": v(41.24, -1559.96) * mm, "end": v(41.24, -1585.36) * mm});
            skLineSegment(sketch, "E1383.MirrorCS", {"start": v(161.24, -1637.66) * mm, "end": v(161.24, -1611.96) * mm});
            skPoint(sketch, "E1384.MirrorP", {"position": v(71.35, -1638.66) * mm});
            skLineSegment(sketch, "E1385.MirrorCS", {"start": v(36.74, -1637.66) * mm, "end": v(36.74, -1611.96) * mm});
            skLineSegment(sketch, "E1386.MirrorCS", {"start": v(165.74, -1637.66) * mm, "end": v(165.74, -1611.96) * mm});
            skLineSegment(sketch, "E1387.MirrorCS", {"start": v(31.74, -1641.81) * mm, "end": v(31.74, -1507.66) * mm});
            skPoint(sketch, "E1388.MirrorP", {"position": v(35.91, -1637.66) * mm});
            skLineSegment(sketch, "E1389.MirrorCS", {"start": v(36.74, -1585.36) * mm, "end": v(36.74, -1559.96) * mm});
            skPoint(sketch, "E1390.MirrorP", {"position": v(45.02, -1559.66) * mm});
            skLineSegment(sketch, "E1391.MirrorCS", {"start": v(41.24, -1611.96) * mm, "end": v(41.24, -1638.66) * mm});
            skPoint(sketch, "E1392.MirrorP", {"position": v(31.74, -1648.16) * mm});
            skPoint(sketch, "E1393.MirrorP", {"position": v(157.46, -1611.66) * mm});
            skLineSegment(sketch, "E1394.MirrorCS", {"start": v(165.74, -1533.36) * mm, "end": v(165.74, -1507.66) * mm});
            skLineSegment(sketch, "E1395.MirrorCS", {"start": v(161.24, -1559.96) * mm, "end": v(161.24, -1585.36) * mm});
            skLineSegment(sketch, "E1396.MirrorCS", {"start": v(38.1, -1648.16) * mm, "end": v(101.24, -1648.16) * mm});
            skLineSegment(sketch, "E1397.MirrorCS", {"start": v(41.24, -1507.66) * mm, "end": v(41.24, -1533.36) * mm});
            skPoint(sketch, "E1398.MirrorP", {"position": v(161.24, -1585.66) * mm});
            skLineSegment(sketch, "E1399", {"start": v(71.35, -1377.66) * mm, "end": v(71.65, -1377.66) * mm});
            skLineSegment(sketch, "E1400.trimOffspring", {"start": v(121.24, -1377.66) * mm, "end": v(131.13, -1377.66) * mm});
            skLineSegment(sketch, "E1401", {"start": v(101.24, -1507.66) * mm, "end": v(115.88, -1507.66) * mm});
            skLineSegment(sketch, "E1402.MirrorCS", {"start": v(141.24, -1642.16) * mm, "end": v(141.24, -1637.66) * mm});
            skLineSegment(sketch, "E1403.MirrorCS", {"start": v(121.24, -1642.16) * mm, "end": v(121.24, -1637.66) * mm});
            skLineSegment(sketch, "E1404.MirrorCS", {"start": v(81.24, -1642.16) * mm, "end": v(81.24, -1637.66) * mm});
            skLineSegment(sketch, "E1405.MirrorCS", {"start": v(71.35, -1637.66) * mm, "end": v(71.65, -1637.66) * mm});
            skLineSegment(sketch, "E1406.MirrorCS", {"start": v(61.24, -1642.16) * mm, "end": v(61.24, -1637.66) * mm});
            skLineSegment(sketch, "E1407.MirrorCS", {"start": v(130.83, -1637.66) * mm, "end": v(121.24, -1637.66) * mm});
            skLineSegment(sketch, "E1408.MirrorCS", {"start": v(71.65, -1637.66) * mm, "end": v(81.24, -1637.66) * mm});
            skLineSegment(sketch, "E1409.MirrorCS", {"start": v(130.83, -1642.16) * mm, "end": v(121.24, -1642.16) * mm});
            skLineSegment(sketch, "E1410.MirrorCS", {"start": v(121.24, -1637.66) * mm, "end": v(131.13, -1637.66) * mm});
            skPoint(sketch, "E1411.MirrorP", {"position": v(71.35, -1637.66) * mm});
            skLineSegment(sketch, "E1412.MirrorCS", {"start": v(81.24, -1637.66) * mm, "end": v(61.24, -1637.66) * mm});
            skLineSegment(sketch, "E1413.MirrorCS", {"start": v(71.65, -1642.16) * mm, "end": v(81.24, -1642.16) * mm});
            skLineSegment(sketch, "E1414.MirrorCS", {"start": v(121.24, -1642.16) * mm, "end": v(141.24, -1642.16) * mm});
            skPoint(sketch, "E1415.MirrorP", {"position": v(131.13, -1637.66) * mm});
            skLineSegment(sketch, "E1416.MirrorCS", {"start": v(121.24, -1637.66) * mm, "end": v(141.24, -1637.66) * mm});
            skLineSegment(sketch, "E1417.MirrorCS", {"start": v(81.24, -1642.16) * mm, "end": v(61.24, -1642.16) * mm});
            skLineSegment(sketch, "E1418", {"start": v(101.24, -1507.66) * mm, "end": v(101.24, -1386.69) * mm});
            skLineSegment(sketch, "E1419", {"start": v(101.24, -1507.66) * mm, "end": v(54.46, -1507.66) * mm});
            skLineSegment(sketch, "E1420.bottom", {"start": v(54.46, -1507.66) * mm, "end": v(101.24, -1507.66) * mm});
            skLineSegment(sketch, "E1420.top", {"start": v(59.46, -1386.69) * mm, "end": v(101.24, -1386.69) * mm});
            skLineSegment(sketch, "E1420.left", {"start": v(54.46, -1507.66) * mm, "end": v(54.46, -1391.69) * mm});
            skLineSegment(sketch, "E1421.MirrorCS", {"start": v(143.02, -1386.69) * mm, "end": v(101.24, -1386.69) * mm});
            skLineSegment(sketch, "E1422.MirrorCS", {"start": v(148.02, -1507.66) * mm, "end": v(148.02, -1386.69) * mm});
            skLineSegment(sketch, "E1423.MirrorCS", {"start": v(148.02, -1507.66) * mm, "end": v(148.02, -1391.69) * mm});
            skLineSegment(sketch, "E1424.MirrorCS", {"start": v(54.46, -1507.66) * mm, "end": v(54.46, -1623.64) * mm});
            skLineSegment(sketch, "E1425.MirrorCS", {"start": v(54.46, -1628.64) * mm, "end": v(101.24, -1628.64) * mm});
            skLineSegment(sketch, "E1426.MirrorCS", {"start": v(143.02, -1628.64) * mm, "end": v(101.24, -1628.64) * mm});
            skLineSegment(sketch, "E1427.MirrorCS", {"start": v(148.02, -1507.66) * mm, "end": v(148.02, -1623.64) * mm});
            skLineSegment(sketch, "E1428.MirrorCS", {"start": v(59.46, -1628.64) * mm, "end": v(101.24, -1628.64) * mm});
            skPoint(sketch, "E1429.visualSharp", {"position": v(54.46, -1628.64) * mm});
            skArc(sketch, "E1429.filletArc", {"start": v(54.46, -1623.64) * mm, "mid": v(55.92, -1627.17) * mm, "end": v(59.46, -1628.64) * mm});
            skPoint(sketch, "E1430.visualSharp", {"position": v(148.02, -1628.64) * mm});
            skArc(sketch, "E1430.filletArc", {"start": v(143.02, -1628.64) * mm, "mid": v(146.56, -1627.17) * mm, "end": v(148.02, -1623.64) * mm});
            skPoint(sketch, "E1431.visualSharp", {"position": v(54.46, -1386.69) * mm});
            skArc(sketch, "E1431.filletArc", {"start": v(59.46, -1386.69) * mm, "mid": v(55.92, -1388.15) * mm, "end": v(54.46, -1391.69) * mm});
            skPoint(sketch, "E1432.visualSharp", {"position": v(148.02, -1386.69) * mm});
            skArc(sketch, "E1432.filletArc", {"start": v(148.02, -1391.69) * mm, "mid": v(146.56, -1388.15) * mm, "end": v(143.02, -1386.69) * mm});
            skLineSegment(sketch, "E1433.top", {"start": v(394.25, -1350.07) * mm, "end": v(403.84, -1350.07) * mm});
            skPoint(sketch, "E1434.end.orphan", {"position": v(358.5, -1350.07) * mm});
            skLineSegment(sketch, "E1435.bottom", {"start": v(359.34, -1350.07) * mm, "end": v(363.84, -1350.07) * mm});
            skLineSegment(sketch, "E1436.trimOffspring", {"start": v(363.84, -1480.07) * mm, "end": v(363.84, -1454.37) * mm});
            skLineSegment(sketch, "E1437.trimOffspring", {"start": v(363.84, -1427.77) * mm, "end": v(363.84, -1402.37) * mm});
            skLineSegment(sketch, "E1438.trimOffspring", {"start": v(363.84, -1375.77) * mm, "end": v(363.84, -1349.07) * mm});
            skLineSegment(sketch, "E1439", {"start": v(413.95, -1342.74) * mm, "end": v(413.65, -1342.74) * mm});
            skLineSegment(sketch, "E1440.bottom", {"start": v(413.65, -1342.74) * mm, "end": v(413.95, -1342.74) * mm});
            skLineSegment(sketch, "E1440.left", {"start": v(413.65, -1344.57) * mm, "end": v(413.65, -1349.07) * mm});
            skLineSegment(sketch, "E1441", {"start": v(359.34, -1375.77) * mm, "end": v(363.84, -1375.77) * mm});
            skLineSegment(sketch, "E1442", {"start": v(367.62, -1402.07) * mm, "end": v(367.62, -1402.37) * mm});
            skLineSegment(sketch, "E1443", {"start": v(359.34, -1402.37) * mm, "end": v(363.84, -1402.37) * mm});
            skLineSegment(sketch, "E1444", {"start": v(359.34, -1427.77) * mm, "end": v(363.84, -1427.77) * mm});
            skLineSegment(sketch, "E1445", {"start": v(359.34, -1454.37) * mm, "end": v(363.84, -1454.37) * mm});
            skPoint(sketch, "E1446.end.orphan", {"position": v(393.95, -1350.07) * mm});
            skPoint(sketch, "E1447.orphan", {"position": v(363.84, -1402.07) * mm});
            skPoint(sketch, "E1448.orphan", {"position": v(363.84, -1428.07) * mm});
            skPoint(sketch, "E1449.start.orphan", {"position": v(367.62, -1376.07) * mm});
            skPoint(sketch, "E1450.trimOffspring.end.orphan", {"position": v(367.62, -1428.07) * mm});
            skPoint(sketch, "E1451.start.orphan", {"position": v(367.62, -1454.07) * mm});
            skLineSegment(sketch, "E1452.top", {"start": v(359.34, -1480.07) * mm, "end": v(367.62, -1480.07) * mm});
            skLineSegment(sketch, "E1453.top", {"start": v(354.34, -1480.07) * mm, "end": v(367.62, -1480.07) * mm});
            skLineSegment(sketch, "E1453.left", {"start": v(354.34, -1345.92) * mm, "end": v(354.34, -1480.07) * mm});
            skLineSegment(sketch, "E1454.bottom", {"start": v(363.84, -1350.07) * mm, "end": v(359.34, -1350.07) * mm});
            skLineSegment(sketch, "E1454.top", {"start": v(363.84, -1375.77) * mm, "end": v(359.34, -1375.77) * mm});
            skLineSegment(sketch, "E1454.left", {"start": v(363.84, -1350.07) * mm, "end": v(363.84, -1375.77) * mm});
            skLineSegment(sketch, "E1454.right", {"start": v(359.34, -1350.07) * mm, "end": v(359.34, -1375.77) * mm});
            skLineSegment(sketch, "E1455.trimOffspring", {"start": v(359.34, -1454.37) * mm, "end": v(359.34, -1480.07) * mm});
            skLineSegment(sketch, "E1456.trimOffspring", {"start": v(359.34, -1402.37) * mm, "end": v(359.34, -1427.77) * mm});
            skLineSegment(sketch, "E1457", {"start": v(394.25, -1345.57) * mm, "end": v(403.84, -1345.57) * mm});
            skPoint(sketch, "E1458.visualSharp", {"position": v(354.34, -1339.57) * mm});
            skArc(sketch, "E1458.filletArc", {"start": v(360.69, -1339.57) * mm, "mid": v(356.2, -1341.43) * mm, "end": v(354.34, -1345.92) * mm});
            skPoint(sketch, "E1459.start.orphan", {"position": v(423.84, -1328.4) * mm});
            skPoint(sketch, "E1460.orphan", {"position": v(383.54, -1328.4) * mm});
            skPoint(sketch, "E1461.orphan", {"position": v(404.14, -1328.4) * mm});
            skPoint(sketch, "E1462.orphan", {"position": v(393.84, -1328.4) * mm});
            skPoint(sketch, "E1463.MirrorCS.end.orphan", {"position": v(443.84, -1328.4) * mm});
            skPoint(sketch, "E1464.orphan", {"position": v(463.84, -1328.4) * mm});
            skPoint(sketch, "E1465.MirrorCS.end.orphan", {"position": v(464.14, -1328.4) * mm});
            skPoint(sketch, "E1466.MirrorCS.end.orphan", {"position": v(443.54, -1328.4) * mm});
            skLineSegment(sketch, "E1467.bottom", {"start": v(403.84, -1345.57) * mm, "end": v(383.84, -1345.57) * mm});
            skLineSegment(sketch, "E1467.top", {"start": v(403.84, -1350.07) * mm, "end": v(383.84, -1350.07) * mm});
            skLineSegment(sketch, "E1467.left", {"start": v(403.84, -1345.57) * mm, "end": v(403.84, -1350.07) * mm});
            skLineSegment(sketch, "E1467.right", {"start": v(383.84, -1345.57) * mm, "end": v(383.84, -1350.07) * mm});
            skLineSegment(sketch, "E1468", {"start": v(360.69, -1339.57) * mm, "end": v(423.84, -1339.57) * mm});
            skLineSegment(sketch, "E1469.MirrorCS", {"start": v(483.84, -1350.07) * mm, "end": v(488.34, -1350.07) * mm});
            skLineSegment(sketch, "E1470.MirrorCS", {"start": v(483.84, -1375.77) * mm, "end": v(488.34, -1375.77) * mm});
            skLineSegment(sketch, "E1471.MirrorCS", {"start": v(433.72, -1342.74) * mm, "end": v(434.02, -1342.74) * mm});
            skLineSegment(sketch, "E1472.MirrorCS", {"start": v(443.84, -1345.57) * mm, "end": v(443.84, -1350.07) * mm});
            skLineSegment(sketch, "E1473.MirrorCS", {"start": v(434.02, -1342.74) * mm, "end": v(433.72, -1342.74) * mm});
            skLineSegment(sketch, "E1474.MirrorCS", {"start": v(493.34, -1480.07) * mm, "end": v(480.05, -1480.07) * mm});
            skLineSegment(sketch, "E1475.MirrorCS", {"start": v(488.34, -1375.77) * mm, "end": v(483.84, -1375.77) * mm});
            skLineSegment(sketch, "E1476.MirrorCS", {"start": v(488.34, -1350.07) * mm, "end": v(483.84, -1350.07) * mm});
            skLineSegment(sketch, "E1477.MirrorCS", {"start": v(480.05, -1402.07) * mm, "end": v(480.05, -1402.37) * mm});
            skLineSegment(sketch, "E1478.MirrorCS", {"start": v(488.34, -1402.37) * mm, "end": v(483.84, -1402.37) * mm});
            skLineSegment(sketch, "E1479.MirrorCS", {"start": v(463.84, -1345.57) * mm, "end": v(463.84, -1350.07) * mm});
            skLineSegment(sketch, "E1480.MirrorCS", {"start": v(488.34, -1427.77) * mm, "end": v(483.84, -1427.77) * mm});
            skLineSegment(sketch, "E1481.MirrorCS", {"start": v(488.34, -1454.37) * mm, "end": v(483.84, -1454.37) * mm});
            skLineSegment(sketch, "E1482.MirrorCS", {"start": v(453.42, -1350.07) * mm, "end": v(443.84, -1350.07) * mm});
            skLineSegment(sketch, "E1483.MirrorCS", {"start": v(488.34, -1480.07) * mm, "end": v(480.05, -1480.07) * mm});
            skLineSegment(sketch, "E1484.MirrorCS", {"start": v(434.02, -1344.57) * mm, "end": v(434.02, -1349.07) * mm});
            skLineSegment(sketch, "E1485.MirrorCS", {"start": v(483.84, -1350.07) * mm, "end": v(483.84, -1375.77) * mm});
            skArc(sketch, "E1486.MirrorCS", {"start": v(486.99, -1339.57) * mm, "mid": v(491.48, -1341.43) * mm, "end": v(493.34, -1345.92) * mm});
            skPoint(sketch, "E1487.MirrorP", {"position": v(493.34, -1339.57) * mm});
            skLineSegment(sketch, "E1488.MirrorCS", {"start": v(488.34, -1454.37) * mm, "end": v(488.34, -1480.07) * mm});
            skLineSegment(sketch, "E1489.MirrorCS", {"start": v(483.84, -1375.77) * mm, "end": v(483.84, -1349.07) * mm});
            skLineSegment(sketch, "E1490.MirrorCS", {"start": v(443.84, -1350.07) * mm, "end": v(463.84, -1350.07) * mm});
            skPoint(sketch, "E1491.MirrorP", {"position": v(489.17, -1350.07) * mm});
            skLineSegment(sketch, "E1492.MirrorCS", {"start": v(486.99, -1339.57) * mm, "end": v(423.84, -1339.57) * mm});
            skLineSegment(sketch, "E1493.MirrorCS", {"start": v(488.34, -1402.37) * mm, "end": v(488.34, -1427.77) * mm});
            skPoint(sketch, "E1494.MirrorP", {"position": v(480.05, -1454.07) * mm});
            skLineSegment(sketch, "E1495.MirrorCS", {"start": v(483.84, -1427.77) * mm, "end": v(483.84, -1402.37) * mm});
            skLineSegment(sketch, "E1496.MirrorCS", {"start": v(453.42, -1345.57) * mm, "end": v(443.84, -1345.57) * mm});
            skLineSegment(sketch, "E1497.MirrorCS", {"start": v(488.34, -1350.07) * mm, "end": v(488.34, -1375.77) * mm});
            skPoint(sketch, "E1498.MirrorP", {"position": v(480.05, -1428.07) * mm});
            skPoint(sketch, "E1499.MirrorP", {"position": v(480.05, -1376.07) * mm});
            skPoint(sketch, "E1500.MirrorP", {"position": v(483.84, -1402.07) * mm});
            skPoint(sketch, "E1501.MirrorP", {"position": v(453.72, -1350.07) * mm});
            skLineSegment(sketch, "E1502.MirrorCS", {"start": v(443.84, -1345.57) * mm, "end": v(463.84, -1345.57) * mm});
            skPoint(sketch, "E1503.MirrorP", {"position": v(483.84, -1428.07) * mm});
            skLineSegment(sketch, "E1504.MirrorCS", {"start": v(483.84, -1480.07) * mm, "end": v(483.84, -1454.37) * mm});
            skLineSegment(sketch, "E1505.MirrorCS", {"start": v(493.34, -1345.92) * mm, "end": v(493.34, -1480.07) * mm});
            skLineSegment(sketch, "E1506.MirrorCS", {"start": v(413.95, -1617.4) * mm, "end": v(413.65, -1617.4) * mm});
            skLineSegment(sketch, "E1507.MirrorCS", {"start": v(363.84, -1610.07) * mm, "end": v(359.34, -1610.07) * mm});
            skLineSegment(sketch, "E1508.MirrorCS", {"start": v(488.34, -1584.37) * mm, "end": v(483.84, -1584.37) * mm});
            skLineSegment(sketch, "E1509.MirrorCS", {"start": v(488.34, -1610.07) * mm, "end": v(483.84, -1610.07) * mm});
            skLineSegment(sketch, "E1510.MirrorCS", {"start": v(413.65, -1617.4) * mm, "end": v(413.95, -1617.4) * mm});
            skLineSegment(sketch, "E1511.MirrorCS", {"start": v(363.84, -1584.37) * mm, "end": v(359.34, -1584.37) * mm});
            skLineSegment(sketch, "E1512.MirrorCS", {"start": v(367.62, -1558.07) * mm, "end": v(367.62, -1557.77) * mm});
            skLineSegment(sketch, "E1513.MirrorCS", {"start": v(403.84, -1615.57) * mm, "end": v(403.84, -1611.07) * mm});
            skLineSegment(sketch, "E1514.MirrorCS", {"start": v(434.02, -1617.4) * mm, "end": v(433.72, -1617.4) * mm});
            skLineSegment(sketch, "E1515.MirrorCS", {"start": v(359.34, -1584.37) * mm, "end": v(363.84, -1584.37) * mm});
            skLineSegment(sketch, "E1516.MirrorCS", {"start": v(443.84, -1615.57) * mm, "end": v(443.84, -1611.07) * mm});
            skLineSegment(sketch, "E1517.MirrorCS", {"start": v(483.84, -1610.07) * mm, "end": v(488.34, -1610.07) * mm});
            skLineSegment(sketch, "E1518.MirrorCS", {"start": v(359.34, -1610.07) * mm, "end": v(363.84, -1610.07) * mm});
            skLineSegment(sketch, "E1519.MirrorCS", {"start": v(483.84, -1584.37) * mm, "end": v(488.34, -1584.37) * mm});
            skLineSegment(sketch, "E1520.MirrorCS", {"start": v(359.34, -1532.37) * mm, "end": v(363.84, -1532.37) * mm});
            skLineSegment(sketch, "E1521.MirrorCS", {"start": v(359.34, -1557.77) * mm, "end": v(363.84, -1557.77) * mm});
            skLineSegment(sketch, "E1522.MirrorCS", {"start": v(488.34, -1532.37) * mm, "end": v(483.84, -1532.37) * mm});
            skLineSegment(sketch, "E1523.MirrorCS", {"start": v(488.34, -1505.77) * mm, "end": v(483.84, -1505.77) * mm});
            skLineSegment(sketch, "E1524.MirrorCS", {"start": v(383.84, -1615.57) * mm, "end": v(383.84, -1611.07) * mm});
            skLineSegment(sketch, "E1525.MirrorCS", {"start": v(480.05, -1558.07) * mm, "end": v(480.05, -1557.77) * mm});
            skLineSegment(sketch, "E1526.MirrorCS", {"start": v(463.84, -1615.57) * mm, "end": v(463.84, -1611.07) * mm});
            skLineSegment(sketch, "E1527.MirrorCS", {"start": v(433.72, -1617.4) * mm, "end": v(434.02, -1617.4) * mm});
            skLineSegment(sketch, "E1528.MirrorCS", {"start": v(488.34, -1557.77) * mm, "end": v(483.84, -1557.77) * mm});
            skLineSegment(sketch, "E1529.MirrorCS", {"start": v(359.34, -1505.77) * mm, "end": v(363.84, -1505.77) * mm});
            skArc(sketch, "E1530.MirrorCS", {"start": v(486.99, -1620.57) * mm, "mid": v(491.48, -1618.7) * mm, "end": v(493.34, -1614.22) * mm});
            skArc(sketch, "E1531.MirrorCS", {"start": v(360.69, -1620.57) * mm, "mid": v(356.2, -1618.7) * mm, "end": v(354.34, -1614.22) * mm});
            skLineSegment(sketch, "E1532.MirrorCS", {"start": v(413.65, -1615.57) * mm, "end": v(413.65, -1611.07) * mm});
            skLineSegment(sketch, "E1533.MirrorCS", {"start": v(434.02, -1615.57) * mm, "end": v(434.02, -1611.07) * mm});
            skLineSegment(sketch, "E1534.MirrorCS", {"start": v(363.84, -1610.07) * mm, "end": v(363.84, -1584.37) * mm});
            skLineSegment(sketch, "E1535.MirrorCS", {"start": v(483.84, -1584.37) * mm, "end": v(483.84, -1611.07) * mm});
            skPoint(sketch, "E1536.MirrorP", {"position": v(363.84, -1558.07) * mm});
            skLineSegment(sketch, "E1537.MirrorCS", {"start": v(423.84, -1601.04) * mm, "end": v(423.84, -1480.07) * mm});
            skLineSegment(sketch, "E1538.MirrorCS", {"start": v(493.34, -1614.22) * mm, "end": v(493.34, -1480.07) * mm});
            skLineSegment(sketch, "E1539.MirrorCS", {"start": v(488.34, -1557.77) * mm, "end": v(488.34, -1532.37) * mm});
            skPoint(sketch, "E1540.MirrorP", {"position": v(489.17, -1610.07) * mm});
            skPoint(sketch, "E1541.MirrorP", {"position": v(493.34, -1620.57) * mm});
            skPoint(sketch, "E1542.MirrorP", {"position": v(480.05, -1506.07) * mm});
            skLineSegment(sketch, "E1543.MirrorCS", {"start": v(403.84, -1615.57) * mm, "end": v(394.25, -1615.57) * mm});
            skPoint(sketch, "E1544.MirrorP", {"position": v(367.62, -1506.07) * mm});
            skLineSegment(sketch, "E1545.MirrorCS", {"start": v(359.34, -1505.77) * mm, "end": v(359.34, -1480.07) * mm});
            skLineSegment(sketch, "E1546.MirrorCS", {"start": v(486.99, -1620.57) * mm, "end": v(423.84, -1620.57) * mm});
            skLineSegment(sketch, "E1547.MirrorCS", {"start": v(403.84, -1611.07) * mm, "end": v(393.95, -1611.07) * mm});
            skPoint(sketch, "E1548.MirrorP", {"position": v(453.72, -1611.07) * mm});
            skPoint(sketch, "E1549.MirrorP", {"position": v(483.84, -1532.07) * mm});
            skLineSegment(sketch, "E1550.MirrorCS", {"start": v(483.84, -1480.07) * mm, "end": v(483.84, -1505.77) * mm});
            skPoint(sketch, "E1551.MirrorP", {"position": v(363.84, -1532.07) * mm});
            skPoint(sketch, "E1552.MirrorP", {"position": v(367.62, -1584.07) * mm});
            skPoint(sketch, "E1553.MirrorP", {"position": v(480.05, -1532.07) * mm});
            skLineSegment(sketch, "E1554.MirrorCS", {"start": v(363.84, -1532.37) * mm, "end": v(363.84, -1557.77) * mm});
            skLineSegment(sketch, "E1555.MirrorCS", {"start": v(483.84, -1610.07) * mm, "end": v(483.84, -1584.37) * mm});
            skPoint(sketch, "E1556.MirrorP", {"position": v(393.95, -1611.07) * mm});
            skLineSegment(sketch, "E1557.MirrorCS", {"start": v(359.34, -1610.07) * mm, "end": v(359.34, -1584.37) * mm});
            skLineSegment(sketch, "E1558.MirrorCS", {"start": v(488.34, -1610.07) * mm, "end": v(488.34, -1584.37) * mm});
            skLineSegment(sketch, "E1559.MirrorCS", {"start": v(354.34, -1614.22) * mm, "end": v(354.34, -1480.07) * mm});
            skPoint(sketch, "E1560.MirrorP", {"position": v(358.5, -1610.07) * mm});
            skLineSegment(sketch, "E1561.MirrorCS", {"start": v(359.34, -1557.77) * mm, "end": v(359.34, -1532.37) * mm});
            skPoint(sketch, "E1562.MirrorP", {"position": v(367.62, -1532.07) * mm});
            skLineSegment(sketch, "E1563.MirrorCS", {"start": v(363.84, -1584.37) * mm, "end": v(363.84, -1611.07) * mm});
            skPoint(sketch, "E1564.MirrorP", {"position": v(354.34, -1620.57) * mm});
            skPoint(sketch, "E1565.MirrorP", {"position": v(480.05, -1584.07) * mm});
            skLineSegment(sketch, "E1566.MirrorCS", {"start": v(488.34, -1505.77) * mm, "end": v(488.34, -1480.07) * mm});
            skLineSegment(sketch, "E1567.MirrorCS", {"start": v(483.84, -1532.37) * mm, "end": v(483.84, -1557.77) * mm});
            skLineSegment(sketch, "E1568.MirrorCS", {"start": v(360.69, -1620.57) * mm, "end": v(423.84, -1620.57) * mm});
            skLineSegment(sketch, "E1569.MirrorCS", {"start": v(363.84, -1480.07) * mm, "end": v(363.84, -1505.77) * mm});
            skPoint(sketch, "E1570.MirrorP", {"position": v(483.84, -1558.07) * mm});
            skLineSegment(sketch, "E1571", {"start": v(393.95, -1350.07) * mm, "end": v(394.25, -1350.07) * mm});
            skLineSegment(sketch, "E1572.trimOffspring", {"start": v(443.84, -1350.07) * mm, "end": v(453.72, -1350.07) * mm});
            skLineSegment(sketch, "E1573", {"start": v(423.84, -1480.07) * mm, "end": v(438.47, -1480.07) * mm});
            skLineSegment(sketch, "E1574.MirrorCS", {"start": v(463.84, -1614.57) * mm, "end": v(463.84, -1610.07) * mm});
            skLineSegment(sketch, "E1575.MirrorCS", {"start": v(443.84, -1614.57) * mm, "end": v(443.84, -1610.07) * mm});
            skLineSegment(sketch, "E1576.MirrorCS", {"start": v(403.84, -1614.57) * mm, "end": v(403.84, -1610.07) * mm});
            skLineSegment(sketch, "E1577.MirrorCS", {"start": v(393.95, -1610.07) * mm, "end": v(394.25, -1610.07) * mm});
            skLineSegment(sketch, "E1578.MirrorCS", {"start": v(383.84, -1614.57) * mm, "end": v(383.84, -1610.07) * mm});
            skLineSegment(sketch, "E1579.MirrorCS", {"start": v(453.42, -1610.07) * mm, "end": v(443.84, -1610.07) * mm});
            skLineSegment(sketch, "E1580.MirrorCS", {"start": v(394.25, -1610.07) * mm, "end": v(403.84, -1610.07) * mm});
            skLineSegment(sketch, "E1581.MirrorCS", {"start": v(453.42, -1614.57) * mm, "end": v(443.84, -1614.57) * mm});
            skLineSegment(sketch, "E1582.MirrorCS", {"start": v(443.84, -1610.07) * mm, "end": v(453.72, -1610.07) * mm});
            skPoint(sketch, "E1583.MirrorP", {"position": v(393.95, -1610.07) * mm});
            skLineSegment(sketch, "E1584.MirrorCS", {"start": v(403.84, -1610.07) * mm, "end": v(383.84, -1610.07) * mm});
            skLineSegment(sketch, "E1585.MirrorCS", {"start": v(394.25, -1614.57) * mm, "end": v(403.84, -1614.57) * mm});
            skLineSegment(sketch, "E1586.MirrorCS", {"start": v(443.84, -1614.57) * mm, "end": v(463.84, -1614.57) * mm});
            skPoint(sketch, "E1587.MirrorP", {"position": v(453.72, -1610.07) * mm});
            skLineSegment(sketch, "E1588.MirrorCS", {"start": v(443.84, -1610.07) * mm, "end": v(463.84, -1610.07) * mm});
            skLineSegment(sketch, "E1589.MirrorCS", {"start": v(403.84, -1614.57) * mm, "end": v(383.84, -1614.57) * mm});
            skLineSegment(sketch, "E1590", {"start": v(423.84, -1480.07) * mm, "end": v(423.84, -1359.1) * mm});
            skLineSegment(sketch, "E1591", {"start": v(423.84, -1480.07) * mm, "end": v(377.05, -1480.07) * mm});
            skLineSegment(sketch, "E1592.bottom", {"start": v(377.05, -1480.07) * mm, "end": v(423.84, -1480.07) * mm});
            skLineSegment(sketch, "E1592.top", {"start": v(382.05, -1359.1) * mm, "end": v(423.84, -1359.1) * mm});
            skLineSegment(sketch, "E1592.left", {"start": v(377.05, -1480.07) * mm, "end": v(377.05, -1364.1) * mm});
            skLineSegment(sketch, "E1593.MirrorCS", {"start": v(465.62, -1359.1) * mm, "end": v(423.84, -1359.1) * mm});
            skLineSegment(sketch, "E1594.MirrorCS", {"start": v(470.62, -1480.07) * mm, "end": v(470.62, -1359.1) * mm});
            skLineSegment(sketch, "E1595.MirrorCS", {"start": v(470.62, -1480.07) * mm, "end": v(470.62, -1364.1) * mm});
            skLineSegment(sketch, "E1596.MirrorCS", {"start": v(377.05, -1480.07) * mm, "end": v(377.05, -1596.04) * mm});
            skLineSegment(sketch, "E1597.MirrorCS", {"start": v(377.05, -1601.04) * mm, "end": v(423.84, -1601.04) * mm});
            skLineSegment(sketch, "E1598.MirrorCS", {"start": v(465.62, -1601.04) * mm, "end": v(423.84, -1601.04) * mm});
            skLineSegment(sketch, "E1599.MirrorCS", {"start": v(470.62, -1480.07) * mm, "end": v(470.62, -1596.04) * mm});
            skLineSegment(sketch, "E1600.MirrorCS", {"start": v(382.05, -1601.04) * mm, "end": v(423.84, -1601.04) * mm});
            skPoint(sketch, "E1601.visualSharp", {"position": v(377.05, -1601.04) * mm});
            skArc(sketch, "E1601.filletArc", {"start": v(377.05, -1596.04) * mm, "mid": v(378.52, -1599.58) * mm, "end": v(382.05, -1601.04) * mm});
            skPoint(sketch, "E1602.visualSharp", {"position": v(470.62, -1601.04) * mm});
            skArc(sketch, "E1602.filletArc", {"start": v(465.62, -1601.04) * mm, "mid": v(469.15, -1599.58) * mm, "end": v(470.62, -1596.04) * mm});
            skPoint(sketch, "E1603.visualSharp", {"position": v(377.05, -1359.1) * mm});
            skArc(sketch, "E1603.filletArc", {"start": v(382.05, -1359.1) * mm, "mid": v(378.52, -1360.55) * mm, "end": v(377.05, -1364.1) * mm});
            skPoint(sketch, "E1604.visualSharp", {"position": v(470.62, -1359.1) * mm});
            skArc(sketch, "E1604.filletArc", {"start": v(470.62, -1364.1) * mm, "mid": v(469.15, -1360.55) * mm, "end": v(465.62, -1359.1) * mm});
            skCircle(sketch, "E1605.MirrorC", {"center": v(49.04, -1383.48) * mm, "radius": 2.8 * mm});
            skCircle(sketch, "E1606.MirrorC", {"center": v(153.44, -1383.48) * mm, "radius": 2.8 * mm});
            const initialGuessF0  = {"E420": [-0.90992, 0.49712, 1, 0, 0.00645], "E435": [-0.8619, 0.49434, 1, 0, 0.005]};
            skSetInitialGuess(sketch, initialGuessF0);
            skSolve(sketch);
        }
        {
            var Q0;
            {var subQ6=sQuery(id+"F0.wireOp",EDGE,"E382.bottom");Q0=makeQuery(id+"F0.imprint","IMPRINT",FACE,{"disambiguationData":[TD([[makeQuery(id+"F0.imprint","IMPRINT",EDGE,{"derivedFrom":subQ6}),-1.0]])]});}
            var Q1;
            Q1=makeQuery(id+"F0.imprint","IMPRINT",FACE,{"disambiguationData":[TD([[makeQuery(id+"F0.imprint","IMPRINT",EDGE,{"derivedFrom":sQuery(id+"F0.wireOp",EDGE,"E0.top")}),-1.0]])]});
            var Q2;
            Q2=makeQuery(id+"F0.imprint","IMPRINT",FACE,{"disambiguationData":[TD([[makeQuery(id+"F0.imprint","IMPRINT",EDGE,{"derivedFrom":sQuery(id+"F0.wireOp",EDGE,"E2.top")}),1.0]])]});
            var Q3;
            Q3=makeQuery(id+"F0.imprint","IMPRINT",FACE,{"disambiguationData":[TD([[makeQuery(id+"F0.imprint","IMPRINT",EDGE,{"derivedFrom":sQuery(id+"F0.wireOp",EDGE,"E121.bottom")}),1.0]])]});
            var Q4;
            Q4=makeQuery(id+"F0.imprint","IMPRINT",FACE,{"disambiguationData":[TD([[makeQuery(id+"F0.imprint","IMPRINT",EDGE,{"derivedFrom":sQuery(id+"F0.wireOp",EDGE,"E1.bottom")}),-1.0]])]});
            var Q5;
            Q5=makeQuery(id+"F0.imprint","IMPRINT",FACE,{"disambiguationData":[TD([[makeQuery(id+"F0.imprint","IMPRINT",EDGE,{"derivedFrom":sQuery(id+"F0.wireOp",EDGE,"E242.bottom")}),-1.0]])]});
            extrude(context, id + "F1", {"entities" : qUnion([Q0, Q1, Q2, Q3, Q4, Q5]), "depth" : 6.33 * mm, "offsetDistance" : 25 * mm});
        }
        {
            var Q0;
            Q0=makeQuery(id+"F0.imprint","IMPRINT",FACE,{"disambiguationData":[TD([[makeQuery(id+"F0.imprint","IMPRINT",EDGE,{"derivedFrom":sQuery(id+"F0.wireOp",EDGE,"E716.trimOffspring")}),-1.0]])]});
            var Q1;
            Q1=makeQuery(id+"F0.imprint","IMPRINT",FACE,{"disambiguationData":[TD([[makeQuery(id+"F0.imprint","IMPRINT",EDGE,{"derivedFrom":sQuery(id+"F0.wireOp",EDGE,"E739.bottom")}),-1.0]])]});
            var Q2;
            Q2=makeQuery(id+"F0.imprint","IMPRINT",FACE,{"disambiguationData":[TD([[makeQuery(id+"F0.imprint","IMPRINT",EDGE,{"derivedFrom":sQuery(id+"F0.wireOp",EDGE,"E960.bottom")}),-1.0]])]});
            var Q3;
            Q3=makeQuery(id+"F0.imprint","IMPRINT",FACE,{"disambiguationData":[TD([[makeQuery(id+"F0.imprint","IMPRINT",EDGE,{"derivedFrom":sQuery(id+"F0.wireOp",EDGE,"E1229.bottom")}),-1.0]])]});
            var Q4;
            Q4=makeQuery(id+"F0.imprint","IMPRINT",FACE,{"disambiguationData":[TD([[makeQuery(id+"F0.imprint","IMPRINT",EDGE,{"derivedFrom":sQuery(id+"F0.wireOp",EDGE,"E1436.trimOffspring")}),-1.0]])]});
            var Q5;
            Q5=makeQuery(id+"F0.imprint","IMPRINT",FACE,{"disambiguationData":[TD([[makeQuery(id+"F0.imprint","IMPRINT",EDGE,{"derivedFrom":sQuery(id+"F0.wireOp",EDGE,"E1262.trimOffspring")}),-1.0]])]});
            extrude(context, id + "F2", {"entities" : qUnion([Q0, Q1, Q2, Q3, Q4, Q5]), "depth" : 5 * mm, "offsetDistance" : 25 * mm});
        }
    });
